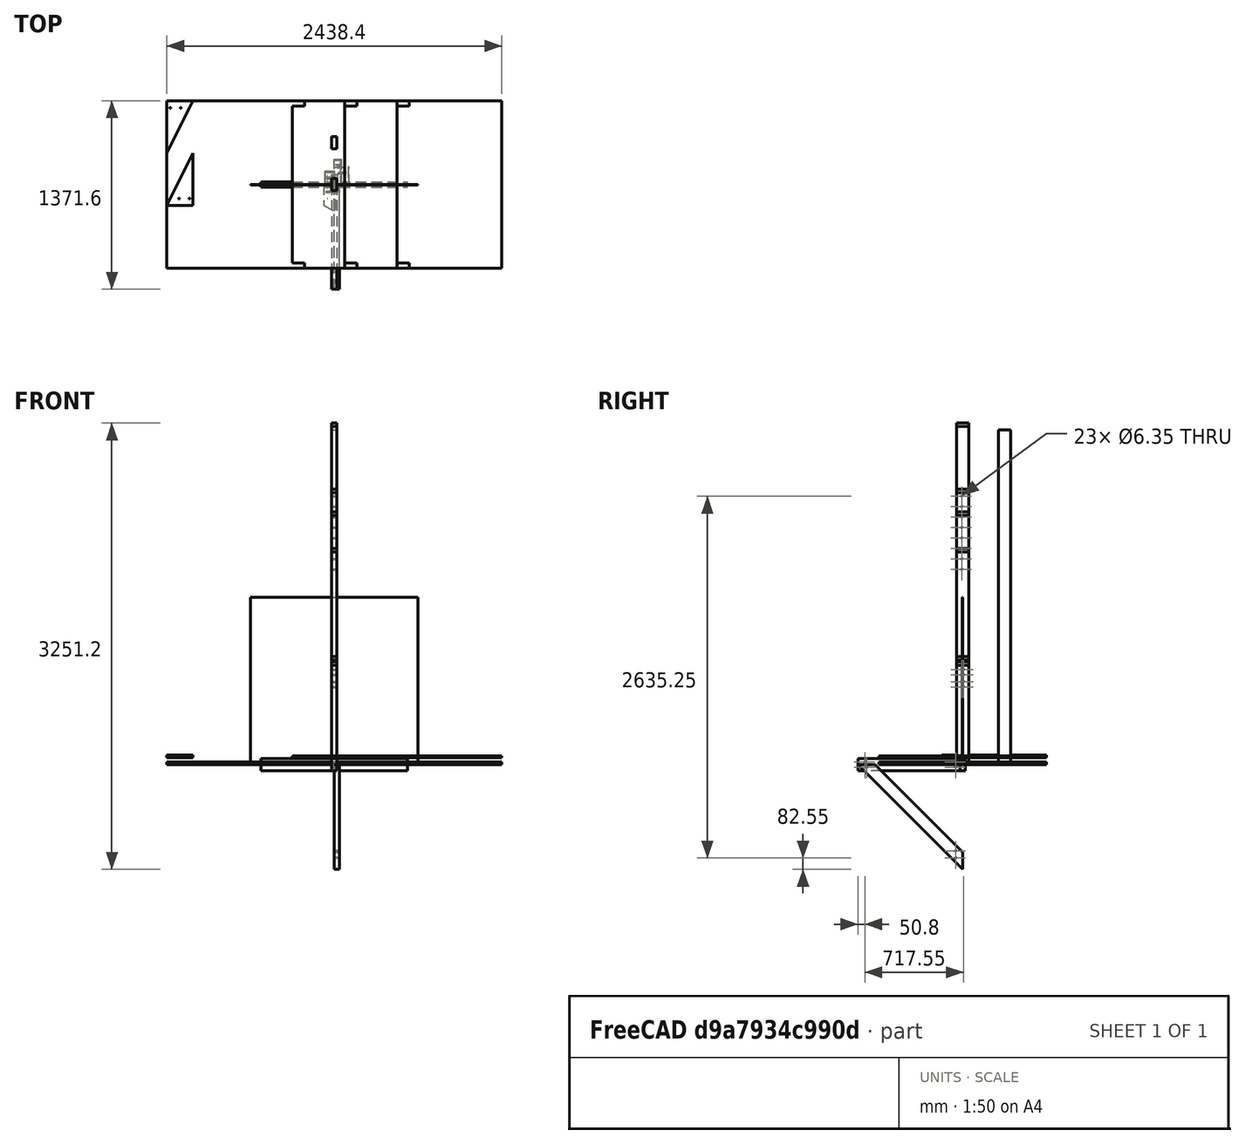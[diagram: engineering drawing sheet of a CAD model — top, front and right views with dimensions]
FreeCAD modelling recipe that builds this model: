
FCSTD DOCUMENT  (FreeCAD 0.21R33771 (Git))
Label: workshop
License: All rights reserved
LicenseURL: http://en.wikipedia.org/wiki/All_rights_reserved
objects: Sketcher::SketchObject×41, PartDesign::Pad×34, PartDesign::Body×29, TechDraw::DrawViewBalloon×25, TechDraw::DrawViewPart×23, App::Part×22, PartDesign::CoordinateSystem×21, PartDesign::Pocket×21, Part::Part2DObjectPython×18, App::Link×17, TechDraw::DrawViewDimension×14, TechDraw::DrawRichAnno×13, TechDraw::DrawSVGTemplate×11, TechDraw::DrawPage×11, App::DocumentObjectGroup×10, Part::FeaturePython×7, PartDesign::Mirrored×3, PartDesign::Hole×1, App::FeaturePython×1, Spreadsheet::Sheet×1
note: 252 computed .brp shape members not serialized (recipe doc carries the construction recipe); baked Part::Feature solids carry a one-line shape summary decoded from their .brp

FEATURE [Sketcher::SketchObject] Sketch  label="S_Electronics_CableMount_Body"
  FullyConstrained = true
  MapMode = 5
  Support = -> [XY_Plane001]
  sketch-geometry (8):
    g0: LineSegment StartX=12.5 StartY=42.5 StartZ=0 EndX=12.5 EndY=12.5 EndZ=0
    g1: LineSegment StartX=-12.5 StartY=12.5 StartZ=0 EndX=-12.5 EndY=42.5 EndZ=0
    g2: ArcOfCircle CenterX=3e-15 CenterY=12.5 CenterZ=0 NormalX=0 NormalY=0 NormalZ=1 AngleXU=0 Radius=12.5 StartAngle=3.14159 EndAngle=6.28319
    g3: LineSegment StartX=22.5 StartY=42.5 StartZ=0 EndX=22.5 EndY=12.5 EndZ=0
    g4: LineSegment StartX=-22.5 StartY=12.5 StartZ=0 EndX=-22.5 EndY=42.5 EndZ=0
    g5: ArcOfCircle CenterX=5.7957e-12 CenterY=12.5 CenterZ=0 NormalX=0 NormalY=0 NormalZ=1 AngleXU=0 Radius=22.5 StartAngle=3.14159 EndAngle=6.28319
    g6: LineSegment StartX=-12.5 StartY=42.5 StartZ=0 EndX=-22.5 EndY=42.5 EndZ=0
    g7: LineSegment StartX=22.5 StartY=42.5 StartZ=0 EndX=12.5 EndY=42.5 EndZ=0
  constraints (20):
    c: Vertical(g0)
    c: Symmetric(g0,g1,g-2)
    c: PointOnObject(g-1,g2)
    c: Tangent(g2,g0) = 1.5708
    c: Tangent(g1,g2) = 1.5708
    c: Vertical(g3)
    c: Coincident(g6,g1)
    c: Coincident(g6,g4)
    c: Coincident(g7,g3)
    c: Coincident(g7,g0)
    c: Tangent(g5,g3) = 1.5708
    c: Tangent(g4,g5) = 1.5708
    c: Horizontal(g6)
    c: Horizontal(g7)
    c: Horizontal(g4,g3)
    c: Horizontal(g4,g1)
    c: Symmetric(g3,g4,g-2)
    c: DistanceX(g7,g7) = 10
    c: DistanceX(g1,g0) = 25
    c: DistanceY(g3,g3) = 30
FEATURE [PartDesign::Pad] Pad  label="PAD_Electronics_CableMount"
  Direction = (0,0,1)
  Length = 10
  Length2 = 10
  Profile = -> Sketch
  ReferenceAxis = -> Sketch [N_Axis]
  Type = 0
FEATURE [Sketcher::SketchObject] Sketch001  label="S_Electronics_CableMount_Hole"
  AttachmentOffset = pos=(0,0,30) rot=(0,0,1;0rad)
  FullyConstrained = true
  MapMode = 5
  Placement = pos=(30,-6.7e-15,6.7e-15) rot=(0.57735,0.57735,0.57735;2.0944rad)
  Support = -> [YZ_Plane001]
  sketch-geometry (1):
    g0: Circle CenterX=35 CenterY=5 CenterZ=0 NormalX=0 NormalY=0 NormalZ=1 AngleXU=0 Radius=2.5
  constraints (3):
    c: Diameter(g0) = 5
    c: DistanceY(g-1,g0) = 5
    c: DistanceX(g-1,g0) = 35
FEATURE [PartDesign::Hole] Hole  label="HOLE_Electronics_CableMount"
  BaseFeature = -> Pad
  CustomThreadClearance = 0
  Depth = 161.858
  DepthType = 1
  Diameter = 5.5
  DrillForDepth = false
  DrillPoint = 0
  DrillPointAngle = 118
  HoleCutCountersinkAngle = 90
  HoleCutCustomValues = false
  HoleCutDepth = 0
  HoleCutDiameter = 6.1
  HoleCutType = 0
  ModelThread = false
  Profile = -> Sketch001
  Tapered = false
  TaperedAngle = 90
  ThreadClass = 0
  ThreadDepth = 161.858
  ThreadDepthType = 0
  ThreadDirection = 0
  ThreadFit = 0
  ThreadSize = 13
  ThreadType = 1
  Threaded = false
  UseCustomThreadClearance = false
FEATURE [PartDesign::Body] Body  label="B_Electronics_CableMount"
  Group = -> [Sketch,Pad,Sketch001,Hole]
  Origin = -> Origin001
  Tip = -> Hole
FEATURE [App::Part] Part  label="P_Electronics_CableMount"
  Group = -> [Body]
  Origin = -> Origin
FEATURE [Sketcher::SketchObject] Sketch002  label="S_Electronics_CableMountSpacer"
  FullyConstrained = true
  MapMode = 5
  Support = -> [XY_Plane003]
  sketch-geometry (7):
    g0: LineSegment StartX=-25 StartY=0 StartZ=0 EndX=25 EndY=0 EndZ=0
    g1: LineSegment StartX=25 StartY=0 StartZ=0 EndX=25 EndY=70 EndZ=0
    g2: LineSegment StartX=25 StartY=70 StartZ=0 EndX=-25 EndY=70 EndZ=0
    g3: LineSegment StartX=-25 StartY=70 StartZ=0 EndX=-25 EndY=0 EndZ=0
    g4: Circle CenterX=0 CenterY=60 CenterZ=0 NormalX=0 NormalY=0 NormalZ=1 AngleXU=0 Radius=2.5
    g5: Circle CenterX=0 CenterY=35 CenterZ=0 NormalX=0 NormalY=0 NormalZ=1 AngleXU=0 Radius=2.5
    g6: Circle CenterX=0 CenterY=10 CenterZ=0 NormalX=0 NormalY=0 NormalZ=1 AngleXU=0 Radius=2.5
  constraints (20):
    c: Coincident(g0,g1)
    c: Coincident(g1,g2)
    c: Coincident(g2,g3)
    c: Coincident(g3,g0)
    c: Horizontal(g2)
    c: Vertical(g1)
    c: Vertical(g3)
    c: PointOnObject(g0,g-1)
    c: Symmetric(g0,g0,g-2)
    c: DistanceX(g2,g2) = 50
    c: DistanceY(g1,g1) = 70
    c: PointOnObject(g4,g-2)
    c: PointOnObject(g5,g-2)
    c: PointOnObject(g6,g-2)
    c: Equal(g6,g5)
    c: Equal(g5,g4)
    c: Diameter(g4) = 5
    c: DistanceY(g-1,g6) = 10
    c: DistanceY(g4,g2) = 10
    c: DistanceY(g-1,g5) = 35
FEATURE [PartDesign::Pad] Pad001  label="PAD_Electronics_CableMountSpacer"
  Direction = (0,0,1)
  Length = 2
  Length2 = 10
  Profile = -> Sketch002
  ReferenceAxis = -> Sketch002 [N_Axis]
  Type = 0
FEATURE [Sketcher::SketchObject] Sketch003  label="S_Electronics_CableMountSpacer_Side"
  FullyConstrained = true
  MapMode = 5
  Support = -> [XY_Plane003]
  expr: Constraints[9] = 41.5 mm / 2
  sketch-geometry (4):
    g0: LineSegment StartX=20.75 StartY=70 StartZ=0 EndX=25 EndY=70 EndZ=0
    g1: LineSegment StartX=25 StartY=70 StartZ=0 EndX=25 EndY=0 EndZ=0
    g2: LineSegment StartX=25 StartY=0 StartZ=0 EndX=20.75 EndY=0 EndZ=0
    g3: LineSegment StartX=20.75 StartY=0 StartZ=0 EndX=20.75 EndY=70 EndZ=0
  constraints (12):
    c: Coincident(g0,g1)
    c: Coincident(g1,g2)
    c: Coincident(g2,g3)
    c: Coincident(g3,g0)
    c: Horizontal(g0)
    c: Horizontal(g2)
    c: Vertical(g1)
    c: Vertical(g3)
    c: PointOnObject(g1,g-1)
    c: DistanceX(g-1,g2) = 20.75
    c: DistanceX(g-1,g1) = 25
    c: DistanceY(g1,g1) = 70
FEATURE [PartDesign::Pad] Pad002  label="PAD_Electronics_CableMountSpacer_Side"
  BaseFeature = -> Pad001
  Direction = (0,0,1)
  Length = 4
  Length2 = 10
  Profile = -> Sketch003
  ReferenceAxis = -> Sketch003 [N_Axis]
  Type = 0
FEATURE [PartDesign::Mirrored] Mirrored  label="PAT_Electronics_CableMountSpacer_Side"
  BaseFeature = -> Pad002
  MirrorPlane = -> Sketch003 [V_Axis]
  Originals = -> [Pad002]
FEATURE [PartDesign::Body] Body001  label="B_Electronics_CableMountSpacer"
  Group = -> [Sketch002,Pad001,Sketch003,Pad002,Mirrored]
  Origin = -> Origin003
  Tip = -> Mirrored
FEATURE [App::Part] Part001  label="P_Electronics_CableMountSpacer"
  Group = -> [Body001]
  Origin = -> Origin002
FEATURE [PartDesign::CoordinateSystem] LCS_Origin
  AttacherType = Attacher::AttachEngine3D
  MapMode = 2
  Support = -> [X_Axis008]
FEATURE [App::DocumentObjectGroup] Constraints
FEATURE [App::FeaturePython] Variables  # WARN: FeaturePython — macro-defined, semantics opaque (R4)
  Type = App::PropertyContainer
FEATURE [App::DocumentObjectGroup] Configurations
FEATURE [Sketcher::SketchObject] Sketch005  label="S_Workbench_Top_Base"
  FullyConstrained = true
  MapMode = 5
  Support = -> [XY_Plane007]
  expr: Constraints[8] = <<S_Workbench_Master>>.Constraints.TableWidth
  sketch-geometry (4):
    g0: LineSegment StartX=-609.6 StartY=0 StartZ=0 EndX=609.6 EndY=0 EndZ=0
    g1: LineSegment StartX=609.6 StartY=0 StartZ=0 EndX=609.6 EndY=-762 EndZ=0
    g2: LineSegment StartX=609.6 StartY=-762 StartZ=0 EndX=-609.6 EndY=-762 EndZ=0
    g3: LineSegment StartX=-609.6 StartY=-762 StartZ=0 EndX=-609.6 EndY=0 EndZ=0
  constraints (11):
    c: Coincident(g0,g1)
    c: Coincident(g1,g2)
    c: Coincident(g2,g3)
    c: Coincident(g3,g0)
    c: Horizontal(g0)
    c: Horizontal(g2)
    c: Vertical(g1)
    c: Vertical(g3)
    c: DistanceX(g0,g0) = 1219.2
    c: DistanceY(g1,g1) = 762
    c: Symmetric(g0,g0,g-1)
FEATURE [PartDesign::Pad] Pad004  label="PAD_Workbench_Top_Base"
  Direction = (0,0,1)
  Length = 12.7
  Length2 = 10
  Profile = -> Sketch005
  ReferenceAxis = -> Sketch005 [N_Axis]
  Type = 0
  expr: Length = <<S_Workbench_Master>>.Constraints.TableThickness
FEATURE [Sketcher::SketchObject] Sketch006  label="S_Workbench_Top_BackHole"
  ExternalGeometry = -> [Pad004]
  FullyConstrained = true
  MapMode = 5
  Placement = pos=(0,0,12.7) rot=(0,0,1;0rad)
  Support = -> [Pad004]
  expr: Constraints[8] = Sketch009.Constraints.TwobyfourWidth
  expr: Constraints[9] = Sketch009.Constraints.TwobyfourHeight
  sketch-geometry (4):
    g0: LineSegment StartX=-571.5 StartY=0 StartZ=0 EndX=-609.6 EndY=0 EndZ=0
    g1: LineSegment StartX=-609.6 StartY=0 StartZ=0 EndX=-609.6 EndY=-88.9 EndZ=0
    g2: LineSegment StartX=-609.6 StartY=-88.9 StartZ=0 EndX=-571.5 EndY=-88.9 EndZ=0
    g3: LineSegment StartX=-571.5 StartY=-88.9 StartZ=0 EndX=-571.5 EndY=0 EndZ=0
  constraints (11):
    c: Coincident(g0,g1)
    c: Coincident(g1,g2)
    c: Coincident(g2,g3)
    c: Coincident(g3,g0)
    c: Horizontal(g0)
    c: Horizontal(g2)
    c: Vertical(g1)
    c: Vertical(g3)
    c: DistanceX(g0,g0) = 38.1
    c: DistanceY(g3,g3) = 88.9
    c: Coincident(g0,g-3)
FEATURE [PartDesign::Pocket] Pocket  label="POCKET_Workbench_Top_BackHole"
  BaseFeature = -> Pad004
  Direction = (0,0,-1)
  Length = 25.4
  Length2 = 5
  Profile = -> Sketch006
  ReferenceAxis = -> Sketch006 [N_Axis]
  Type = 0
FEATURE [PartDesign::Mirrored] Mirrored001  label="PAT_B_Workbench_Top_BackHoles"
  BaseFeature = -> Pocket
  MirrorPlane = -> Sketch006 [V_Axis]
  Originals = -> [Pocket]
FEATURE [PartDesign::Body] Body003  label="B_Workbench_Top"
  Group = -> [Sketch005,Pad004,Sketch006,Pocket,Mirrored001]
  Origin = -> Origin007
  Tip = -> Mirrored001
FEATURE [PartDesign::CoordinateSystem] LCS_Workbench_Top_Origin
  AttacherType = Attacher::AttachEngine3D
FEATURE [PartDesign::CoordinateSystem] LCS_Workbench_Top_Back_Left_Leg
  AttacherType = Attacher::AttachEngine3D
  Placement = pos=(-590.55,-44.45,0) rot=(0,0,1;0rad)
  expr: .Placement.Base.x = -(<<S_Workbench_Master>>.Constraints.TableWidth - Sketch009.Constraints.TwobyfourWidth) / 2
  expr: .Placement.Base.y = -Sketch009.Constraints.TwobyfourHeight / 2
FEATURE [PartDesign::CoordinateSystem] LCS_Workbench_Top_Back_Right_Leg
  AttacherType = Attacher::AttachEngine3D
  Placement = pos=(590.55,-44.45,0) rot=(0,0,1;0rad)
  expr: .Placement.Base.x = (<<S_Workbench_Master>>.Constraints.TableWidth - Sketch009.Constraints.TwobyfourWidth) / 2
  expr: .Placement.Base.y = -Sketch009.Constraints.TwobyfourHeight / 2
FEATURE [PartDesign::CoordinateSystem] LCS_Workbench_Top_Front_Left_Leg
  AttacherType = Attacher::AttachEngine3D
  Placement = pos=(-590.55,-717.55,0) rot=(0,0,1;0rad)
  expr: .Placement.Base.x = -(<<S_Workbench_Master>>.Constraints.TableWidth - Sketch009.Constraints.TwobyfourWidth) / 2
  expr: .Placement.Base.y = -<<S_Workbench_Master>>.Constraints.TableDepth + Sketch009.Constraints.TwobyfourHeight / 2
FEATURE [PartDesign::CoordinateSystem] LCS_Workbench_Top_Front_Right_Leg
  AttacherType = Attacher::AttachEngine3D
  Placement = pos=(590.55,-717.55,0) rot=(0,0,1;0rad)
  expr: .Placement.Base.x = (<<S_Workbench_Master>>.Constraints.TableWidth - Sketch009.Constraints.TwobyfourWidth) / 2
  expr: .Placement.Base.y = -<<S_Workbench_Master>>.Constraints.TableDepth + Sketch009.Constraints.TwobyfourHeight / 2
FEATURE [App::Part] Part003  label="P_Workbench_Top"
  Group = -> [Body003,LCS_Workbench_Top_Origin,LCS_Workbench_Top_Back_Left_Leg,LCS_Workbench_Top_Back_Right_Leg,LCS_Workbench_Top_Front_Left_Leg,LCS_Workbench_Top_Front_Right_Leg]
  Origin = -> Origin006
FEATURE [Sketcher::SketchObject] Sketch007  label="S_Workbench_BackLeg_Base"
  FullyConstrained = true
  MapMode = 5
  Support = -> [XY_Plane010]
  expr: Constraints[10] = Sketch009.Constraints.TwobyfourHeight
  expr: Constraints[9] = Sketch009.Constraints.TwobyfourWidth
  sketch-geometry (4):
    g0: LineSegment StartX=-19.05 StartY=44.45 StartZ=0 EndX=19.05 EndY=44.45 EndZ=0
    g1: LineSegment StartX=19.05 StartY=44.45 StartZ=0 EndX=19.05 EndY=-44.45 EndZ=0
    g2: LineSegment StartX=19.05 StartY=-44.45 StartZ=0 EndX=-19.05 EndY=-44.45 EndZ=0
    g3: LineSegment StartX=-19.05 StartY=-44.45 StartZ=0 EndX=-19.05 EndY=44.45 EndZ=0
  constraints (11):
    c: Coincident(g0,g1)
    c: Coincident(g1,g2)
    c: Coincident(g2,g3)
    c: Coincident(g3,g0)
    c: Horizontal(g0)
    c: Horizontal(g2)
    c: Vertical(g1)
    c: Vertical(g3)
    c: Symmetric(g0,g1,g-1)
    c: DistanceX(g0,g0) = 38.1
    c: DistanceY(g1,g1) = 88.9
FEATURE [PartDesign::Pad] Pad005  label="PAD_Workbench_BackLeg"
  Direction = (0,0,1)
  Length = 1981.2
  Length2 = 10
  Profile = -> Sketch007
  ReferenceAxis = -> Sketch007 [N_Axis]
  Type = 0
  expr: Length = <<S_Workbench_Master>>.Constraints.BackLegHeight
FEATURE [PartDesign::CoordinateSystem] LCS_BackLeg_Origin  label="LCS_Workbench_BackLeg_Origin"
  AttacherType = Attacher::AttachEngine3D
FEATURE [PartDesign::CoordinateSystem] LCS_Workbench_BackLeg_Top
  AttacherType = Attacher::AttachEngine3D
  Placement = pos=(0,0,1981.2) rot=(0,0,1;0rad)
  expr: .Placement.Base.z = <<S_Workbench_Master>>.Constraints.BackLegHeight
FEATURE [PartDesign::CoordinateSystem] LCS_Workbench_BackLeg_TableHeight
  AttacherType = Attacher::AttachEngine3D
  Placement = pos=(0,0,723.9) rot=(0,0,1;0rad)
  expr: .Placement.Base.z = Sketch009.Constraints.FrontLegHeight
FEATURE [App::Link] P_Workbench_BackLeg  label="P_Workbench_BackLeg001"
  AttachedBy = #LCS_BackLeg_Origin
  AttachedTo = P_Workbench_Top#LCS_Workbench_Top_Back_Right_Leg
  AttachmentOffset = pos=(0,0,-723.9) rot=(0,0,1;0rad)
  LinkPlacement = pos=(590.55,-44.45,0) rot=(0,0,1;0rad)
  LinkedObject = -> Part004
  Placement = pos=(590.55,-44.45,0) rot=(0,0,1;0rad)
  SolverId = Asm4EE
  expr: .AttachmentOffset.Base.z = -<<S_Workbench_Master>>.Constraints.FrontLegHeight
  expr: Placement = P_Workbench_Top.Placement * LCS_Workbench_Top_Back_Right_Leg.Placement * AttachmentOffset * LCS_BackLeg_Origin.Placement ^ -1
FEATURE [App::Link] P_Workbench_BackLeg001  label="P_Workbench_BackLeg002"
  AttachedBy = #LCS_BackLeg_Origin
  AttachedTo = P_Workbench_Top#LCS_Workbench_Top_Back_Left_Leg
  AttachmentOffset = pos=(0,0,-723.9) rot=(0,0,1;0rad)
  LinkPlacement = pos=(-590.55,-44.45,0) rot=(0,0,1;0rad)
  LinkedObject = -> Part004
  Placement = pos=(-590.55,-44.45,0) rot=(0,0,1;0rad)
  SolverId = Asm4EE
  expr: .AttachmentOffset.Base.z = -<<S_Workbench_Master>>.Constraints.FrontLegHeight
  expr: Placement = P_Workbench_Top.Placement * LCS_Workbench_Top_Back_Left_Leg.Placement * AttachmentOffset * LCS_BackLeg_Origin.Placement ^ -1
FEATURE [App::Link] P_Workbench_Top  label="P_Workbench_Top001"
  AttachedBy = #LCS_Workbench_Top_Origin
  AttachedTo = Parent Assembly#LCS_Origin
  AttachmentOffset = pos=(0,0,723.9) rot=(0,0,1;0rad)
  LinkPlacement = pos=(0,0,723.9) rot=(0,0,1;0rad)
  LinkedObject = -> Part003
  Placement = pos=(0,0,723.9) rot=(0,0,1;0rad)
  SolverId = Asm4EE
  expr: .AttachmentOffset.Base.z = <<S_Workbench_Master>>.Constraints.FrontLegHeight
  expr: Placement = LCS_Origin.Placement * AttachmentOffset * LCS_Workbench_Top_Origin.Placement ^ -1
FEATURE [Sketcher::SketchObject] Sketch008  label="S_Workbench_FrontLeg_Base"
  FullyConstrained = true
  MapMode = 5
  Support = -> [XY_Plane012]
  expr: Constraints[10] = Sketch009.Constraints.TwobyfourHeight
  expr: Constraints[9] = Sketch009.Constraints.TwobyfourWidth
  sketch-geometry (4):
    g0: LineSegment StartX=-19.05 StartY=44.45 StartZ=0 EndX=19.05 EndY=44.45 EndZ=0
    g1: LineSegment StartX=19.05 StartY=44.45 StartZ=0 EndX=19.05 EndY=-44.45 EndZ=0
    g2: LineSegment StartX=19.05 StartY=-44.45 StartZ=0 EndX=-19.05 EndY=-44.45 EndZ=0
    g3: LineSegment StartX=-19.05 StartY=-44.45 StartZ=0 EndX=-19.05 EndY=44.45 EndZ=0
  constraints (11):
    c: Coincident(g0,g1)
    c: Coincident(g1,g2)
    c: Coincident(g2,g3)
    c: Coincident(g3,g0)
    c: Horizontal(g0)
    c: Horizontal(g2)
    c: Vertical(g1)
    c: Vertical(g3)
    c: Symmetric(g0,g1,g-1)
    c: DistanceX(g0,g0) = 38.1
    c: DistanceY(g1,g1) = 88.9
FEATURE [PartDesign::Pad] Pad006  label="PAD_Workbench_FrontLeg_Base"
  Direction = (0,0,1)
  Length = 723.9
  Length2 = 10
  Profile = -> Sketch008
  ReferenceAxis = -> Sketch008 [N_Axis]
  Type = 0
  expr: Length = Sketch009.Constraints.FrontLegHeight
FEATURE [Sketcher::SketchObject] Sketch009  label="S_Workbench_Master"
  FullyConstrained = true
  Placement = pos=(0,0,0) rot=(1,0,0;1.5708rad)
  sketch-geometry (23):
    g0: LineSegment StartX=0 StartY=0 StartZ=0 EndX=0 EndY=736.6 EndZ=0
    g1: LineSegment StartX=0 StartY=736.6 StartZ=0 EndX=1219.2 EndY=736.6 EndZ=0
    g2: LineSegment StartX=1219.2 StartY=736.6 StartZ=0 EndX=1758.02 EndY=1275.42 EndZ=0
    g3: LineSegment StartX=0 StartY=736.6 StartZ=0 EndX=538.815 EndY=1275.42 EndZ=0
    g4: LineSegment StartX=538.815 StartY=1275.42 StartZ=0 EndX=1758.02 EndY=1275.42 EndZ=0
    g5: LineSegment StartX=538.815 StartY=1275.42 StartZ=0 EndX=538.815 EndY=2520.02 EndZ=0
    g6: LineSegment StartX=538.815 StartY=1275.42 StartZ=0 EndX=538.815 EndY=538.815 EndZ=0
    g7: LineSegment StartX=538.815 StartY=2062.82 StartZ=0 EndX=269.408 EndY=1793.41 EndZ=0
    g8: LineSegment StartX=0 StartY=723.9 StartZ=0 EndX=1219.2 EndY=723.9 EndZ=0
    g9: LineSegment StartX=1219.2 StartY=723.9 StartZ=0 EndX=1219.2 EndY=736.6 EndZ=0
    g10: LineSegment StartX=1219.2 StartY=723.9 StartZ=0 EndX=1758.02 EndY=1262.72 EndZ=0
    g11: LineSegment StartX=1758.02 StartY=1262.72 StartZ=0 EndX=1758.02 EndY=1275.42 EndZ=0
    g12: LineSegment StartX=538.815 StartY=2367.62 StartZ=0 EndX=269.408 EndY=2098.21 EndZ=0
    g13: LineSegment StartX=0 StartY=723.9 StartZ=0 EndX=538.815 EndY=1262.72 EndZ=0
    g14: LineSegment StartX=1758.02 StartY=1275.42 StartZ=0 EndX=1760.26 EndY=1277.66 EndZ=0
    g15: LineSegment StartX=1760.26 StartY=1277.66 StartZ=0 EndX=1760.26 EndY=2496.86 EndZ=0
    g16: LineSegment StartX=1758.02 StartY=1275.42 StartZ=0 EndX=1758.02 EndY=2494.62 EndZ=0
    g17: LineSegment StartX=1758.02 StartY=2494.62 StartZ=0 EndX=1760.26 EndY=2496.86 EndZ=0
    g18: LineSegment StartX=-647.7 StartY=-609.6 StartZ=0 EndX=-609.6 EndY=-609.6 EndZ=0
    g19: LineSegment StartX=-609.6 StartY=-609.6 StartZ=0 EndX=-609.6 EndY=-698.5 EndZ=0
    g20: LineSegment StartX=-609.6 StartY=-698.5 StartZ=0 EndX=-647.7 EndY=-698.5 EndZ=0
    g21: LineSegment StartX=-647.7 StartY=-698.5 StartZ=0 EndX=-647.7 EndY=-609.6 EndZ=0
    g22: Circle CenterX=50.8 CenterY=-50.8 CenterZ=0 NormalX=0 NormalY=0 NormalZ=1 AngleXU=0 Radius=3.175
  constraints (71):
    c: Coincident(g0,g-1)
    c: Vertical(g0)
    c: DistanceY(g0,g0) = 736.6  'TableHeight'
    c: Coincident(g1,g0)
    c: Horizontal(g1)
    c: DistanceX(g1,g1) = 1219.2  'TableWidth'
    c: Coincident(g2,g1)
    c: Angle(g2,g1) = 2.35619
    c: Distance(g2) = 762  'TableDepth'
    c: Coincident(g3,g0)
    c: Coincident(g4,g2)
    c: Horizontal(g4)
    c: Equal(g4,g1)
    c: Coincident(g3,g4)
    c: Coincident(g5,g3)
    c: Vertical(g5)
    c: Coincident(g6,g3)
    c: Vertical(g6)
    c: Equal(g6,g0)
    c: DistanceY(g6,g5) = 1981.2  'BackLegHeight'
    c: PointOnObject(g7,g5)
    c: Parallel(g7,g3)
    c: Distance(g7) = 381  'ShelfDepth'
    c: DistanceY(g6,g7) = 1524  'ShelfHeight'
    c: DistanceY(g3,g7) = 787.4
    c: PointOnObject(g8,g0)
    c: Horizontal(g8)
    c: Coincident(g9,g8)
    c: Coincident(g9,g1)
    c: Vertical(g9)
    c: Coincident(g10,g8)
    c: Coincident(g11,g10)
    c: Coincident(g11,g2)
    c: Vertical(g11)
    c: Parallel(g10,g2)
    c: DistanceY(g11,g11) = 12.7  'TableThickness'
    c: DistanceY(g0,g8) = 723.9  'FrontLegHeight'
    c: PointOnObject(g12,g5)
    c: Parallel(g12,g7)
    c: Equal(g12,g7)
    c: DistanceY(g7,g12) = 304.8  'ShelfSpacing'
    c: Coincident(g13,g8)
    c: PointOnObject(g13,g6)
    c: Parallel(g13,g3)
    c: DistanceY(g6,g6) = 736.6
    c: Coincident(g14,g2)
    c: Coincident(g15,g14)
    c: Vertical(g15)
    c: Coincident(g16,g2)
    c: Vertical(g16)
    c: Coincident(g17,g16)
    c: Coincident(g17,g15)
    c: Parallel(g17,g14)
    c: Parallel(g14,g2)
    c: Distance(g17) = 3.175  'BackThickness'
    c: Coincident(g18,g19)
    c: Coincident(g19,g20)
    c: Coincident(g20,g21)
    c: Coincident(g21,g18)
    c: Horizontal(g18)
    c: Horizontal(g20)
    c: Vertical(g19)
    c: Vertical(g21)
    c: DistanceX(g18,g18) = 38.1  'TwobyfourWidth'
    c: DistanceY(g19,g19) = 88.9  'TwobyfourHeight'
    c: DistanceX(g18,g0) = 609.6
    c: DistanceY(g18,g0) = 609.6
    c: Diameter(g22) = 6.35  'BoltDiameter'
    c: DistanceX(g0,g22) = 50.8
    c: DistanceY(g22,g0) = 50.8
    c: DistanceY(g16,g16) = 1219.2  'BackHeight'
FEATURE [App::Link] P_Workbench_FrontLeg  label="P_Workbench_FrontLeg001"
  AttachedBy = #LCS_Workbench_FrontLeg_Top
  AttachedTo = P_Workbench_Top#LCS_Workbench_Top_Front_Left_Leg
  LinkPlacement = pos=(-590.55,-717.55,0) rot=(0,0,1;0rad)
  LinkedObject = -> Part005
  Placement = pos=(-590.55,-717.55,0) rot=(0,0,1;0rad)
  SolverId = Asm4EE
  expr: Placement = P_Workbench_Top.Placement * LCS_Workbench_Top_Front_Left_Leg.Placement * AttachmentOffset * LCS_Workbench_FrontLeg_Top.Placement ^ -1
FEATURE [PartDesign::CoordinateSystem] LCS_Workbench_FrontLeg_Origin
  AttacherType = Attacher::AttachEngine3D
FEATURE [PartDesign::CoordinateSystem] LCS_Workbench_FrontLeg_Top
  AttacherType = Attacher::AttachEngine3D
  Placement = pos=(0,0,723.9) rot=(0,0,1;0rad)
  expr: .Placement.Base.z = Sketch009.Constraints.FrontLegHeight
FEATURE [App::Link] P_Workbench_1
  AttachedBy = #LCS_Workbench_FrontLeg_Top
  AttachedTo = P_Workbench_Top#LCS_Workbench_Top_Front_Right_Leg
  LinkPlacement = pos=(590.55,-717.55,0) rot=(0,0,1;0rad)
  LinkedObject = -> Part005
  Placement = pos=(590.55,-717.55,0) rot=(0,0,1;0rad)
  SolverId = Asm4EE
  expr: Placement = P_Workbench_Top.Placement * LCS_Workbench_Top_Front_Right_Leg.Placement * AttachmentOffset * LCS_Workbench_FrontLeg_Top.Placement ^ -1
FEATURE [Sketcher::SketchObject] Sketch010  label="S_Workbench_Shelf_Base"
  FullyConstrained = true
  MapMode = 5
  Support = -> [XY_Plane014]
  expr: Constraints[10] = <<S_Workbench_Master>>.Constraints.ShelfDepth
  expr: Constraints[9] = <<S_Workbench_Master>>.Constraints.TableWidth
  sketch-geometry (4):
    g0: LineSegment StartX=-609.6 StartY=0 StartZ=0 EndX=609.6 EndY=0 EndZ=0
    g1: LineSegment StartX=609.6 StartY=0 StartZ=0 EndX=609.6 EndY=-381 EndZ=0
    g2: LineSegment StartX=609.6 StartY=-381 StartZ=0 EndX=-609.6 EndY=-381 EndZ=0
    g3: LineSegment StartX=-609.6 StartY=-381 StartZ=0 EndX=-609.6 EndY=0 EndZ=0
  constraints (11):
    c: Coincident(g0,g1)
    c: Coincident(g1,g2)
    c: Coincident(g2,g3)
    c: Coincident(g3,g0)
    c: Horizontal(g0)
    c: Horizontal(g2)
    c: Vertical(g1)
    c: Vertical(g3)
    c: Symmetric(g0,g0,g-1)
    c: DistanceX(g0,g0) = 1219.2
    c: DistanceY(g1,g1) = 381
FEATURE [PartDesign::Pad] Pad007  label="PAD_Workbench_Shelf_Base"
  Direction = (0,0,1)
  Length = 12.7
  Length2 = 10
  Profile = -> Sketch010
  ReferenceAxis = -> Sketch010 [N_Axis]
  Type = 0
  expr: Length = <<S_Workbench_Master>>.Constraints.TableThickness
FEATURE [Sketcher::SketchObject] Sketch011  label="S_Workbench_Shelf_LegSlot"
  FullyConstrained = true
  MapMode = 5
  Support = -> [XY_Plane014]
  expr: Constraints[10] = Sketch009.Constraints.TwobyfourWidth
  expr: Constraints[11] = <<S_Workbench_Master>>.Constraints.TableWidth / 2
  expr: Constraints[9] = Sketch009.Constraints.TwobyfourHeight
  sketch-geometry (4):
    g0: LineSegment StartX=-609.6 StartY=0 StartZ=0 EndX=-571.5 EndY=0 EndZ=0
    g1: LineSegment StartX=-571.5 StartY=0 StartZ=0 EndX=-571.5 EndY=-88.9 EndZ=0
    g2: LineSegment StartX=-571.5 StartY=-88.9 StartZ=0 EndX=-609.6 EndY=-88.9 EndZ=0
    g3: LineSegment StartX=-609.6 StartY=-88.9 StartZ=0 EndX=-609.6 EndY=0 EndZ=0
  constraints (12):
    c: Coincident(g0,g1)
    c: Coincident(g1,g2)
    c: Coincident(g2,g3)
    c: Coincident(g3,g0)
    c: Horizontal(g0)
    c: Horizontal(g2)
    c: Vertical(g1)
    c: Vertical(g3)
    c: Horizontal(g0,g-1)
    c: DistanceY(g1,g1) = 88.9
    c: DistanceX(g2,g2) = 38.1
    c: DistanceX(g0,g-1) = 609.6
FEATURE [PartDesign::Pocket] Pocket001  label="POCKET_Workbench_Shelf_LegSlot"
  BaseFeature = -> Pad007
  Direction = (0,0,-1)
  Length = 25.4
  Length2 = 5
  Profile = -> Sketch011
  ReferenceAxis = -> Sketch011 [N_Axis]
  Reversed = true
  Type = 0
  expr: Length = <<S_Workbench_Master>>.Constraints.TableThickness * 2
FEATURE [PartDesign::Mirrored] Mirrored002  label="PAT_Workbench_Shelf_LegSlots"
  BaseFeature = -> Pocket001
  MirrorPlane = -> Sketch011 [V_Axis]
  Originals = -> [Pocket001]
FEATURE [PartDesign::Body] Body006  label="B_Workbench_Shelf"
  Group = -> [Sketch010,Pad007,Sketch011,Pocket001,Mirrored002]
  Origin = -> Origin014
  Tip = -> Mirrored002
FEATURE [PartDesign::CoordinateSystem] LCS_Workbench_Shelf_LeftLeg
  AttacherType = Attacher::AttachEngine3D
  Placement = pos=(-590.55,-44.45,0) rot=(0,0,1;0rad)
  expr: .Placement.Base.x = -(<<S_Workbench_Master>>.Constraints.TableWidth - 1.5 in) / 2
FEATURE [PartDesign::CoordinateSystem] LCS_Workbench_Shelf_RightLeg
  AttacherType = Attacher::AttachEngine3D
  Placement = pos=(590.55,-44.45,0) rot=(0,0,1;0rad)
  expr: .Placement.Base.x = (<<S_Workbench_Master>>.Constraints.TableWidth - 1.5 in) / 2
FEATURE [App::Part] Part006  label="P_Workbench_Shelf"
  Group = -> [Body006,LCS_Workbench_Shelf_LeftLeg,LCS_Workbench_Shelf_RightLeg]
  Origin = -> Origin013
FEATURE [App::Link] P_Workbench_Shelf  label="P_Workbench_Shelf001"
  AttachedBy = #LCS_Workbench_Shelf_LeftLeg
  AttachedTo = P_Workbench_BackLeg001#LCS_Workbench_BackLeg_Shelf
  LinkPlacement = pos=(0,0,1524) rot=(0,0,1;0rad)
  LinkedObject = -> Part006
  Placement = pos=(0,0,1524) rot=(0,0,1;0rad)
  SolverId = Asm4EE
  expr: Placement = P_Workbench_BackLeg001.Placement * LCS_Workbench_BackLeg_Shelf.Placement * AttachmentOffset * LCS_Workbench_Shelf_LeftLeg.Placement ^ -1
FEATURE [PartDesign::CoordinateSystem] LCS_Workbench_BackLeg_Shelf
  AttacherType = Attacher::AttachEngine3D
  Placement = pos=(0,0,1524) rot=(0,0,1;0rad)
  expr: .Placement.Base.z = Sketch009.Constraints.ShelfHeight
FEATURE [PartDesign::CoordinateSystem] LCS_Workbench_BackLeg_Shelf2
  AttacherType = Attacher::AttachEngine3D
  Placement = pos=(0,0,1828.8) rot=(0,0,1;0rad)
  expr: .Placement.Base.z = <<S_Workbench_Master>>.Constraints.ShelfHeight + <<S_Workbench_Master>>.Constraints.ShelfSpacing
FEATURE [App::Link] P_Workbench_Shelf001  label="P_Workbench_Shelf002"
  AttachedBy = #LCS_Workbench_Shelf_LeftLeg
  AttachedTo = P_Workbench_BackLeg001#LCS_Workbench_BackLeg_Shelf2
  LinkPlacement = pos=(0,0,1828.8) rot=(0,0,1;0rad)
  LinkedObject = -> Part006
  Placement = pos=(0,0,1828.8) rot=(0,0,1;0rad)
  SolverId = Asm4EE
  expr: Placement = P_Workbench_BackLeg001.Placement * LCS_Workbench_BackLeg_Shelf2.Placement * AttachmentOffset * LCS_Workbench_Shelf_LeftLeg.Placement ^ -1
FEATURE [Sketcher::SketchObject] Sketch012  label="S_Workbench_SideBrace_Body"
  FullyConstrained = true
  MapMode = 5
  Placement = pos=(0,0,0) rot=(1,0,0;1.5708rad)
  Support = -> [XZ_Plane016]
  expr: Constraints[10] = Sketch009.Constraints.TwobyfourHeight
  expr: Constraints[9] = Sketch009.Constraints.TwobyfourWidth
  sketch-geometry (4):
    g0: LineSegment StartX=-19.05 StartY=44.45 StartZ=0 EndX=19.05 EndY=44.45 EndZ=0
    g1: LineSegment StartX=19.05 StartY=44.45 StartZ=0 EndX=19.05 EndY=-44.45 EndZ=0
    g2: LineSegment StartX=19.05 StartY=-44.45 StartZ=0 EndX=-19.05 EndY=-44.45 EndZ=0
    g3: LineSegment StartX=-19.05 StartY=-44.45 StartZ=0 EndX=-19.05 EndY=44.45 EndZ=0
  constraints (11):
    c: Coincident(g0,g1)
    c: Coincident(g1,g2)
    c: Coincident(g2,g3)
    c: Coincident(g3,g0)
    c: Horizontal(g0)
    c: Horizontal(g2)
    c: Vertical(g1)
    c: Vertical(g3)
    c: Symmetric(g0,g1,g-1)
    c: DistanceX(g0,g0) = 38.1
    c: DistanceY(g1,g1) = 88.9
FEATURE [PartDesign::Pad] Pad008  label="PAD_Workbench_SideBrace_Body"
  Direction = (0,-1,-2e-16)
  Length = 762
  Length2 = 10
  Placement = pos=(0,0,0) rot=(1,0,0;1.5708rad)
  Profile = -> Sketch012
  ReferenceAxis = -> Sketch012 [N_Axis]
  Type = 0
  expr: Length = <<S_Workbench_Master>>.Constraints.TableDepth
FEATURE [PartDesign::CoordinateSystem] LCS_Workbench_SideBrace_Origin
  AttacherType = Attacher::AttachEngine3D
FEATURE [App::Link] P_Workbench_SideBrace  label="P_Workbench_SideBrace001"
  AttachedBy = #LCS_Workbench_SideBrace_Origin
  AttachedTo = P_Workbench_BackLeg001#LCS_Workbench_BackLeg_TableHeight
  AttachmentOffset = pos=(38.1,44.45,-44.45) rot=(0,0,1;0rad)
  LinkPlacement = pos=(-552.45,-7.1e-15,679.45) rot=(0,0,1;0rad)
  LinkedObject = -> Part007
  Placement = pos=(-552.45,-7.1e-15,679.45) rot=(0,0,1;0rad)
  SolverId = Asm4EE
  expr: Placement = P_Workbench_BackLeg001.Placement * LCS_Workbench_BackLeg_TableHeight.Placement * AttachmentOffset * LCS_Workbench_SideBrace_Origin.Placement ^ -1
FEATURE [App::Link] P_Workbench_SideBrace001  label="P_Workbench_SideBrace002"
  AttachedBy = #LCS_Workbench_SideBrace_Origin
  AttachedTo = P_Workbench_BackLeg#LCS_Workbench_BackLeg_TableHeight
  AttachmentOffset = pos=(-38.1,44.45,-44.45) rot=(0,0,1;0rad)
  LinkPlacement = pos=(552.45,-7.1e-15,679.45) rot=(0,0,1;0rad)
  LinkedObject = -> Part007
  Placement = pos=(552.45,-7.1e-15,679.45) rot=(0,0,1;0rad)
  SolverId = Asm4EE
  expr: Placement = P_Workbench_BackLeg.Placement * LCS_Workbench_BackLeg_TableHeight.Placement * AttachmentOffset * LCS_Workbench_SideBrace_Origin.Placement ^ -1
FEATURE [Sketcher::SketchObject] Sketch013  label="S_Workbench_Back_Base"
  FullyConstrained = true
  MapMode = 5
  Placement = pos=(0,0,0) rot=(1,0,0;1.5708rad)
  Support = -> [XZ_Plane018]
  expr: Constraints[10] = <<S_Workbench_Master>>.Constraints.BackHeight
  expr: Constraints[8] = <<S_Workbench_Master>>.Constraints.TableWidth
  sketch-geometry (4):
    g0: LineSegment StartX=-609.6 StartY=1219.2 StartZ=0 EndX=609.6 EndY=1219.2 EndZ=0
    g1: LineSegment StartX=609.6 StartY=1219.2 StartZ=0 EndX=609.6 EndY=0 EndZ=0
    g2: LineSegment StartX=609.6 StartY=0 StartZ=0 EndX=-609.6 EndY=0 EndZ=0
    g3: LineSegment StartX=-609.6 StartY=0 StartZ=0 EndX=-609.6 EndY=1219.2 EndZ=0
  constraints (11):
    c: Coincident(g0,g1)
    c: Coincident(g1,g2)
    c: Coincident(g2,g3)
    c: Coincident(g3,g0)
    c: Horizontal(g0)
    c: Horizontal(g2)
    c: Vertical(g1)
    c: Vertical(g3)
    c: DistanceX(g2,g2) = 1219.2
    c: Symmetric(g2,g1,g-1)
    c: DistanceY(g1,g1) = 1219.2
FEATURE [PartDesign::Pad] Pad009  label="PAD_Workbench_Back_Base"
  Direction = (0,-1,-2e-16)
  Length = 3.175
  Length2 = 10
  Placement = pos=(0,0,0) rot=(1,0,0;1.5708rad)
  Profile = -> Sketch013
  ReferenceAxis = -> Sketch013 [N_Axis]
  Type = 0
  expr: Length = <<S_Workbench_Master>>.Constraints.BackThickness
FEATURE [PartDesign::Body] Body008  label="B_Workbench_Back"
  Group = -> [Sketch013,Pad009]
  Origin = -> Origin018
  Tip = -> Pad009
FEATURE [PartDesign::CoordinateSystem] LCS_Workbench_Back_Origin
  AttacherType = Attacher::AttachEngine3D
FEATURE [PartDesign::CoordinateSystem] LCS_Workbench_Back_Top
  AttacherType = Attacher::AttachEngine3D
  Placement = pos=(0,0,1219.2) rot=(0,0,1;0rad)
  expr: .Placement.Base.z = <<S_Workbench_Master>>.Constraints.BackHeight
FEATURE [App::Part] Part008  label="P_Workbench_Back"
  Group = -> [Body008,LCS_Workbench_Back_Origin,LCS_Workbench_Back_Top]
  Origin = -> Origin017
FEATURE [App::Link] P_Workbench_Back  label="P_Workbench_Back001"
  AttachedBy = #LCS_Workbench_Back_Origin
  AttachedTo = Parent Assembly#LCS_Origin
  AttachmentOffset = pos=(0,3.175,762) rot=(0,0,1;0rad)
  LinkPlacement = pos=(0,3.175,762) rot=(0,0,1;0rad)
  LinkedObject = -> Part008
  Placement = pos=(0,3.175,762) rot=(0,0,1;0rad)
  SolverId = Asm4EE
  expr: .AttachmentOffset.Base.z = <<S_Workbench_Master>>.Constraints.BackLegHeight - 48 in
  expr: .Placement.Base.y = 1.875 in
  expr: Placement = LCS_Origin.Placement * AttachmentOffset * LCS_Workbench_Back_Origin.Placement ^ -1
FEATURE [Sketcher::SketchObject] Sketch014  label="S_Workbench_BackBrace_Body"
  FullyConstrained = true
  MapMode = 5
  Placement = pos=(0,0,0) rot=(0.57735,0.57735,0.57735;2.0944rad)
  Support = -> [YZ_Plane020]
  expr: Constraints[10] = Sketch009.Constraints.TwobyfourHeight
  expr: Constraints[9] = Sketch009.Constraints.TwobyfourWidth
  sketch-geometry (4):
    g0: LineSegment StartX=-19.05 StartY=44.45 StartZ=0 EndX=19.05 EndY=44.45 EndZ=0
    g1: LineSegment StartX=19.05 StartY=44.45 StartZ=0 EndX=19.05 EndY=-44.45 EndZ=0
    g2: LineSegment StartX=19.05 StartY=-44.45 StartZ=0 EndX=-19.05 EndY=-44.45 EndZ=0
    g3: LineSegment StartX=-19.05 StartY=-44.45 StartZ=0 EndX=-19.05 EndY=44.45 EndZ=0
  constraints (11):
    c: Coincident(g0,g1)
    c: Coincident(g1,g2)
    c: Coincident(g2,g3)
    c: Coincident(g3,g0)
    c: Horizontal(g0)
    c: Horizontal(g2)
    c: Vertical(g1)
    c: Vertical(g3)
    c: Symmetric(g0,g1,g-1)
    c: DistanceX(g0,g0) = 38.1
    c: DistanceY(g1,g1) = 88.9
FEATURE [PartDesign::Pad] Pad010  label="PAD_Workbench_BackBrace_Body"
  Direction = (1,-2e-16,3e-16)
  Length = 1066.8
  Length2 = 10
  Midplane = true
  Placement = pos=(0,0,0) rot=(1,1,1;2.0944rad)
  Profile = -> Sketch014
  ReferenceAxis = -> Sketch014 [N_Axis]
  Type = 0
  expr: Length = <<S_Workbench_Master>>.Constraints.TableWidth - 4 * Sketch009.Constraints.TwobyfourWidth
FEATURE [PartDesign::Body] Body009  label="B_Workbench_BackBrace"
  Group = -> [Sketch014,Pad010]
  Origin = -> Origin020
  Tip = -> Pad010
FEATURE [App::Link] P_Workbench_BackBrace  label="P_Workbench_BackBrace001"
  AttachedBy = #LCS_Workbench_BackBrace_Origin
  AttachedTo = P_Workbench_Top#LCS_Workbench_Top_Origin
  AttachmentOffset = pos=(0,-19.05,-44.45) rot=(0,0,1;0rad)
  LinkPlacement = pos=(0,-19.05,679.45) rot=(0,0,1;0rad)
  LinkedObject = -> Part009
  Placement = pos=(0,-19.05,679.45) rot=(0,0,1;0rad)
  SolverId = Asm4EE
  expr: Placement = P_Workbench_Top.Placement * LCS_Workbench_Top_Origin.Placement * AttachmentOffset * LCS_Workbench_BackBrace_Origin.Placement ^ -1
FEATURE [PartDesign::CoordinateSystem] LCS_Workbench_BackBrace_Origin
  AttacherType = Attacher::AttachEngine3D
FEATURE [App::Part] Part009  label="P_Workbench_BackBrace"
  Group = -> [Body009,LCS_Workbench_BackBrace_Origin]
  Origin = -> Origin019
FEATURE [Spreadsheet::Sheet] Spreadsheet
  cells = C2='Each; D2='Qty; E2='Subtotal; G2='Parts List; I2='Length; J2='Qty; K2='Total; A3='Table Top; B3='3/4 in Plywood; C3=40; D3=0.5; E3==.C3 * .D3; G3='Front Leg; H3='2x4; I3=28.25; J3=2; K3==I3 * J3; A4='Frames; B4='2x4x8; C4=3.73; D4=3; E4==.C4 * .D4; G4='Back Leg; H4='2x4; I4=78; J4=2; K4==I4 * J4; A5='Back; B5='1/8 in MDF; C5=14.48; D5=1; E5==.C5 * .D5; G5='Back Brace; H5='2x4; I5=66; J5=2; K5==I5 * J5; A12='Total; E12==.E3 + .E4 + .E5; A15='Cutting Guide; B15='2x4; C16=96; D16=2; E16='Front Leg(2); F16=28.25; G16='Back Brace(2); H16=66; C17=96; D17=2; E17='Back Leg(2); F17=78; C18=96; D18=2; E18='Side Brace(2 x 2); F18=60; B20='Total 2x4s; D20==D16 + D17 + D18; B22='3/4 in plywood; D22=1; E22='Table Top; F22='Shelf Braces; G22='Shelves; A25='Purchase Guide; A26='MDF; B26=13.98; A27='Plywood; B27=45.55; A28='2x4; B28=23.88; A29='Nuts; B29==5.79 / 4; A30='Bolts; B30==20.7 / 2; B31==B26 + B27 + B28 + B29 + B30
FEATURE [Sketcher::SketchObject] Sketch015  label="S_Workbench_ShelfBrace_Base"
  FullyConstrained = true
  MapMode = 5
  Placement = pos=(0,0,0) rot=(0.57735,0.57735,0.57735;2.0944rad)
  Support = -> [YZ_Plane022]
  expr: Constraints[6] = <<S_Workbench_Master>>.Constraints.ShelfDepth
  expr: Constraints[7] = <<S_Workbench_Master>>.Constraints.ShelfDepth / 2
  sketch-geometry (3):
    g0: LineSegment StartX=0 StartY=0 StartZ=0 EndX=0 EndY=-190.5 EndZ=0
    g1: LineSegment StartX=0 StartY=0 StartZ=0 EndX=-381 EndY=0 EndZ=0
    g2: LineSegment StartX=-381 StartY=0 StartZ=0 EndX=0 EndY=-190.5 EndZ=0
  constraints (8):
    c: Coincident(g0,g-1)
    c: PointOnObject(g0,g-2)
    c: Coincident(g1,g0)
    c: PointOnObject(g1,g-1)
    c: Coincident(g2,g1)
    c: Coincident(g2,g0)
    c: DistanceX(g1,g1) = 381
    c: DistanceY(g0,g0) = 190.5
FEATURE [PartDesign::Pad] Pad011  label="PAD_Workbench_ShelfBrace_Base"
  Direction = (1,-2e-16,3e-16)
  Length = 19.05
  Length2 = 10
  Placement = pos=(0,0,0) rot=(1,1,1;2.0944rad)
  Profile = -> Sketch015
  ReferenceAxis = -> Sketch015 [N_Axis]
  Type = 0
FEATURE [App::Link] P_Workbench_ShelfBrace  label="P_Workbench_ShelfBrace001"
  AttachedBy = #LCS_Workbench_ShelfBrace_Origin
  AttachedTo = P_Workbench_BackLeg001#LCS_Workbench_BackLeg_Shelf
  AttachmentOffset = pos=(19.05,44.45,0) rot=(0,0,1;0rad)
  LinkPlacement = pos=(-571.5,-7.1e-15,1524) rot=(0,0,1;0rad)
  LinkedObject = -> Part010
  Placement = pos=(-571.5,-7.1e-15,1524) rot=(0,0,1;0rad)
  SolverId = Asm4EE
  expr: Placement = P_Workbench_BackLeg001.Placement * LCS_Workbench_BackLeg_Shelf.Placement * AttachmentOffset * LCS_Workbench_ShelfBrace_Origin.Placement ^ -1
FEATURE [PartDesign::CoordinateSystem] LCS_Workbench_ShelfBrace_Origin
  AttacherType = Attacher::AttachEngine3D
FEATURE [App::Link] P_Workbench_ShelfBrace001  label="P_Workbench_ShelfBrace002"
  AttachedBy = #LCS_Workbench_ShelfBrace_Origin
  AttachedTo = P_Workbench_BackLeg001#LCS_Workbench_BackLeg_Shelf2
  AttachmentOffset = pos=(19.05,44.45,0) rot=(0,0,1;0rad)
  LinkPlacement = pos=(-571.5,0,1828.8) rot=(0,0,1;0rad)
  LinkedObject = -> Part010
  Placement = pos=(-571.5,0,1828.8) rot=(0,0,1;0rad)
  SolverId = Asm4EE
  expr: Placement = P_Workbench_BackLeg001.Placement * LCS_Workbench_BackLeg_Shelf2.Placement * AttachmentOffset * LCS_Workbench_ShelfBrace_Origin.Placement ^ -1
FEATURE [App::Link] P_Workbench_ShelfBrace002  label="P_Workbench_ShelfBrace003"
  AttachedBy = #LCS_Workbench_ShelfBrace_Origin
  AttachedTo = P_Workbench_BackLeg#LCS_Workbench_BackLeg_Shelf
  AttachmentOffset = pos=(-38.1,44.45,0) rot=(0,0,1;0rad)
  LinkPlacement = pos=(552.45,-7.1e-15,1524) rot=(0,0,1;0rad)
  LinkedObject = -> Part010
  Placement = pos=(552.45,-7.1e-15,1524) rot=(0,0,1;0rad)
  SolverId = Asm4EE
  expr: Placement = P_Workbench_BackLeg.Placement * LCS_Workbench_BackLeg_Shelf.Placement * AttachmentOffset * LCS_Workbench_ShelfBrace_Origin.Placement ^ -1
FEATURE [App::Link] P_Workbench_2
  AttachedBy = #LCS_Workbench_ShelfBrace_Origin
  AttachedTo = P_Workbench_BackLeg#LCS_Workbench_BackLeg_Shelf2
  AttachmentOffset = pos=(-38.1,44.45,0) rot=(0,0,1;0rad)
  LinkPlacement = pos=(552.45,-7.1e-15,1828.8) rot=(0,0,1;0rad)
  LinkedObject = -> Part010
  Placement = pos=(552.45,-7.1e-15,1828.8) rot=(0,0,1;0rad)
  SolverId = Asm4EE
  expr: Placement = P_Workbench_BackLeg.Placement * LCS_Workbench_BackLeg_Shelf2.Placement * AttachmentOffset * LCS_Workbench_ShelfBrace_Origin.Placement ^ -1
FEATURE [Sketcher::SketchObject] Sketch016  label="S_Workbench_AngleBrace_Base"
  FullyConstrained = false
  MapMode = 5
  Placement = pos=(0,0,0) rot=(0.57735,0.57735,0.57735;2.0944rad)
  Support = -> [YZ_Plane024]
  expr: Constraints[10] = <<S_Workbench_Master>>.Constraints.TableDepth
  sketch-geometry (5):
    g0: LineSegment StartX=-636.276 StartY=0 StartZ=0 EndX=0 EndY=-636.276 EndZ=0
    g1: LineSegment StartX=-762 StartY=0 StartZ=0 EndX=0 EndY=-762 EndZ=0
    g2: LineSegment StartX=-253.382 StartY=-382.895 StartZ=0 EndX=-316.243 EndY=-445.757 EndZ=0
    g3: LineSegment StartX=-762 StartY=0 StartZ=0 EndX=-636.276 EndY=0 EndZ=0
    g4: LineSegment StartX=0 StartY=-636.276 StartZ=0 EndX=0 EndY=-762 EndZ=0
  constraints (17):
    c: Vertical(g0,g-1)
    c: PointOnObject(g1,g-1)
    c: PointOnObject(g1,g-2)
    c: Parallel(g1,g0)
    c: Angle(g-2,g1) = 0.785398
    c: PointOnObject(g0,g-1)
    c: PointOnObject(g2,g0)
    c: PointOnObject(g2,g1)
    c: Perpendicular(g0,g2)
    c: Distance(g2) = 88.9
    c: DistanceX(g1,g-1) = 762
    c: Distance(g1) = 1077.63  'SideBraceLength'
    c: Coincident(g3,g1)
    c: Coincident(g3,g0)
    c: Coincident(g4,g0)
    c: Coincident(g4,g1)
    c: DistanceY(g1,g-1) = 762
FEATURE [PartDesign::Pad] Pad012  label="PAD_Workbench_AngleBrace_Base"
  Direction = (1,-2e-16,3e-16)
  Length = 38.1
  Length2 = 10
  Placement = pos=(0,0,0) rot=(1,1,1;2.0944rad)
  Profile = -> Sketch016
  ReferenceAxis = -> Sketch016 [N_Axis]
  Type = 0
FEATURE [PartDesign::CoordinateSystem] LCS_Workbench_AngleBrace_Origin
  AttacherType = Attacher::AttachEngine3D
FEATURE [Sketcher::SketchObject] Sketch017  label="S_Workbench_SideBrace_Holes"
  FullyConstrained = true
  MapMode = 5
  Placement = pos=(0,0,0) rot=(0.57735,0.57735,0.57735;2.0944rad)
  Support = -> [YZ_Plane016]
  expr: Constraints[17] = Sketch009.Constraints.TwobyfourHeight - 2 in
  expr: Constraints[18] = <<S_Workbench_Master>>.Constraints.TableDepth - 2 in
  expr: Constraints[7] = Sketch009.Constraints.BoltDiameter
  sketch-geometry (8):
    g0: Circle CenterX=-50.8 CenterY=19.05 CenterZ=0 NormalX=0 NormalY=0 NormalZ=1 AngleXU=0 Radius=3.175
    g1: Circle CenterX=-50.8 CenterY=-19.05 CenterZ=0 NormalX=0 NormalY=0 NormalZ=1 AngleXU=0 Radius=3.175
    g2: Circle CenterX=-711.2 CenterY=19.05 CenterZ=0 NormalX=0 NormalY=0 NormalZ=1 AngleXU=0 Radius=3.175
    g3: Circle CenterX=-711.2 CenterY=-19.05 CenterZ=0 NormalX=0 NormalY=0 NormalZ=1 AngleXU=0 Radius=3.175
    g4: LineSegment StartX=-711.2 StartY=-19.05 StartZ=0 EndX=-711.2 EndY=0 EndZ=0
    g5: LineSegment StartX=-711.2 StartY=0 StartZ=0 EndX=-711.2 EndY=19.05 EndZ=0
    g6: LineSegment StartX=-50.8 StartY=-19.05 StartZ=0 EndX=-50.8 EndY=0 EndZ=0
    g7: LineSegment StartX=-50.8 StartY=0 StartZ=0 EndX=-50.8 EndY=19.05 EndZ=0
  constraints (20):
    c: Coincident(g4,g3)
    c: PointOnObject(g4,g-1)
    c: Coincident(g5,g2)
    c: Tangent(g5,g4) = -1.5708
    c: Equal(g5,g4)
    c: Equal(g2,g3)
    c: Equal(g0,g1)
    c: Diameter(g0) = 6.35
    c: Coincident(g6,g1)
    c: PointOnObject(g6,g-1)
    c: Coincident(g0,g7)
    c: Tangent(g6,g7) = -1.5708
    c: Equal(g7,g6)
    c: Equal(g5,g7)
    c: DistanceX(g6,g-1) = 50.8
    c: Vertical(g5)
    c: Vertical(g7)
    c: DistanceY(g1,g0) = 38.1
    c: DistanceX(g4,g-1) = 711.2
    c: Equal(g3,g0)
FEATURE [PartDesign::Pocket] Pocket002  label="POCKET_Workbench_SideBrace_Holes"
  BaseFeature = -> Pad008
  Direction = (-1,2e-16,-3e-16)
  Length = 50.8
  Length2 = 5
  Midplane = true
  Placement = pos=(0,0,0) rot=(1,0,0;1.5708rad)
  Profile = -> Sketch017
  ReferenceAxis = -> Sketch017 [N_Axis]
  Type = 0
FEATURE [PartDesign::Body] Body007  label="B_Workbench_SideBrace"
  Group = -> [Sketch012,Pad008,Sketch017,Pocket002]
  Origin = -> Origin016
  Tip = -> Pocket002
FEATURE [App::Part] Part007  label="P_Workbench_SideBrace"
  Group = -> [Body007,LCS_Workbench_SideBrace_Origin]
  Origin = -> Origin015
FEATURE [Sketcher::SketchObject] Sketch018  label="S_Workbench_FrontLeg_Holes"
  FullyConstrained = true
  MapMode = 5
  Placement = pos=(0,0,0) rot=(0.57735,0.57735,0.57735;2.0944rad)
  Support = -> [YZ_Plane012]
  expr: Constraints[10] = Sketch009.Constraints.TwobyfourHeight - 2 in
  expr: Constraints[11] = Sketch009.Constraints.TwobyfourHeight
  expr: Constraints[1] = Sketch009.Constraints.BoltDiameter
  expr: Constraints[2] = Sketch009.Constraints.TwobyfourHeight - 2 in
  expr: Constraints[4] = <<S_Workbench_Master>>.Constraints.TableHeight - 1.75 in
  sketch-geometry (4):
    g0: Circle CenterX=6.35 CenterY=692.15 CenterZ=0 NormalX=0 NormalY=0 NormalZ=1 AngleXU=0 Radius=3.175
    g1: Circle CenterX=6.35 CenterY=654.05 CenterZ=0 NormalX=0 NormalY=0 NormalZ=1 AngleXU=0 Radius=3.175
    g2: Circle CenterX=6.35 CenterY=603.25 CenterZ=0 NormalX=0 NormalY=0 NormalZ=1 AngleXU=0 Radius=3.175
    g3: Circle CenterX=6.35 CenterY=565.15 CenterZ=0 NormalX=0 NormalY=0 NormalZ=1 AngleXU=0 Radius=3.175
  constraints (12):
    c: Equal(g0,g1)
    c: Diameter(g1) = 6.35
    c: DistanceY(g1,g0) = 38.1
    c: Vertical(g0,g1)
    c: DistanceY(g-1,g0) = 692.15
    c: DistanceX(g-1,g1) = 6.35
    c: Equal(g2,g1)
    c: Vertical(g3,g2)
    c: Vertical(g2,g1)
    c: Equal(g3,g2)
    c: DistanceY(g3,g2) = 38.1
    c: DistanceY(g2,g0) = 88.9
FEATURE [PartDesign::Pocket] Pocket003  label="POCKET_Workbench_FrontLeg_Holes"
  BaseFeature = -> Pad006
  Direction = (-1,2e-16,-3e-16)
  Length = 76.2
  Length2 = 5
  Midplane = true
  Profile = -> Sketch018
  ReferenceAxis = -> Sketch018 [N_Axis]
  Type = 0
  expr: Length = Sketch009.Constraints.TwobyfourWidth * 2
FEATURE [PartDesign::Body] Body005  label="B_Workbench_FrontLeg"
  Group = -> [Sketch008,Pad006,Sketch018,Pocket003]
  Origin = -> Origin012
  Tip = -> Pocket003
FEATURE [App::Part] Part005  label="P_Workbench_FrontLeg"
  Group = -> [Body005,LCS_Workbench_FrontLeg_Origin,LCS_Workbench_FrontLeg_Top]
  Origin = -> Origin011
FEATURE [Sketcher::SketchObject] Sketch019  label="S_Workbench_BackLeg_Holes"
  FullyConstrained = true
  MapMode = 5
  Placement = pos=(0,0,0) rot=(0.57735,0.57735,0.57735;2.0944rad)
  Support = -> [YZ_Plane010]
  expr: Constraints[15] = <<S_Workbench_Master>>.Constraints.ShelfHeight - 1 in
  expr: Constraints[16] = <<S_Workbench_Master>>.Constraints.ShelfHeight + <<S_Workbench_Master>>.Constraints.ShelfSpacing - 1 in
  expr: Constraints[22] = Sketch009.Constraints.TwobyfourHeight - 2 in
  expr: Constraints[23] = Sketch009.Constraints.TwobyfourHeight
  expr: Constraints[25] = <<S_Workbench_Master>>.Constraints.BackLegHeight
  expr: Constraints[2] = Sketch009.Constraints.BoltDiameter
  expr: Constraints[3] = <<S_Workbench_Master>>.Constraints.TableHeight - 1.75 in
  expr: Constraints[4] = Sketch009.Constraints.TwobyfourHeight - 2 in
  sketch-geometry (13):
    g0: Circle CenterX=-6.35 CenterY=692.15 CenterZ=0 NormalX=0 NormalY=0 NormalZ=1 AngleXU=0 Radius=3.175
    g1: Circle CenterX=-6.35 CenterY=654.05 CenterZ=0 NormalX=0 NormalY=0 NormalZ=1 AngleXU=0 Radius=3.175
    g2: Circle CenterX=-6.35 CenterY=1498.6 CenterZ=0 NormalX=0 NormalY=0 NormalZ=1 AngleXU=0 Radius=3.175
    g3: Circle CenterX=-6.35 CenterY=1422.4 CenterZ=0 NormalX=0 NormalY=0 NormalZ=1 AngleXU=0 Radius=3.175
    g4: Circle CenterX=-6.35 CenterY=1803.4 CenterZ=0 NormalX=0 NormalY=0 NormalZ=1 AngleXU=0 Radius=3.175
    g5: Circle CenterX=-6.35 CenterY=1727.2 CenterZ=0 NormalX=0 NormalY=0 NormalZ=1 AngleXU=0 Radius=3.175
    g6: Circle CenterX=-6.35 CenterY=603.25 CenterZ=0 NormalX=0 NormalY=0 NormalZ=1 AngleXU=0 Radius=3.175
    g7: Circle CenterX=-6.35 CenterY=565.15 CenterZ=0 NormalX=0 NormalY=0 NormalZ=1 AngleXU=0 Radius=3.175
    g8: GeomPoint X=0 Y=1981.2 Z=0
    g9: Circle CenterX=-6.35 CenterY=1879.6 CenterZ=0 NormalX=0 NormalY=0 NormalZ=1 AngleXU=0 Radius=3.175
    g10: Circle CenterX=-6.35 CenterY=1955.8 CenterZ=0 NormalX=0 NormalY=0 NormalZ=1 AngleXU=0 Radius=3.175
    g11: Circle CenterX=-6.35 CenterY=1651 CenterZ=0 NormalX=0 NormalY=0 NormalZ=1 AngleXU=0 Radius=3.175
    g12: Circle CenterX=-6.35 CenterY=1574.8 CenterZ=0 NormalX=0 NormalY=0 NormalZ=1 AngleXU=0 Radius=3.175
  constraints (41):
    c: Vertical(g1,g0)
    c: Equal(g0,g1)
    c: Diameter(g0) = 6.35
    c: DistanceY(g-1,g0) = 692.15
    c: DistanceY(g1,g0) = 38.1
    c: DistanceX(g0,g-1) = 6.35
    c: Vertical(g4,g5)
    c: Vertical(g5,g2)
    c: Vertical(g2,g3)
    c: Equal(g4,g5)
    c: Equal(g5,g2)
    c: Equal(g2,g3)
    c: Equal(g3,g0)
    c: DistanceY(g3,g2) = 76.2
    c: DistanceY(g5,g4) = 76.2
    c: DistanceY(g-1,g2) = 1498.6
    c: DistanceY(g-1,g4) = 1803.4
    c: Vertical(g0,g3)
    c: Equal(g7,g6)
    c: Vertical(g6,g7)
    c: Vertical(g7,g1)
    c: Equal(g7,g1)
    c: DistanceY(g7,g6) = 38.1
    c: DistanceY(g6,g0) = 88.9
    c: PointOnObject(g8,g-2)
    c: DistanceY(g-1,g8) = 1981.2
    c: DistanceY(g4,g8) = 177.8
    c: Vertical(g9,g10)
    c: Vertical(g10,g4)
    c: Equal(g9,g10)
    c: Equal(g10,g4)
    c: DistanceY(g4,g9) = 76.2
    c: DistanceY(g9,g10) = 76.2
    c: DistanceY(g10,g8) = 25.4
    c: Equal(g11,g12)
    c: Vertical(g5,g11)
    c: Vertical(g11,g12)
    c: DistanceY(g11,g5) = 76.2
    c: DistanceY(g12,g11) = 76.2
    c: DistanceY(g2,g12) = 76.2
    c: Equal(g11,g5)
FEATURE [PartDesign::Pocket] Pocket004  label="POCKET_Workbench_BackLeg_Holes"
  BaseFeature = -> Pad005
  Direction = (-1,2e-16,-3e-16)
  Length = 76.2
  Length2 = 5
  Midplane = true
  Profile = -> Sketch019
  ReferenceAxis = -> Sketch019 [N_Axis]
  Type = 0
  expr: Length = Sketch009.Constraints.TwobyfourWidth * 2
FEATURE [PartDesign::Body] Body004  label="B_Workbench_BackLeg"
  Group = -> [Sketch007,Pad005,Sketch019,Pocket004]
  Origin = -> Origin010
  Tip = -> Pocket004
FEATURE [App::Part] Part004  label="P_Workbench_BackLeg"
  Group = -> [Body004,LCS_BackLeg_Origin,LCS_Workbench_BackLeg_Top,LCS_Workbench_BackLeg_TableHeight,LCS_Workbench_BackLeg_Shelf,LCS_Workbench_BackLeg_Shelf2]
  Origin = -> Origin009
FEATURE [Sketcher::SketchObject] Sketch020  label="S_Workbench_ShelfBrace_Holes"
  FullyConstrained = true
  MapMode = 5
  Placement = pos=(0,0,0) rot=(0.57735,0.57735,0.57735;2.0944rad)
  Support = -> [YZ_Plane022]
  expr: Constraints[2] = <<S_Workbench_Master>>.Constraints.BoltDiameter
  expr: Constraints[3] = <<S_Workbench_Master>>.Constraints.TwobyfourHeight / 2 + 0.25 in
  sketch-geometry (2):
    g0: Circle CenterX=-50.8 CenterY=-25.4 CenterZ=0 NormalX=0 NormalY=0 NormalZ=1 AngleXU=0 Radius=3.175
    g1: Circle CenterX=-50.8 CenterY=-101.6 CenterZ=0 NormalX=0 NormalY=0 NormalZ=1 AngleXU=0 Radius=3.175
  constraints (6):
    c: Equal(g0,g1)
    c: Vertical(g0,g1)
    c: Diameter(g0) = 6.35
    c: DistanceX(g0,g-1) = 50.8
    c: DistanceY(g1,g0) = 76.2
    c: DistanceY(g0,g-1) = 25.4
FEATURE [PartDesign::Pocket] Pocket005  label="POCKET_Workbench_ShelfBrace_Holes"
  BaseFeature = -> Pad011
  Direction = (-1,2e-16,-3e-16)
  Length = 76.2
  Length2 = 5
  Placement = pos=(0,0,0) rot=(1,1,1;2.0944rad)
  Profile = -> Sketch020
  ReferenceAxis = -> Sketch020 [N_Axis]
  Reversed = true
  Type = 0
FEATURE [PartDesign::Body] Body010  label="B_Workbench_ShelfBrace"
  Group = -> [Sketch015,Pad011,Sketch020,Pocket005]
  Origin = -> Origin022
  Tip = -> Pocket005
FEATURE [App::Part] Part010  label="P_Workbench_ShelfBrace"
  Group = -> [Body010,LCS_Workbench_ShelfBrace_Origin]
  Origin = -> Origin021
FEATURE [Sketcher::SketchObject] Sketch021  label="S_Workbench_AngleBrace_Holes"
  FullyConstrained = true
  MapMode = 5
  Placement = pos=(0,0,0) rot=(0.57735,0.57735,0.57735;2.0944rad)
  Support = -> [YZ_Plane024]
  expr: Constraints[2] = <<S_Workbench_Master>>.Constraints.TableDepth - 2.5 in
  expr: Constraints[7] = 28 in - 1.25 in
  sketch-geometry (3):
    g0: Circle CenterX=-698.5 CenterY=-19.05 CenterZ=0 NormalX=0 NormalY=0 NormalZ=1 AngleXU=0 Radius=3.175
    g1: Circle CenterX=-50.8 CenterY=-628.65 CenterZ=0 NormalX=0 NormalY=0 NormalZ=1 AngleXU=0 Radius=3.175
    g2: Circle CenterX=-50.8 CenterY=-679.45 CenterZ=0 NormalX=0 NormalY=0 NormalZ=1 AngleXU=0 Radius=3.175
  constraints (9):
    c: Diameter(g0) = 6.35
    c: DistanceY(g0,g-1) = 19.05
    c: DistanceX(g0,g-1) = 698.5
    c: Equal(g2,g1)
    c: Equal(g1,g0)
    c: Vertical(g1,g2)
    c: DistanceY(g2,g1) = 50.8
    c: DistanceY(g2,g-1) = 679.45
    c: DistanceX(g1,g-1) = 50.8
FEATURE [PartDesign::Pocket] Pocket006  label="POCKET_Workbench_AngleBrace_Holes"
  BaseFeature = -> Pad012
  Direction = (-1,2e-16,-3e-16)
  Length = 76.2
  Length2 = 5
  Placement = pos=(0,0,0) rot=(1,1,1;2.0944rad)
  Profile = -> Sketch021
  ReferenceAxis = -> Sketch021 [N_Axis]
  Reversed = true
  Type = 0
FEATURE [PartDesign::Body] Body011  label="B_Workbench_AngleBrace"
  Group = -> [Sketch016,Pad012,Sketch021,Pocket006]
  Origin = -> Origin024
  Tip = -> Pocket006
FEATURE [App::Part] Part011  label="P_Workbench_AngleBrace"
  Group = -> [Body011,LCS_Workbench_AngleBrace_Origin]
  Origin = -> Origin023
FEATURE [App::Link] P_Workbench_SideBrace002  label="P_Workbench_SideBrace003"
  AttachedBy = #LCS_Workbench_SideBrace_Origin
  AttachedTo = P_Workbench_Top#LCS_Workbench_Top_Back_Left_Leg
  AttachmentOffset = pos=(38.1,44.45,-133.35) rot=(0,0,1;0rad)
  LinkPlacement = pos=(-552.45,-7.1e-15,590.55) rot=(0,0,1;0rad)
  LinkedObject = -> Part007
  Placement = pos=(-552.45,-7.1e-15,590.55) rot=(0,0,1;0rad)
  SolverId = Asm4EE
  expr: Placement = P_Workbench_Top.Placement * LCS_Workbench_Top_Back_Left_Leg.Placement * AttachmentOffset * LCS_Workbench_SideBrace_Origin.Placement ^ -1
FEATURE [App::Link] P_Workbench_3
  AttachedBy = #LCS_Workbench_SideBrace_Origin
  AttachedTo = P_Workbench_Top#LCS_Workbench_Top_Back_Right_Leg
  AttachmentOffset = pos=(-38.1,44.45,-133.35) rot=(0,0,1;0rad)
  LinkPlacement = pos=(552.45,-7.1e-15,590.55) rot=(0,0,1;0rad)
  LinkedObject = -> Part007
  Placement = pos=(552.45,-7.1e-15,590.55) rot=(0,0,1;0rad)
  SolverId = Asm4EE
  expr: Placement = P_Workbench_Top.Placement * LCS_Workbench_Top_Back_Right_Leg.Placement * AttachmentOffset * LCS_Workbench_SideBrace_Origin.Placement ^ -1
FEATURE [App::Part] Assembly
  AssemblyType = Part::Link
  Group = -> [LCS_Origin,Constraints,Variables,Configurations,P_Workbench_BackLeg,P_Workbench_BackLeg001,P_Workbench_Top,P_Workbench_FrontLeg,P_Workbench_1,P_Workbench_Shelf,P_Workbench_Shelf001,P_Workbench_SideBrace,P_Workbench_SideBrace001,P_Workbench_Back,P_Workbench_BackBrace,P_Workbench_ShelfBrace,P_Workbench_ShelfBrace001,P_Workbench_ShelfBrace002,P_Workbench_2,P_Workbench_SideBrace002,P_Workbench_3]
  Origin = -> Origin008
  Type = Assembly
FEATURE [Sketcher::SketchObject] Sketch022  label="S_Workbench_FrontLeg_Template_Holes"
  FullyConstrained = true
  MapMode = 5
  Support = -> [XY_Plane026]
  expr: Constraints[10] = <<S_Workbench_Master>>.Constraints.TwobyfourHeight
  expr: Constraints[9] = 1 mm
  sketch-geometry (4):
    g0: Circle CenterX=6.35 CenterY=63.5 CenterZ=0 NormalX=0 NormalY=0 NormalZ=1 AngleXU=0 Radius=0.5
    g1: Circle CenterX=6.35 CenterY=25.4 CenterZ=0 NormalX=0 NormalY=0 NormalZ=1 AngleXU=0 Radius=0.5
    g2: Circle CenterX=6.35 CenterY=152.4 CenterZ=0 NormalX=0 NormalY=0 NormalZ=1 AngleXU=0 Radius=0.5
    g3: Circle CenterX=6.35 CenterY=114.3 CenterZ=0 NormalX=0 NormalY=0 NormalZ=1 AngleXU=0 Radius=0.5
  constraints (12):
    c: Equal(g0,g1)
    c: Equal(g1,g2)
    c: Equal(g2,g3)
    c: Vertical(g0,g1)
    c: Vertical(g1,g2)
    c: Vertical(g2,g3)
    c: DistanceX(g-1,g3) = 6.35
    c: DistanceY(g3,g2) = 38.1
    c: DistanceY(g1,g0) = 38.1
    c: Diameter(g2) = 1
    c: DistanceY(g0,g2) = 88.9
    c: DistanceY(g-1,g1) = 25.4
FEATURE [Sketcher::SketchObject] Sketch023  label="S_Workbench_FrontLeg_Template_Body"
  FullyConstrained = true
  MapMode = 5
  Support = -> [XY_Plane026]
  expr: Constraints[8] = <<S_Workbench_Master>>.Constraints.TwobyfourHeight / 2
  sketch-geometry (4):
    g0: LineSegment StartX=0 StartY=177.8 StartZ=0 EndX=44.45 EndY=177.8 EndZ=0
    g1: LineSegment StartX=44.45 StartY=177.8 StartZ=0 EndX=44.45 EndY=0 EndZ=0
    g2: LineSegment StartX=44.45 StartY=0 StartZ=0 EndX=0 EndY=0 EndZ=0
    g3: LineSegment StartX=0 StartY=0 StartZ=0 EndX=0 EndY=177.8 EndZ=0
  constraints (11):
    c: Coincident(g0,g1)
    c: Coincident(g1,g2)
    c: Coincident(g2,g3)
    c: Coincident(g3,g0)
    c: Horizontal(g0)
    c: Horizontal(g2)
    c: Vertical(g1)
    c: Vertical(g3)
    c: DistanceX(g2,g2) = 44.45
    c: DistanceY(g1,g1) = 177.8
    c: Coincident(g2,g-1)
FEATURE [PartDesign::Pad] Pad013  label="PAD_Workbench_FrontLeg_Template_Body"
  Direction = (0,0,1)
  Length = 2
  Length2 = 10
  Profile = -> Sketch023
  ReferenceAxis = -> Sketch023 [N_Axis]
  Type = 0
  expr: Length = 2 mm
FEATURE [Sketcher::SketchObject] Sketch024  label="S_Workbench_FrontLeg_Template_Alignment"
  FullyConstrained = true
  MapMode = 5
  Support = -> [XY_Plane026]
  expr: Constraints[15] = <<S_Workbench_Master>>.Constraints.TwobyfourHeight / 2
  expr: Constraints[16] = <<S_Workbench_Master>>.Constraints.TwobyfourHeight / 2
  sketch-geometry (6):
    g0: LineSegment StartX=0 StartY=177.8 StartZ=0 EndX=0 EndY=184.15 EndZ=0
    g1: LineSegment StartX=0 StartY=184.15 StartZ=0 EndX=50.8 EndY=184.15 EndZ=0
    g2: LineSegment StartX=50.8 StartY=184.15 StartZ=0 EndX=50.8 EndY=0 EndZ=0
    g3: LineSegment StartX=50.8 StartY=0 StartZ=0 EndX=44.45 EndY=0 EndZ=0
    g4: LineSegment StartX=44.45 StartY=0 StartZ=0 EndX=44.45 EndY=177.8 EndZ=0
    g5: LineSegment StartX=0 StartY=177.8 StartZ=0 EndX=44.45 EndY=177.8 EndZ=0
  constraints (18):
    c: Coincident(g0,g1)
    c: Horizontal(g1)
    c: Vertical(g0)
    c: Coincident(g2,g3)
    c: Coincident(g3,g4)
    c: Vertical(g2)
    c: Vertical(g4)
    c: DistanceX(g3,g3) = 6.35
    c: Coincident(g5,g0)
    c: Coincident(g5,g4)
    c: Horizontal(g5)
    c: Coincident(g1,g2)
    c: DistanceY(g4,g4) = 177.8
    c: Horizontal(g3)
    c: Horizontal(g3,g-1)
    c: DistanceX(g-1,g3) = 44.45
    c: DistanceX(g5,g5) = 44.45
    c: Equal(g0,g3)
FEATURE [PartDesign::Pad] Pad014  label="PAD_Workbench_FrontLeg_Template_Alignment"
  BaseFeature = -> Pad013
  Direction = (0,0,1)
  Length = 8
  Length2 = 10
  Profile = -> Sketch024
  ReferenceAxis = -> Sketch024 [N_Axis]
  Type = 0
  expr: Length = 8 mm
FEATURE [PartDesign::Pocket] Pocket007  label="POCKET_Workbench_FrontLeg_Template_Holes"
  BaseFeature = -> Pad014
  Direction = (0,0,-1)
  Length = 12.7
  Length2 = 5
  Profile = -> Sketch022
  ReferenceAxis = -> Sketch022 [N_Axis]
  Reversed = true
  Type = 0
FEATURE [Sketcher::SketchObject] Sketch025  label="S_Workbench_SideBrace_Template_Left_Base"
  FullyConstrained = true
  MapMode = 5
  Support = -> [XY_Plane028]
  expr: Constraints[10] = <<S_Workbench_Master>>.Constraints.TwobyfourHeight
  sketch-geometry (4):
    g0: LineSegment StartX=0 StartY=0 StartZ=0 EndX=-63.5 EndY=0 EndZ=0
    g1: LineSegment StartX=-63.5 StartY=0 StartZ=0 EndX=-63.5 EndY=88.9 EndZ=0
    g2: LineSegment StartX=-63.5 StartY=88.9 StartZ=0 EndX=0 EndY=88.9 EndZ=0
    g3: LineSegment StartX=0 StartY=88.9 StartZ=0 EndX=0 EndY=0 EndZ=0
  constraints (11):
    c: Coincident(g0,g1)
    c: Coincident(g1,g2)
    c: Coincident(g2,g3)
    c: Coincident(g3,g0)
    c: Horizontal(g0)
    c: Horizontal(g2)
    c: Vertical(g1)
    c: Vertical(g3)
    c: Coincident(g0,g-1)
    c: DistanceX(g2,g2) = 63.5
    c: DistanceY(g3,g3) = 88.9
FEATURE [PartDesign::Pad] Pad015  label="PAD_Workbench_SideBrace_Template_Base_Left"
  Direction = (0,0,1)
  Length = 2
  Length2 = 10
  Profile = -> Sketch025
  ReferenceAxis = -> Sketch025 [N_Axis]
  Type = 0
  expr: Length = 2 mm
FEATURE [Sketcher::SketchObject] Sketch026  label="S_Workbench_SideBrace_Template_Left_Holes"
  FullyConstrained = true
  MapMode = 5
  Support = -> [XY_Plane028]
  expr: Constraints[0] = Sketch009.Constraints.TwobyfourHeight - 2 in
  expr: Constraints[4] = 1 mm
  sketch-geometry (2):
    g0: Circle CenterX=-50.8 CenterY=63.5 CenterZ=0 NormalX=0 NormalY=0 NormalZ=1 AngleXU=0 Radius=0.5
    g1: Circle CenterX=-50.8 CenterY=25.4 CenterZ=0 NormalX=0 NormalY=0 NormalZ=1 AngleXU=0 Radius=0.5
  constraints (6):
    c: DistanceY(g1,g0) = 38.1
    c: Vertical(g0,g1)
    c: DistanceX(g1,g-1) = 50.8
    c: Equal(g0,g1)
    c: Diameter(g0) = 1
    c: DistanceY(g-1,g1) = 25.4
FEATURE [PartDesign::Pocket] Pocket008  label="POCKET_Workbench_SideBrace_Template_Left_Holes"
  BaseFeature = -> Pad015
  Direction = (0,0,-1)
  Length = 5
  Length2 = 5
  Profile = -> Sketch026
  ReferenceAxis = -> Sketch026 [N_Axis]
  Reversed = true
  Type = 1
FEATURE [Sketcher::SketchObject] Sketch027  label="S_Workbench_SideBrace_Template_Left_Alignment"
  FullyConstrained = true
  MapMode = 5
  Support = -> [XY_Plane028]
  sketch-geometry (6):
    g0: LineSegment StartX=6.35 StartY=0 StartZ=0 EndX=6.35 EndY=95.25 EndZ=0
    g1: LineSegment StartX=0 StartY=88.9 StartZ=0 EndX=0 EndY=0 EndZ=0
    g2: LineSegment StartX=0 StartY=0 StartZ=0 EndX=6.35 EndY=0 EndZ=0
    g3: LineSegment StartX=-63.5 StartY=88.9 StartZ=0 EndX=0 EndY=88.9 EndZ=0
    g4: LineSegment StartX=-63.5 StartY=88.9 StartZ=0 EndX=-63.5 EndY=95.25 EndZ=0
    g5: LineSegment StartX=-63.5 StartY=95.25 StartZ=0 EndX=6.35 EndY=95.25 EndZ=0
  constraints (17):
    c: PointOnObject(g1,g-2)
    c: Vertical(g0)
    c: DistanceX(g-1,g0) = 6.35
    c: Horizontal(g0,g1)
    c: Coincident(g2,g1)
    c: Coincident(g2,g0)
    c: Coincident(g1,g-1)
    c: Coincident(g3,g1)
    c: Horizontal(g3)
    c: DistanceY(g1,g1) = 88.9
    c: Coincident(g4,g3)
    c: Coincident(g5,g0)
    c: Horizontal(g5)
    c: Vertical(g4)
    c: Equal(g4,g2)
    c: Coincident(g4,g5)
    c: DistanceX(g3,g3) = 63.5
FEATURE [PartDesign::Pad] Pad016  label="PAD_Workbench_SideBrace_Template_Left_Alignment"
  BaseFeature = -> Pocket008
  Direction = (0,0,1)
  Length = 8
  Length2 = 10
  Profile = -> Sketch027
  ReferenceAxis = -> Sketch027 [N_Axis]
  Type = 0
  expr: Length = 8 mm
FEATURE [Sketcher::SketchObject] Sketch028  label="S_Workbench_BackShelf_Template_Base"
  FullyConstrained = true
  MapMode = 5
  Support = -> [XY_Plane030]
  sketch-geometry (4):
    g0: LineSegment StartX=0 StartY=127 StartZ=0 EndX=101.6 EndY=127 EndZ=0
    g1: LineSegment StartX=101.6 StartY=127 StartZ=0 EndX=101.6 EndY=0 EndZ=0
    g2: LineSegment StartX=101.6 StartY=0 StartZ=0 EndX=0 EndY=0 EndZ=0
    g3: LineSegment StartX=0 StartY=0 StartZ=0 EndX=0 EndY=127 EndZ=0
  constraints (12):
    c: Coincident(g0,g1)
    c: Coincident(g1,g2)
    c: Coincident(g2,g3)
    c: Coincident(g3,g0)
    c: Horizontal(g0)
    c: Horizontal(g2)
    c: Vertical(g1)
    c: Vertical(g3)
    c: PointOnObject(g0,g-2)
    c: PointOnObject(g1,g-1)
    c: DistanceY(g1,g1) = 127
    c: DistanceX(g0,g0) = 101.6
FEATURE [PartDesign::Pad] Pad017  label="PAD_Workbench_BackShelf_Template_Base"
  Direction = (0,0,1)
  Length = 2
  Length2 = 10
  Profile = -> Sketch028
  ReferenceAxis = -> Sketch028 [N_Axis]
  Type = 0
  expr: Length = 2 mm
FEATURE [Sketcher::SketchObject] Sketch029  label="S_Workbench_BackShelf_Template_Holes"
  FullyConstrained = true
  MapMode = 5
  Support = -> [XY_Plane030]
  expr: Constraints[2] = 1 mm
  sketch-geometry (3):
    g0: Circle CenterX=50.8 CenterY=114.3 CenterZ=0 NormalX=0 NormalY=0 NormalZ=1 AngleXU=0 Radius=0.5
    g1: Circle CenterX=50.8 CenterY=38.1 CenterZ=0 NormalX=0 NormalY=0 NormalZ=1 AngleXU=0 Radius=0.5
    g2: GeomPoint X=50.8 Y=127 Z=0
  constraints (8):
    c: Vertical(g0,g1)
    c: Equal(g0,g1)
    c: Diameter(g0) = 1
    c: DistanceY(g1,g0) = 76.2
    c: DistanceX(g-1,g1) = 50.8
    c: Vertical(g2,g0)
    c: DistanceY(g-1,g2) = 127
    c: DistanceY(g0,g2) = 12.7
FEATURE [PartDesign::Pocket] Pocket009  label="POCKET_Workbench_BackShelf_Template_Holes"
  BaseFeature = -> Pad017
  Direction = (0,0,-1)
  Length = 5.0038
  Length2 = 5
  Profile = -> Sketch029
  ReferenceAxis = -> Sketch029 [N_Axis]
  Reversed = true
  Type = 0
FEATURE [Sketcher::SketchObject] Sketch030  label="S_Workbench_BackShelf_Template_Alignment"
  FullyConstrained = true
  MapMode = 5
  Support = -> [XY_Plane030]
  sketch-geometry (4):
    g0: LineSegment StartX=107.95 StartY=127 StartZ=0 EndX=101.6 EndY=127 EndZ=0
    g1: LineSegment StartX=101.6 StartY=127 StartZ=0 EndX=101.6 EndY=0 EndZ=0
    g2: LineSegment StartX=101.6 StartY=0 StartZ=0 EndX=107.95 EndY=0 EndZ=0
    g3: LineSegment StartX=107.95 StartY=0 StartZ=0 EndX=107.95 EndY=127 EndZ=0
  constraints (12):
    c: Coincident(g0,g1)
    c: Coincident(g1,g2)
    c: Coincident(g2,g3)
    c: Coincident(g3,g0)
    c: Horizontal(g0)
    c: Horizontal(g2)
    c: Vertical(g1)
    c: Vertical(g3)
    c: PointOnObject(g1,g-1)
    c: DistanceX(g2,g2) = 6.35
    c: DistanceY(g3,g3) = 127
    c: DistanceX(g-1,g1) = 101.6
FEATURE [PartDesign::Pad] Pad018  label="PAD_Workbench_BackShelf_Template_Alignment"
  BaseFeature = -> Pocket009
  Direction = (0,0,1)
  Length = 8
  Length2 = 10
  Profile = -> Sketch030
  ReferenceAxis = -> Sketch030 [N_Axis]
  Type = 0
  expr: Length = 8 mm
FEATURE [Sketcher::SketchObject] Sketch031  label="S_Workbench_ShelfBrace_Template_Base"
  FullyConstrained = true
  MapMode = 5
  Support = -> [XY_Plane032]
  expr: Constraints[10] = <<S_Workbench_Master>>.Constraints.ShelfDepth
  expr: Constraints[1] = <<S_Workbench_Master>>.Constraints.ShelfDepth / 2
  sketch-geometry (7):
    g0: LineSegment StartX=0 StartY=-190.5 StartZ=0 EndX=0 EndY=0 EndZ=0
    g1: LineSegment StartX=0 StartY=0 StartZ=0 EndX=-76.2 EndY=0 EndZ=0
    g2: GeomPoint X=-381 Y=0 Z=0
    g3: LineSegment StartX=-381 StartY=0 StartZ=0 EndX=-76.2 EndY=0 EndZ=0
    g4: LineSegment StartX=-381 StartY=0 StartZ=0 EndX=-76.2 EndY=-152.4 EndZ=0
    g5: LineSegment StartX=-76.2 StartY=-152.4 StartZ=0 EndX=0 EndY=-190.5 EndZ=0
    g6: LineSegment StartX=-76.2 StartY=0 StartZ=0 EndX=-76.2 EndY=-152.4 EndZ=0
  constraints (16):
    c: PointOnObject(g0,g-2)
    c: DistanceY(g0,g0) = 190.5
    c: Coincident(g1,g0)
    c: PointOnObject(g1,g-1)
    c: PointOnObject(g2,g-1)
    c: Coincident(g3,g2)
    c: Coincident(g3,g1)
    c: Coincident(g4,g3)
    c: Coincident(g5,g0)
    c: Tangent(g5,g4) = -1.5708
    c: DistanceX(g3,g0) = 381
    c: Coincident(g0,g-1)
    c: Coincident(g6,g1)
    c: Coincident(g6,g4)
    c: Vertical(g6)
    c: DistanceX(g1,g0) = 76.2
FEATURE [PartDesign::Pad] Pad019  label="PAD_Workbench_ShelfBrace_Template_Base"
  Direction = (0,0,1)
  Length = 2
  Length2 = 10
  Profile = -> Sketch031
  ReferenceAxis = -> Sketch031 [N_Axis]
  Type = 0
FEATURE [Sketcher::SketchObject] Sketch032  label="S_Workbench_ShelfBrace_Template_Holes"
  FullyConstrained = true
  MapMode = 5
  Support = -> [XY_Plane032]
  expr: Constraints[1] = 1 mm
  sketch-geometry (2):
    g0: Circle CenterX=-50.8 CenterY=-25.4 CenterZ=0 NormalX=0 NormalY=0 NormalZ=1 AngleXU=0 Radius=0.5
    g1: Circle CenterX=-50.8 CenterY=-101.6 CenterZ=0 NormalX=0 NormalY=0 NormalZ=1 AngleXU=0 Radius=0.5
  constraints (6):
    c: Equal(g1,g0)
    c: Diameter(g0) = 1
    c: Vertical(g0,g1)
    c: DistanceY(g1,g0) = 76.2
    c: DistanceX(g0,g-1) = 50.8
    c: DistanceY(g0,g-1) = 25.4
FEATURE [PartDesign::Pocket] Pocket010  label="POCKET_Workbench_ShelfBrace_Template_Holes"
  BaseFeature = -> Pad019
  Direction = (0,0,-1)
  Length = 5
  Length2 = 5
  Profile = -> Sketch032
  ReferenceAxis = -> Sketch032 [N_Axis]
  Reversed = true
  Type = 1
FEATURE [Sketcher::SketchObject] Sketch033  label="S_Workbench_ShelfBrace_Template_Alignment"
  FullyConstrained = true
  MapMode = 5
  Support = -> [XY_Plane032]
  expr: Constraints[13] = <<S_Workbench_Master>>.Constraints.ShelfDepth / 2
  sketch-geometry (6):
    g0: LineSegment StartX=-76.2 StartY=0 StartZ=0 EndX=-76.2 EndY=6.35 EndZ=0
    g1: LineSegment StartX=-76.2 StartY=6.35 StartZ=0 EndX=6.35 EndY=6.35 EndZ=0
    g2: LineSegment StartX=6.35 StartY=6.35 StartZ=0 EndX=6.35 EndY=-190.5 EndZ=0
    g3: LineSegment StartX=6.35 StartY=-190.5 StartZ=0 EndX=0 EndY=-190.5 EndZ=0
    g4: LineSegment StartX=0 StartY=-190.5 StartZ=0 EndX=0 EndY=0 EndZ=0
    g5: LineSegment StartX=0 StartY=0 StartZ=0 EndX=-76.2 EndY=0 EndZ=0
  constraints (17):
    c: PointOnObject(g0,g-1)
    c: Vertical(g0)
    c: Coincident(g0,g1)
    c: Horizontal(g1)
    c: Coincident(g2,g1)
    c: Vertical(g2)
    c: PointOnObject(g3,g-2)
    c: Coincident(g4,g3)
    c: Coincident(g4,g-1)
    c: Coincident(g5,g4)
    c: Coincident(g5,g0)
    c: Coincident(g3,g2)
    c: Horizontal(g3)
    c: DistanceY(g4,g4) = 190.5
    c: DistanceX(g5,g5) = 76.2
    c: Equal(g3,g0)
    c: DistanceY(g0,g0) = 6.35
FEATURE [PartDesign::Pad] Pad020  label="PAD_Workbench_ShelfBrace_Template_Alignment"
  BaseFeature = -> Pocket010
  Direction = (0,0,1)
  Length = 8
  Length2 = 10
  Profile = -> Sketch033
  ReferenceAxis = -> Sketch033 [N_Axis]
  Type = 0
  expr: Length = 8 mm
FEATURE [TechDraw::DrawSVGTemplate] Template  label="TEMPLATE_Step11_FullyAssembled"
  EditableTexts = Code=JWB; CompanyAddress=1234 Main St; CompanyName=Ensor Robotics; DrawingNumber=11-1-FullyAssembled; DrawingTitle1=Assembled View; DrawingTitle2=Fully assembled workbench; DrawnBy=Jon A.; Revision=v1; Scale=1:16; Sheet=Sheet 11 of 11
  Height = 215.9
  Orientation = 1
  Template = /snap/freecad/908/usr/share/Mod/TechDraw/Templates/USLetter_Landscape.svg
  Width = 279.4
FEATURE [Part::Part2DObjectPython] ShapeString  label="TEXT_Workbench_ShelfBrace_Template_Label"  # Draft 2D object (typed FeaturePython)
  FontFile = <path>
  MakeFace = true
  Placement = pos=(-1.9812,-57.7088,-1e-15) rot=(0,1,0;3.14159rad)
  Size = 10.0076
  String = Shelf Brace
  Tracking = 0
FEATURE [PartDesign::Pocket] Pocket011  label="POCKET_Workbench_ShelfBrace_Template_Label"
  BaseFeature = -> Pad020
  Direction = (0,0,1)
  Length = 1
  Length2 = 5
  Profile = -> ShapeString
  ReferenceAxis = -> ShapeString [N_Axis]
  Type = 0
  expr: Length = 1 mm
FEATURE [PartDesign::Body] Body015  label="B_Workbench_ShelfBrace_Template"
  Group = -> [Sketch031,Pad019,Sketch032,Pocket010,Sketch033,Pad020,ShapeString,Pocket011]
  Origin = -> Origin032
  Tip = -> Pocket011
FEATURE [App::Part] Part015  label="P_Workbench_ShelfBrace_Template"
  Group = -> [Body015]
  Origin = -> Origin031
FEATURE [Part::Part2DObjectPython] ShapeString001  label="TEXT_Workbench_BackShelf_Template_Label0"  # Draft 2D object (typed FeaturePython)
  FontFile = <path>
  MakeFace = true
  Placement = pos=(84.201,86.1822,1e-14) rot=(0,1,0;3.14159rad)
  Size = 10.0076
  String = Back Leg
  Tracking = 0
FEATURE [PartDesign::Pocket] Pocket012  label="POCKET_Workbench_BackShelf_Template_Label0"
  BaseFeature = -> Pad018
  Direction = (0,0,1)
  Length = 1
  Length2 = 5
  Profile = -> ShapeString001
  ReferenceAxis = -> ShapeString001 [N_Axis]
  Type = 0
  expr: Length = 1 mm
FEATURE [Part::Part2DObjectPython] ShapeString002  label="TEXT_Workbench_BackShelf_Template_Label1"  # Draft 2D object (typed FeaturePython)
  FontFile = <path>
  MakeFace = true
  Placement = pos=(84.201,75.2856,1e-14) rot=(0,1,0;3.14159rad)
  Size = 10.0076
  String = Shelf Holes
  Tracking = 0
FEATURE [PartDesign::Pocket] Pocket013  label="POCKET_Workbench_BackShelf_Template_Label1"
  BaseFeature = -> Pocket012
  Direction = (0,0,1)
  Length = 1
  Length2 = 5
  Profile = -> ShapeString002
  ReferenceAxis = -> ShapeString002 [N_Axis]
  Type = 0
  expr: Length = 1 mm
FEATURE [PartDesign::Body] Body014  label="B_Workbench_BackShelf_Template"
  Group = -> [Sketch028,Pad017,Sketch029,Pocket009,Sketch030,Pad018,ShapeString001,Pocket012,ShapeString002,Pocket013]
  Origin = -> Origin030
  Tip = -> Pocket013
FEATURE [App::Part] Part014  label="P_Workbench_BackShelf_Template"
  Group = -> [Body014]
  Origin = -> Origin029
FEATURE [Part::Part2DObjectPython] ShapeString005  label="TEXT_Workbench_FrontLeg_Template_Label0"  # Draft 2D object (typed FeaturePython)
  FontFile = <userpath>/3dPrinting/workshop/OpenSans-Bold.ttf
  MakeFace = true
  Placement = pos=(40.0304,140.106,-0.254) rot=(0,1,0;3.14159rad)
  Size = 10.0076
  String = Front
  Tracking = 0
FEATURE [PartDesign::Pocket] Pocket016  label="POCKET_Workbench_FrontLeg_Template_Label0"
  BaseFeature = -> Pocket007
  Direction = (-2.98023e-07,-3.95e-14,1)
  Length = 1
  Length2 = 5
  Profile = -> ShapeString005
  ReferenceAxis = -> ShapeString005 [N_Axis]
  Type = 0
  expr: Length = 1 mm
FEATURE [Part::Part2DObjectPython] ShapeString006  label="TEXT_Workbench_FrontLeg_Template_Label1"  # Draft 2D object (typed FeaturePython)
  FontFile = <userpath>/3dPrinting/workshop/OpenSans-Bold.ttf
  MakeFace = true
  Placement = pos=(39.6494,124.206,0) rot=(0,1,0;3.14159rad)
  Size = 10.0076
  String = Leg
  Tracking = 0
FEATURE [PartDesign::Pocket] Pocket017  label="POCKET_Workbench_FrontLeg_Template_Label1"
  BaseFeature = -> Pocket016
  Direction = (0,0,1)
  Length = 1
  Length2 = 5
  Profile = -> ShapeString006
  ReferenceAxis = -> ShapeString006 [N_Axis]
  Type = 0
  expr: Length = 1 mm
FEATURE [PartDesign::Body] Body012  label="B_Workbench_FrontLeg_Template"
  Group = -> [Sketch022,Sketch023,Pad013,Sketch024,Pad014,Pocket007,ShapeString005,Pocket016,ShapeString006,Pocket017]
  Origin = -> Origin026
  Tip = -> Pocket017
FEATURE [App::Part] Part012  label="P_Workbench_FrontLeg_Template"
  Group = -> [Body012]
  Origin = -> Origin025
FEATURE [Part::Part2DObjectPython] ShapeString007  label="TEXT_Workbench_SideBrace_Template_Left_SideBrace"  # Draft 2D object (typed FeaturePython)
  FontFile = <userpath>/3dPrinting/workshop/OpenSans-Bold.ttf
  MakeFace = true
  Placement = pos=(-3.72384e-06,42.5958,0) rot=(0,1,0;3.14159rad)
  Size = 10.0076
  String = Side Brace
  Tracking = 0
FEATURE [PartDesign::Pocket] Pocket018  label="POCKET_Workbench_SideBrace_Template_Left_SideBrace"
  BaseFeature = -> Pad016
  Direction = (0,0,1)
  Length = 1
  Length2 = 5
  Profile = -> ShapeString007
  ReferenceAxis = -> ShapeString007 [N_Axis]
  Type = 0
  expr: Length = 1 mm
FEATURE [Part::Part2DObjectPython] ShapeString008  label="TEXT_Workbench_SideBrace_Template_Left_Left"  # Draft 2D object (typed FeaturePython)
  FontFile = <userpath>/3dPrinting/workshop/OpenSans-Bold.ttf
  MakeFace = true
  Placement = pos=(-2.68463e-06,30.7086,0) rot=(0,1,0;3.14159rad)
  Size = 10.0076
  String = Left
  Tracking = 0
FEATURE [PartDesign::Pocket] Pocket019  label="POCKET_Workbench_SideBrace_Template_Left_Left"
  BaseFeature = -> Pocket018
  Direction = (0,0,1)
  Length = 1
  Length2 = 5
  Profile = -> ShapeString008
  ReferenceAxis = -> ShapeString008 [N_Axis]
  Type = 0
  expr: Length = 1 mm
FEATURE [PartDesign::Body] Body013  label="B_Workbench_SideBrace_Template_Left"
  Group = -> [Sketch025,Pad015,Sketch026,Pocket008,Sketch027,Pad016,ShapeString007,Pocket018,ShapeString008,Pocket019]
  Origin = -> Origin028
  Tip = -> Pocket019
FEATURE [App::Part] Part013  label="P_Workbench_SideBrace_Template_Left"
  Group = -> [Body013]
  Origin = -> Origin027
FEATURE [Sketcher::SketchObject] Sketch034  label="S_Workbench_SideBrace_Template_Right_Base"
  FullyConstrained = true
  MapMode = 5
  Support = -> [XY_Plane034]
  sketch-geometry (4):
    g0: LineSegment StartX=0 StartY=0 StartZ=0 EndX=-63.5 EndY=0 EndZ=0
    g1: LineSegment StartX=-63.5 StartY=0 StartZ=0 EndX=-63.5 EndY=88.9 EndZ=0
    g2: LineSegment StartX=-63.5 StartY=88.9 StartZ=0 EndX=0 EndY=88.9 EndZ=0
    g3: LineSegment StartX=0 StartY=88.9 StartZ=0 EndX=0 EndY=0 EndZ=0
  constraints (11):
    c: Coincident(g0,g1)
    c: Coincident(g1,g2)
    c: Coincident(g2,g3)
    c: Coincident(g3,g0)
    c: Horizontal(g0)
    c: Horizontal(g2)
    c: Vertical(g1)
    c: Vertical(g3)
    c: Coincident(g0,g-1)
    c: DistanceX(g2,g2) = 63.5
    c: DistanceY(g1,g1) = 88.9
FEATURE [PartDesign::Pad] Pad021  label="PAD_Workbench_SideBrace_Template_Right_Base"
  Direction = (0,0,1)
  Length = 2
  Length2 = 10
  Profile = -> Sketch034
  ReferenceAxis = -> Sketch034 [N_Axis]
  Type = 0
  expr: Length = 2 mm
FEATURE [Sketcher::SketchObject] Sketch035  label="S_Workbench_SideBrace_Template_Right_Alignment"
  FullyConstrained = true
  MapMode = 5
  Support = -> [XY_Plane034]
  sketch-geometry (6):
    g0: LineSegment StartX=-63.5 StartY=0 StartZ=0 EndX=-63.5 EndY=88.9 EndZ=0
    g1: LineSegment StartX=0 StartY=88.9 StartZ=0 EndX=0 EndY=95.25 EndZ=0
    g2: LineSegment StartX=0 StartY=95.25 StartZ=0 EndX=-69.85 EndY=95.25 EndZ=0
    g3: LineSegment StartX=-63.5 StartY=88.9 StartZ=0 EndX=0 EndY=88.9 EndZ=0
    g4: LineSegment StartX=-69.85 StartY=95.25 StartZ=0 EndX=-69.85 EndY=0 EndZ=0
    g5: LineSegment StartX=-69.85 StartY=0 StartZ=0 EndX=-63.5 EndY=0 EndZ=0
  constraints (18):
    c: PointOnObject(g0,g-1)
    c: Vertical(g0)
    c: PointOnObject(g1,g-2)
    c: PointOnObject(g1,g-2)
    c: Coincident(g2,g1)
    c: Horizontal(g2)
    c: Coincident(g3,g0)
    c: Coincident(g3,g1)
    c: Horizontal(g3)
    c: Coincident(g4,g2)
    c: PointOnObject(g4,g-1)
    c: Coincident(g5,g4)
    c: Coincident(g5,g0)
    c: Vertical(g4)
    c: DistanceY(g0,g0) = 88.9
    c: DistanceX(g3,g3) = 63.5
    c: Equal(g1,g5)
    c: DistanceX(g5,g5) = 6.35
FEATURE [PartDesign::Pad] Pad022  label="PAD_Workbench_SideBrace_Template_Right_Alignment"
  BaseFeature = -> Pad021
  Direction = (0,0,1)
  Length = 8
  Length2 = 10
  Profile = -> Sketch035
  ReferenceAxis = -> Sketch035 [N_Axis]
  Type = 0
  expr: Length = 8 mm
FEATURE [Sketcher::SketchObject] Sketch036  label="S_Workbench_SideBrace_Template_Right_Holes"
  FullyConstrained = true
  MapMode = 5
  Support = -> [XY_Plane034]
  expr: Constraints[2] = 3.5 in - 1 in
  expr: Constraints[5] = 1 mm
  sketch-geometry (2):
    g0: Circle CenterX=-12.7 CenterY=63.5 CenterZ=0 NormalX=0 NormalY=0 NormalZ=1 AngleXU=0 Radius=0.5
    g1: Circle CenterX=-12.7 CenterY=25.4 CenterZ=0 NormalX=0 NormalY=0 NormalZ=1 AngleXU=0 Radius=0.5
  constraints (6):
    c: Equal(g0,g1)
    c: DistanceY(g1,g0) = 38.1
    c: DistanceY(g-1,g0) = 63.5
    c: Vertical(g0,g1)
    c: DistanceX(g1,g-1) = 12.7
    c: Diameter(g1) = 1
FEATURE [PartDesign::Pocket] Pocket020  label="POCKET_Workbench_SideBrace_Template_Right_Holes"
  BaseFeature = -> Pad022
  Direction = (0,0,-1)
  Length = 5.0038
  Length2 = 5
  Profile = -> Sketch036
  ReferenceAxis = -> Sketch036 [N_Axis]
  Reversed = true
  Type = 0
FEATURE [Part::Part2DObjectPython] ShapeString009  label="TEXT_Workbench_SideBrace_Template_Right_Label0"  # Draft 2D object (typed FeaturePython)
  FontFile = <userpath>/3dPrinting/workshop/OpenSans-Bold.ttf
  MakeFace = true
  Placement = pos=(-4.953,48.5394,-0.0254) rot=(0,1,0;3.14159rad)
  Size = 10.0076
  String = Side Brace
  Tracking = 0
FEATURE [Part::Part2DObjectPython] ShapeString010  label="_Workbench_SideBrace_Template_Right_Label1"  # Draft 2D object (typed FeaturePython)
  FontFile = <userpath>/3dPrinting/workshop/OpenSans-Bold.ttf
  MakeFace = true
  Placement = pos=(-4.953,36.6522,-0.254) rot=(0,1,0;3.14159rad)
  Size = 10.0076
  String = Right
  Tracking = 0
FEATURE [PartDesign::Pocket] Pocket021  label="POCKET_Workbench_SideBrace_Template_Right_Label0"
  BaseFeature = -> Pocket020
  Direction = (-2.98023e-07,0,1)
  Length = 1
  Length2 = 5
  Profile = -> ShapeString009
  ReferenceAxis = -> ShapeString009 [N_Axis]
  Type = 0
  expr: Length = 1 mm
FEATURE [PartDesign::Pocket] Pocket022  label="POCKET_Workbench_SideBrace_Template_Right_Label1"
  BaseFeature = -> Pocket021
  Direction = (-2.98023e-07,0,1)
  Length = 1
  Length2 = 5
  Profile = -> ShapeString010
  ReferenceAxis = -> ShapeString010 [N_Axis]
  Type = 0
  expr: Length = 1 mm
FEATURE [PartDesign::Body] Body016  label="B_Workbench_SideBrace_Template_Right"
  Group = -> [Sketch034,Pad021,Sketch035,Pad022,Sketch036,Pocket020,ShapeString009,ShapeString010,Pocket021,Pocket022]
  Origin = -> Origin034
  Tip = -> Pocket022
FEATURE [App::Part] Part016  label="P_Workbench_SideBrace_Template_Right"
  Group = -> [Body016]
  Origin = -> Origin033
FEATURE [TechDraw::DrawSVGTemplate] Template001  label="TEMPLATE_Step4_LegHoles"
  EditableTexts = Code=JWB; CompanyAddress=570 Eagle View NW, Salem OR 97304; CompanyName=Ensor Robotics; DrawingNumber=4-1-Leg-Holes; DrawingTitle1=Leg Hole Drilling Guide; DrawingTitle2=Drilling Leg Holes; DrawnBy=Jon A; Revision=v1; Scale=3:20; Sheet=Sheet 4 of 11
  Height = 215.9
  Orientation = 1
  Template = /snap/freecad/908/usr/share/Mod/TechDraw/Templates/USLetter_Landscape.svg
  Width = 279.4
FEATURE [TechDraw::DrawViewPart] View001  label="VIEW_Step4_BackLeg"
  CoarseView = false
  Direction = (-0.57735,0.57735,-0.57735)
  Focus = 100
  HardHidden = false
  IsoCount = 0
  IsoHidden = false
  IsoVisible = false
  LockPosition = false
  Perspective = false
  Rotation = 0
  Scale = 0.15
  ScaleType = 0
  ScrubCount = 0
  SeamHidden = false
  SeamVisible = false
  SmoothHidden = false
  SmoothVisible = true
  Source = -> [Part004]
  X = 148.551
  XDirection = (0,-0.707106,-0.707106)
  Y = 133.991
FEATURE [TechDraw::DrawViewPart] View002  label="VIEW_Step4_FrontLeg"
  CoarseView = false
  Direction = (-0.57735,0.57735,-0.57735)
  Focus = 100
  HardHidden = false
  IsoCount = 0
  IsoHidden = false
  IsoVisible = false
  LockPosition = false
  Perspective = false
  Rotation = 0
  Scale = 0.15
  ScaleType = 0
  ScrubCount = 0
  SeamHidden = false
  SeamVisible = false
  SmoothHidden = false
  SmoothVisible = true
  Source = -> [Part005]
  X = 146.294
  XDirection = (0,-0.707106,-0.707106)
  Y = 100.384
FEATURE [TechDraw::DrawViewPart] View003  label="VIEW_Step4_FrontLeg_Template"
  CoarseView = false
  Direction = (0.57735,0.57735,0.57735)
  Focus = 100
  HardHidden = false
  IsoCount = 0
  IsoHidden = false
  IsoVisible = false
  LockPosition = false
  Perspective = false
  Rotation = 0
  Scale = 0.15
  ScaleType = 0
  ScrubCount = 0
  SeamHidden = false
  SeamVisible = false
  SmoothHidden = false
  SmoothVisible = true
  Source = -> [Part012]
  X = 110.748
  XDirection = (0.707107,-0.707107,0)
  Y = 87.5986
FEATURE [TechDraw::DrawViewBalloon] Balloon004  label="BALOON_Step4_BackLeg"
  BubbleShape = 3
  EndType = 0
  EndTypeScale = 1
  KinkLength = 5
  LockPosition = false
  OriginX = 167.273
  OriginY = -69.2228
  Rotation = 0
  Scale = 0.15
  ScaleType = 0
  ShapeScale = 1
  SourceView = -> View001
  Text = Back Leg (x2)
  TextWrapLen = -1
  X = 305.693
  Y = 168.392
FEATURE [TechDraw::DrawViewBalloon] Balloon005  label="BALOON_Step4_BackLeg001"
  BubbleShape = 3
  EndType = 0
  EndTypeScale = 1
  KinkLength = 5
  LockPosition = false
  OriginX = 75.7082
  OriginY = -18.3537
  Rotation = 0
  Scale = 0.15
  ScaleType = 0
  ShapeScale = 1
  SourceView = -> View002
  Text = Front Leg (x2)
  TextWrapLen = -1
  X = -631.16
  Y = 396.102
FEATURE [TechDraw::DrawViewBalloon] Balloon006  label="BALOON_Step4_FrontLeg_Template"
  BubbleShape = 3
  EndType = 0
  EndTypeScale = 1
  KinkLength = 5
  LockPosition = false
  OriginX = -13.3128
  OriginY = -0.549511
  Rotation = 0
  Scale = 0.15
  ScaleType = 0
  ShapeScale = 1
  SourceView = -> View003
  Text = Front Leg Template
  TextWrapLen = -1
  X = -352.364
  Y = 153.869
FEATURE [TechDraw::DrawRichAnno] RichTextAnnotation  label="TEXT_Step4_LegHoles_Instructions"
  AnnoText = <!DOCTYPE HTML PUBLIC "-//W3C//DTD HTML 4.0//EN" "http://www.w3.org/TR/REC-html40/strict.dtd">\n<html><head><meta name="qrichtext" content="1" /><style type="text/css">\np, li { white-space: pre-wrap; }\n</style></head><body style=" font-family:'osifont'; font-size:9pt; font-weight:400; font-style:normal;">\n<p style=" margin-top:0px; margin-bottom:0px; margin-left:0px; margin-right:0px; -qt-block-indent:0; text-indent:0px;"><span style=" font-family:'Sans Serif'; font-size:10pt;">Use leg hole template to mark and then drill 1/4 inch holes on front legs.  </span></p>\n<p style="-qt-paragraph-type:empty; margin-top:0px; margin-bottom:0px; margin-left:0px; margin-right:0px; -qt-block-indent:0; text-indent:0px; font-family:'Sans Serif'; font-size:10pt;"><br /></p>\n<p style=" margin-top:0px; margin-bottom:0px; margin-left:0px; margin-right:0px; -qt-block-indent:0; text-indent:0px;"><span style=" font-family:'Sans Serif'; font-size:10pt;">Use front legs as templates to drill 1/4 inch holes in back legs so that the bottoms of the legs are aligned.</span></p></body></html>
  LockPosition = false
  MaxWidth = 50
  Rotation = 0
  Scale = 0.15
  ScaleType = 0
  ShowFrame = false
  X = 46.7907
  Y = 62.138
FEATURE [TechDraw::DrawPage] Page001  label="DRAWING_Step4_LegHoles"
  KeepUpdated = true
  NextBalloonIndex = 7
  ProjectionType = 0
  Scale = 0.15
  Template = -> Template001
  Views = -> [View001,View002,View003,Balloon004,Balloon005,Balloon006,RichTextAnnotation]
  expr: Scale = 0.15
FEATURE [TechDraw::DrawSVGTemplate] Template003  label="TEMPLATE_Step5_BackLegShelfHoles"
  EditableTexts = Code=JWB; CompanyAddress=570 Eagle View NW, Salem OR 97304; CompanyName=Ensor Robotics; DrawingNumber=5-1-Back-Leg-Shelf-Holes; DrawingTitle1=Back Leg Drilling Guide; DrawingTitle2=Holes for shelves; DrawnBy=Jon A; Revision=v1; Scale=3:20; Sheet=Sheet 5 of 11
  Height = 215.9
  Orientation = 1
  Template = /snap/freecad/908/usr/share/Mod/TechDraw/Templates/USLetter_Landscape.svg
  Width = 279.4
FEATURE [TechDraw::DrawViewPart] View006  label="VIEW_Step5_BackLegShelfHoles_BackLeg"
  CoarseView = false
  Direction = (0.57735,-0.57735,-0.57735)
  Focus = 100
  HardHidden = false
  IsoCount = 0
  IsoHidden = false
  IsoVisible = false
  LockPosition = false
  Perspective = false
  Rotation = 0
  Scale = 0.15
  ScaleType = 0
  ScrubCount = 0
  SeamHidden = false
  SeamVisible = false
  SmoothHidden = false
  SmoothVisible = true
  Source = -> [Part004]
  X = 144.55
  XDirection = (0,0.707106,-0.707106)
  Y = 132.516
FEATURE [TechDraw::DrawViewPart] View007  label="VIEW_Step5_BackLegShelfHoles_Template"
  CoarseView = false
  Direction = (0.57735,-0.57735,-0.57735)
  Focus = 100
  HardHidden = false
  IsoCount = 0
  IsoHidden = false
  IsoVisible = false
  LockPosition = false
  Perspective = false
  Rotation = 0
  Scale = 0.15
  ScaleType = 0
  ScrubCount = 0
  SeamHidden = false
  SeamVisible = false
  SmoothHidden = false
  SmoothVisible = true
  Source = -> [Part014]
  X = 55.4189
  XDirection = (-0.707106,-0.707106,0)
  Y = 157.475
FEATURE [TechDraw::DrawRichAnno] RichTextAnnotation002  label="TEXT_Step5_Instructions"
  AnnoText = <!DOCTYPE HTML PUBLIC "-//W3C//DTD HTML 4.0//EN" "http://www.w3.org/TR/REC-html40/strict.dtd">\n<html><head><meta name="qrichtext" content="1" /><style type="text/css">\np, li { white-space: pre-wrap; }\n</style></head><body style=" font-family:'osifont'; font-size:9pt; font-weight:400; font-style:normal;">\n<p style=" margin-top:0px; margin-bottom:0px; margin-left:0px; margin-right:0px; -qt-block-indent:0; text-indent:0px;"><span style=" font-family:'Sans Serif'; font-size:10pt;">Use the Back Leg Hole Template to mark and drill evenly spaced 1/4 inch holes on each of the two back legs.  Holes should be offset 2 inches from the side and aligned with the lower holes.</span></p>\n<p style="-qt-paragraph-type:empty; margin-top:0px; margin-bottom:0px; margin-left:0px; margin-right:0px; -qt-block-indent:0; text-indent:0px; font-family:'Sans Serif'; font-size:10pt;"><br /></p>\n<p style=" margin-top:0px; margin-bottom:0px; margin-left:0px; margin-right:0px; -qt-block-indent:0; text-indent:0px;"><span style=" font-family:'Sans Serif'; font-size:10pt;">The template should start at the top of the leg and mark out holes every 3 inches with the first hole 1/2 inch from the top.</span></p>\n<p style="-qt-paragraph-type:empty; margin-top:0px; margin-bottom:0px; margin-left:0px; margin-right:0px; -qt-block-indent:0; text-indent:0px; font-family:'Sans Serif'; font-size:10pt;"><br /></p>\n<p style=" margin-top:0px; margin-bottom:0px; margin-left:0px; margin-right:0px; -qt-block-indent:0; text-indent:0px;"><span style=" font-family:'Sans Serif'; font-size:10pt;">Take care that both legs match so that the shelves will hang level.</span></p></body></html>
  LockPosition = false
  MaxWidth = 80
  Rotation = 0
  Scale = 0.15
  ScaleType = 0
  ShowFrame = false
  X = 67.5794
  Y = 67.7373
FEATURE [TechDraw::DrawViewBalloon] Balloon009  label="BALOON_Step5_BackLegShelfHoles_BackLeg"
  BubbleShape = 3
  EndType = 0
  EndTypeScale = 1
  KinkLength = 5
  LockPosition = false
  OriginX = -306.268
  OriginY = 186.36
  Rotation = 0
  Scale = 0.15
  ScaleType = 0
  ShapeScale = 1
  SourceView = -> View006
  Text = Back Leg (x2)
  TextWrapLen = -1
  X = -158.643
  Y = 313.569
FEATURE [TechDraw::DrawViewBalloon] Balloon010  label="VIEW_Step5_BackLegShelfHoles_Template001"
  BubbleShape = 3
  EndType = 0
  EndTypeScale = 1
  KinkLength = 5
  LockPosition = false
  OriginX = -14.6302
  OriginY = 4.44213
  Rotation = 0
  Scale = 0.15
  ScaleType = 0
  ShapeScale = 1
  SourceView = -> View007
  Text = Back Leg Shelf Holes
  TextWrapLen = -1
  X = 92.1622
  Y = -227.672
FEATURE [TechDraw::DrawPage] Page003  label="DRAWING_Step5_BackLegShelfHoles"
  KeepUpdated = true
  NextBalloonIndex = 9
  ProjectionType = 0
  Scale = 0.15
  Template = -> Template003
  Views = -> [View006,View007,RichTextAnnotation002,Balloon009,Balloon010]
FEATURE [TechDraw::DrawSVGTemplate] Template004  label="TEMPLATE_Step7_ShelfBraces"
  EditableTexts = Code=JWB; CompanyAddress=570 Eagle View Dr NW; CompanyName=Ensor Robotics; DrawingNumber=Drawing Number; DrawingTitle1=Shelf Brace Drilling Guide; DrawingTitle2=Use template to mark holes; DrawingTitle3=Make 4; DrawnBy=Jon A.; Revision=v1; Scale=1:2; Sheet=Sheet 7 of 11
  Height = 215.9
  Orientation = 1
  Template = /snap/freecad/908/usr/share/Mod/TechDraw/Templates/USLetter_Landscape.svg
  Width = 279.4
FEATURE [TechDraw::DrawViewPart] View008  label="VIEW_Step7_ShelfBraces_Template"
  CoarseView = false
  Direction = (0.57735,-0.57735,-0.577351)
  Focus = 100
  HardHidden = false
  IsoCount = 0
  IsoHidden = false
  IsoVisible = false
  LockPosition = false
  Perspective = false
  Rotation = 0
  Scale = 0.5
  ScaleType = 0
  ScrubCount = 0
  SeamHidden = false
  SeamVisible = false
  SmoothHidden = false
  SmoothVisible = true
  Source = -> [Part015]
  X = 76.5541
  XDirection = (-0.707106,-0.707106,0)
  Y = 81.2719
FEATURE [TechDraw::DrawViewPart] View009  label="VIEW_Step7_ShelfBraces_ShelfBrace"
  CoarseView = false
  Direction = (-0.57735,0.57735,-0.57735)
  Focus = 100
  HardHidden = false
  IsoCount = 0
  IsoHidden = false
  IsoVisible = false
  LockPosition = false
  Perspective = false
  Rotation = 0
  Scale = 0.5
  ScaleType = 0
  ScrubCount = 0
  SeamHidden = false
  SeamVisible = false
  SmoothHidden = false
  SmoothVisible = true
  Source = -> [Part010]
  X = 153.167
  XDirection = (0,-0.707106,-0.707106)
  Y = 133.982
FEATURE [TechDraw::DrawViewBalloon] Balloon011  label="BALOON_Step7_ShelfBraces_Template"
  BubbleShape = 3
  EndType = 0
  EndTypeScale = 1
  KinkLength = 5
  LockPosition = false
  OriginX = -48.5337
  OriginY = 31.1846
  Rotation = 0
  Scale = 0.5
  ScaleType = 0
  ShapeScale = 1
  SourceView = -> View008
  Text = Shelf Brace Template
  TextWrapLen = -1
  X = -21.1206
  Y = -79.3731
FEATURE [TechDraw::DrawViewBalloon] Balloon012  label="BALOON_Step7_ShelfBraces_ShelfBrace"
  BubbleShape = 3
  EndType = 0
  EndTypeScale = 1
  KinkLength = 5
  LockPosition = false
  OriginX = -1.22154
  OriginY = 8.03119
  Rotation = 0
  Scale = 0.5
  ScaleType = 0
  ShapeScale = 1
  SourceView = -> View009
  Text = Shelf Brace (x4)
  TextWrapLen = -1
  X = 138.707
  Y = -68.2266
FEATURE [TechDraw::DrawRichAnno] RichTextAnnotation003  label="TEXT_Step7_ShelfBraces_Instructions"
  AnnoText = <!DOCTYPE HTML PUBLIC "-//W3C//DTD HTML 4.0//EN" "http://www.w3.org/TR/REC-html40/strict.dtd">\n<html><head><meta name="qrichtext" content="1" /><style type="text/css">\np, li { white-space: pre-wrap; }\n</style></head><body style=" font-family:'osifont'; font-size:9pt; font-weight:400; font-style:normal;">\n<p style=" margin-top:0px; margin-bottom:0px; margin-left:0px; margin-right:0px; -qt-block-indent:0; text-indent:0px;"><span style=" font-family:'Sans Serif'; font-size:10pt;">Using the Shelf Brace Template, mark a triangle from the 3/4 in plywood and cut 4 shelf braces to hold the shelves.</span></p>\n<p style="-qt-paragraph-type:empty; margin-top:0px; margin-bottom:0px; margin-left:0px; margin-right:0px; -qt-block-indent:0; text-indent:0px; font-family:'Sans Serif'; font-size:10pt;"><br /></p>\n<p style=" margin-top:0px; margin-bottom:0px; margin-left:0px; margin-right:0px; -qt-block-indent:0; text-indent:0px;"><span style=" font-family:'Sans Serif'; font-size:10pt;">Mark the holes 3 inches apart using the template as a reference for the holes.  Drill holes to 1/4 inch.</span></p></body></html>
  LockPosition = false
  MaxWidth = 80
  Rotation = 0
  Scale = 0.5
  ScaleType = 0
  ShowFrame = false
  X = 66.7145
  Y = 167.682
FEATURE [TechDraw::DrawPage] Page004  label="DRAWING_Step7_ShelfBraces"
  KeepUpdated = true
  NextBalloonIndex = 3
  ProjectionType = 0
  Scale = 0.5
  Template = -> Template004
  Views = -> [View008,View009,Balloon011,Balloon012,RichTextAnnotation003]
FEATURE [TechDraw::DrawSVGTemplate] Template005  label="TEMPLATE_Step6_SideBraces"
  EditableTexts = Code=JWB; CompanyAddress=570 Eagle View Dr NW; CompanyName=Ensor Robotics; DrawingNumber=6-1-SideBrace-Drilling; DrawingTitle1=Side Brace Drilling Guide; DrawingTitle2=Holes on left/right of side braces; DrawingTitle3=Make 4; DrawnBy=Jon A.; Revision=v1; Scale=3:10; Sheet=Sheet 6 of 11
  Height = 215.9
  Orientation = 1
  Template = /snap/freecad/908/usr/share/Mod/TechDraw/Templates/USLetter_Landscape.svg
  Width = 279.4
FEATURE [TechDraw::DrawViewPart] View011  label="VIEW_Step6_SideBraces_TemplateLeft"
  CoarseView = false
  Direction = (0.57735,-0.57735,-0.57735)
  Focus = 100
  HardHidden = false
  IsoCount = 0
  IsoHidden = false
  IsoVisible = false
  LockPosition = false
  Perspective = false
  Rotation = 0
  Scale = 0.3
  ScaleType = 0
  ScrubCount = 0
  SeamHidden = false
  SeamVisible = false
  SmoothHidden = false
  SmoothVisible = true
  Source = -> [Part013]
  X = 42.6431
  XDirection = (-0.707106,-0.707106,0)
  Y = 61.2528
FEATURE [TechDraw::DrawViewPart] View012  label="VIEW_Step6_SideBraces_TemplateRight"
  CoarseView = false
  Direction = (0.57735,-0.57735,-0.57735)
  Focus = 100
  HardHidden = false
  IsoCount = 0
  IsoHidden = false
  IsoVisible = false
  LockPosition = false
  Perspective = false
  Rotation = 0
  Scale = 0.3
  ScaleType = 0
  ScrubCount = 0
  SeamHidden = false
  SeamVisible = false
  SmoothHidden = false
  SmoothVisible = true
  Source = -> [Part016]
  X = 233.088
  XDirection = (-0.707106,-0.707106,0)
  Y = 172.417
FEATURE [TechDraw::DrawViewPart] View013  label="DRAWING_Step6_SideBraces_SideBrace"
  CoarseView = false
  Direction = (0.57735,0.57735,0.57735)
  Focus = 100
  HardHidden = false
  IsoCount = 0
  IsoHidden = false
  IsoVisible = false
  LockPosition = false
  Perspective = false
  Rotation = 0
  Scale = 0.3
  ScaleType = 0
  ScrubCount = 0
  SeamHidden = false
  SeamVisible = false
  SmoothHidden = false
  SmoothVisible = true
  Source = -> [Part007]
  X = 139.579
  XDirection = (-5.7735e-07,-0.707107,0.707107)
  Y = 115.543
FEATURE [TechDraw::DrawViewBalloon] Balloon013  label="BALOON_Step6_SideBraces_TemplateLeft"
  BubbleShape = 3
  EndType = 0
  EndTypeScale = 1
  KinkLength = 5
  LockPosition = false
  OriginX = -37.734
  OriginY = 0.992257
  Rotation = 0
  Scale = 0.3
  ScaleType = 0
  ShapeScale = 1
  SourceView = -> View011
  Text = Left Side Brace Template
  TextWrapLen = -1
  X = 113.91
  Y = 228.498
FEATURE [TechDraw::DrawViewBalloon] Balloon014  label="BALOON_Step6_SideBraces_TemplateRight"
  BubbleShape = 3
  EndType = 0
  EndTypeScale = 1
  KinkLength = 5
  LockPosition = false
  OriginX = 25.1726
  OriginY = -8.08155
  Rotation = 0
  Scale = 0.3
  ScaleType = 0
  ShapeScale = 1
  SourceView = -> View012
  Text = Right Side Brace Template
  TextWrapLen = -1
  X = -206.439
  Y = 54.4033
FEATURE [TechDraw::DrawViewBalloon] Balloon015  label="BALOON_Step6_SideBraces_TemplateRight001"
  BubbleShape = 3
  EndType = 0
  EndTypeScale = 1
  KinkLength = 5
  LockPosition = false
  OriginX = 14.4783
  OriginY = 11.0286
  Rotation = 0
  Scale = 0.3
  ScaleType = 0
  ShapeScale = 1
  SourceView = -> View013
  Text = Side Brace (x4)
  TextWrapLen = -1
  X = 144.05
  Y = -75.9587
FEATURE [TechDraw::DrawRichAnno] RichTextAnnotation004  label="TEXT_Step6_SideBraces_Instructions"
  AnnoText = <!DOCTYPE HTML PUBLIC "-//W3C//DTD HTML 4.0//EN" "http://www.w3.org/TR/REC-html40/strict.dtd">\n<html><head><meta name="qrichtext" content="1" /><style type="text/css">\np, li { white-space: pre-wrap; }\n</style></head><body style=" font-family:'osifont'; font-size:9pt; font-weight:400; font-style:normal;">\n<p style=" margin-top:0px; margin-bottom:0px; margin-left:0px; margin-right:0px; -qt-block-indent:0; text-indent:0px;"><span style=" font-family:'Sans Serif'; font-size:10pt;">Cut 4 lengths of 2x4 to 30 inches, making sure they are all the same length.</span></p>\n<p style="-qt-paragraph-type:empty; margin-top:0px; margin-bottom:0px; margin-left:0px; margin-right:0px; -qt-block-indent:0; text-indent:0px; font-family:'Sans Serif'; font-size:10pt;"><br /></p>\n<p style=" margin-top:0px; margin-bottom:0px; margin-left:0px; margin-right:0px; -qt-block-indent:0; text-indent:0px;"><span style=" font-family:'Sans Serif'; font-size:10pt;">Mark and drill 1/4 inch holes using the left and right templates.</span></p></body></html>
  LockPosition = false
  MaxWidth = 80
  Rotation = 0
  Scale = 0.3
  ScaleType = 0
  ShowFrame = false
  X = 71.5123
  Y = 171.103
FEATURE [TechDraw::DrawPage] Page005  label="DRAWING_Step6_SideBraces"
  KeepUpdated = true
  NextBalloonIndex = 4
  ProjectionType = 0
  Scale = 0.3
  Template = -> Template005
  Views = -> [View011,View012,View013,Balloon013,Balloon014,Balloon015,RichTextAnnotation004]
FEATURE [TechDraw::DrawSVGTemplate] Template007  label="TEMPLATE_Step8_SideAssembly"
  EditableTexts = Code=JWB; CompanyAddress=570 Eagle View Dr NW; CompanyName=Ensor Robotics; DrawingNumber=8-1-SideAssembly; DrawingTitle1=Side Assembly; DrawingTitle2=Assemble left and right leg supports; DrawnBy=Jon A.; Revision=v1; Scale=2:25; Sheet=Sheet 8 of 11
  Height = 215.9
  Orientation = 1
  Template = /snap/freecad/908/usr/share/Mod/TechDraw/Templates/USLetter_Landscape.svg
  Width = 279.4
FEATURE [TechDraw::DrawViewPart] View015  label="VIEW_Step8_SideAssembly_Assembly"
  CoarseView = false
  Direction = (1,0,0)
  Focus = 100
  HardHidden = false
  IsoCount = 0
  IsoHidden = false
  IsoVisible = false
  LockPosition = false
  Perspective = false
  Rotation = 0
  Scale = 0.08
  ScaleType = 0
  ScrubCount = 0
  SeamHidden = false
  SeamVisible = false
  SmoothHidden = false
  SmoothVisible = true
  Source = -> [Assembly]
  X = 78.3692
  XDirection = (0,1,0)
  Y = 112.577
FEATURE [TechDraw::DrawRichAnno] RichTextAnnotation006  label="TEXT_Step8_SideAssembly_Instructions"
  AnnoText = <!DOCTYPE HTML PUBLIC "-//W3C//DTD HTML 4.0//EN" "http://www.w3.org/TR/REC-html40/strict.dtd">\n<html><head><meta name="qrichtext" content="1" /><style type="text/css">\np, li { white-space: pre-wrap; }\n</style></head><body style=" font-family:'osifont'; font-size:9pt; font-weight:400; font-style:normal;">\n<p style=" margin-top:0px; margin-bottom:0px; margin-left:0px; margin-right:0px; -qt-block-indent:0; text-indent:0px;"><span style=" font-family:'Sans Serif'; font-size:10pt;">Assemble left and right halves as shown with front and back legs on floor, with side braces bolted on top using 1/4 inch diameter, 3 1/2 inch long bolts.</span></p>\n<p style="-qt-paragraph-type:empty; margin-top:0px; margin-bottom:0px; margin-left:0px; margin-right:0px; -qt-block-indent:0; text-indent:0px; font-family:'Sans Serif'; font-size:10pt;"><br /></p>\n<p style=" margin-top:0px; margin-bottom:0px; margin-left:0px; margin-right:0px; -qt-block-indent:0; text-indent:0px;"><span style=" font-family:'Sans Serif'; font-size:10pt;">The left and right halves should be mirror images of one another.</span></p></body></html>
  LockPosition = false
  MaxWidth = 120
  Rotation = 0
  Scale = 0.08
  ScaleType = 0
  ShowFrame = false
  X = 194.993
  Y = 166.432
FEATURE [TechDraw::DrawSVGTemplate] Template009  label="TEMPLATE_Step9_TableTopAssembly"
  EditableTexts = Code=JWB; CompanyAddress=570 Eagle View Dr NW; CompanyName=Ensor Robotics; DrawingNumber=9-1-TableTopAssembly; DrawingTitle1=Table Top Assembly; DrawingTitle2=Install Table Top; DrawnBy=Jon A.; Revision=v1; Scale=1:20; Sheet=Sheet 9 of 11
  Height = 215.9
  Orientation = 1
  Template = /snap/freecad/908/usr/share/Mod/TechDraw/Templates/USLetter_Landscape.svg
  Width = 279.4
FEATURE [TechDraw::DrawViewPart] View017  label="VIEW_Step9_TableTopAssembly"
  CoarseView = false
  Direction = (0.57735,-0.57735,0.57735)
  Focus = 100
  HardHidden = false
  IsoCount = 0
  IsoHidden = false
  IsoVisible = false
  LockPosition = false
  Perspective = false
  Rotation = 0
  Scale = 0.05
  ScaleType = 0
  ScrubCount = 0
  SeamHidden = false
  SeamVisible = false
  SmoothHidden = false
  SmoothVisible = true
  Source = -> [Assembly]
  X = 79.8965
  XDirection = (0.707107,0.707107,0)
  Y = 118.976
FEATURE [TechDraw::DrawRichAnno] RichTextAnnotation008  label="TEXT_Step9_TableTopAssembly_Instructions"
  AnnoText = <!DOCTYPE HTML PUBLIC "-//W3C//DTD HTML 4.0//EN" "http://www.w3.org/TR/REC-html40/strict.dtd">\n<html><head><meta name="qrichtext" content="1" /><style type="text/css">\np, li { white-space: pre-wrap; }\n</style></head><body style=" font-family:'osifont'; font-size:9pt; font-weight:400; font-style:normal;">\n<p style=" margin-top:0px; margin-bottom:0px; margin-left:0px; margin-right:0px; -qt-block-indent:0; text-indent:0px;"><span style=" font-family:'Sans Serif'; font-size:10pt;">Place table top on left and right legs.  Square them and fasten table top to legs using drywall screws.  Drilling small pilot holes may help.</span></p>\n<p style="-qt-paragraph-type:empty; margin-top:0px; margin-bottom:0px; margin-left:0px; margin-right:0px; -qt-block-indent:0; text-indent:0px; font-family:'Sans Serif'; font-size:10pt;"><br /></p>\n<p style=" margin-top:0px; margin-bottom:0px; margin-left:0px; margin-right:0px; -qt-block-indent:0; text-indent:0px;"><span style=" font-family:'Sans Serif'; font-size:10pt;">Shelves should not yet be installed, but may be used to help square the assembly.</span></p></body></html>
  LockPosition = false
  MaxWidth = 120
  Rotation = 0
  Scale = 0.05
  ScaleType = 0
  ShowFrame = false
  X = 198.83
  Y = 168.137
FEATURE [TechDraw::DrawPage] Page009  label="DRAWING_Step9_TableTopAssembly"
  KeepUpdated = true
  NextBalloonIndex = 1
  ProjectionType = 0
  Scale = 0.05
  Template = -> Template009
  Views = -> [View017,RichTextAnnotation008]
FEATURE [TechDraw::DrawSVGTemplate] Template010  label="TEMPLATE_Step10_BackAssembly"
  EditableTexts = Code=JWB; CompanyAddress=570 Eagle View Dr NW; CompanyName=Ensor Robotics; DrawingNumber=10-1-BackAssembly; DrawingTitle1=Back Assembly; DrawingTitle2=Mount back to sides and square assembly; DrawnBy=Jon A.; Revision=v1; Scale=1:20; Sheet=Sheet 10 of 11
  Height = 215.9
  Orientation = 1
  Template = /snap/freecad/908/usr/share/Mod/TechDraw/Templates/USLetter_Landscape.svg
  Width = 279.4
FEATURE [TechDraw::DrawRichAnno] RichTextAnnotation009  label="TEXT_Step10_BackAssembly_Instructions"
  AnnoText = <!DOCTYPE HTML PUBLIC "-//W3C//DTD HTML 4.0//EN" "http://www.w3.org/TR/REC-html40/strict.dtd">\n<html><head><meta name="qrichtext" content="1" /><style type="text/css">\np, li { white-space: pre-wrap; }\n</style></head><body style=" font-family:'osifont'; font-size:9pt; font-weight:400; font-style:normal;">\n<p style=" margin-top:0px; margin-bottom:0px; margin-left:0px; margin-right:0px; -qt-block-indent:0; text-indent:0px;"><span style=" font-family:'Sans Serif'; font-size:10pt;">Use two sheets of MDF measuring 24x48.  The lower sheet may be pegboard if you want mount holes for tools.</span></p>\n<p style="-qt-paragraph-type:empty; margin-top:0px; margin-bottom:0px; margin-left:0px; margin-right:0px; -qt-block-indent:0; text-indent:0px; font-family:'Sans Serif'; font-size:10pt;"><br /></p>\n<p style=" margin-top:0px; margin-bottom:0px; margin-left:0px; margin-right:0px; -qt-block-indent:0; text-indent:0px;"><span style=" font-family:'Sans Serif'; font-size:10pt;">Place MDF sheets on to the back of left and right back legs, ensuring that they are square.</span></p>\n<p style="-qt-paragraph-type:empty; margin-top:0px; margin-bottom:0px; margin-left:0px; margin-right:0px; -qt-block-indent:0; text-indent:0px; font-family:'Sans Serif'; font-size:10pt;"><br /></p>\n<p style=" margin-top:0px; margin-bottom:0px; margin-left:0px; margin-right:0px; -qt-block-indent:0; text-indent:0px;"><span style=" font-family:'Sans Serif'; font-size:10pt;">Fasten using small nails.</span></p>\n<p style="-qt-paragraph-type:empty; margin-top:0px; margin-bottom:0px; margin-left:0px; margin-right:0px; -qt-block-indent:0; text-indent:0px; font-family:'Sans Serif'; font-size:10pt;"><br /></p>\n<p style=" margin-top:0px; margin-bottom:0px; margin-left:0px; margin-right:0px; -qt-block-indent:0; text-indent:0px;"><span style=" font-family:'Sans Serif'; font-size:10pt;">Fasten Back and Front braces 2x4 braces to table top using screws.</span></p></body></html>
  LockPosition = false
  MaxWidth = 120
  Rotation = 0
  Scale = 0.05
  ScaleType = 0
  ShowFrame = false
  X = 83.8604
  Y = 170.27
FEATURE [TechDraw::DrawViewPart] View018  label="VIEW_Step10_BackAssembly"
  CoarseView = false
  Direction = (0.57735,0.57735,0.57735)
  Focus = 100
  HardHidden = false
  IsoCount = 0
  IsoHidden = false
  IsoVisible = false
  LockPosition = false
  Perspective = false
  Rotation = 0
  Scale = 0.05
  ScaleType = 0
  ScrubCount = 0
  SeamHidden = false
  SeamVisible = false
  SmoothHidden = false
  SmoothVisible = true
  Source = -> [Assembly]
  X = 149.006
  XDirection = (0.707107,0,-0.707107)
  Y = 114.109
FEATURE [TechDraw::DrawViewBalloon] Balloon021  label="BALOON_Step10_BackAssembly_MDF"
  BubbleShape = 3
  EndType = 0
  EndTypeScale = 1
  KinkLength = 5
  LockPosition = false
  OriginX = -762.793
  OriginY = -113.514
  Rotation = 0
  Scale = 0.05
  ScaleType = 0
  ShapeScale = 1
  SourceView = -> View018
  Text = MDF Back
  TextWrapLen = -1
  X = -1775.41
  Y = -463.964
FEATURE [TechDraw::DrawViewBalloon] Balloon022  label="BALOON_Step10_BackAssembly_BackBrace"
  BubbleShape = 3
  EndType = 0
  EndTypeScale = 1
  KinkLength = 5
  LockPosition = false
  OriginX = 94.8649
  OriginY = 271.171
  Rotation = 0
  Scale = 0.05
  ScaleType = 0
  ShapeScale = 1
  SourceView = -> View018
  Text = Back Brace
  TextWrapLen = -1
  X = 1647.74
  Y = 1073.57
FEATURE [TechDraw::DrawPage] Page010  label="DRAWING_Step10_BackAssembly"
  KeepUpdated = true
  NextBalloonIndex = 4
  ProjectionType = 0
  Scale = 0.05
  Template = -> Template010
  Views = -> [RichTextAnnotation009,View018,Balloon021,Balloon022]
FEATURE [Sketcher::SketchObject] Sketch037
  FullyConstrained = true
  MapMode = 5
  Support = -> [XY_Plane037]
  expr: Constraints[8] = <<S_Workbench_Master>>.Constraints.TwobyfourWidth
  expr: Constraints[9] = <<S_Workbench_Master>>.Constraints.TwobyfourHeight
  sketch-geometry (4):
    g0: LineSegment StartX=-19.05 StartY=44.45 StartZ=0 EndX=19.05 EndY=44.45 EndZ=0
    g1: LineSegment StartX=19.05 StartY=44.45 StartZ=0 EndX=19.05 EndY=-44.45 EndZ=0
    g2: LineSegment StartX=19.05 StartY=-44.45 StartZ=0 EndX=-19.05 EndY=-44.45 EndZ=0
    g3: LineSegment StartX=-19.05 StartY=-44.45 StartZ=0 EndX=-19.05 EndY=44.45 EndZ=0
  constraints (11):
    c: Coincident(g0,g1)
    c: Coincident(g1,g2)
    c: Coincident(g2,g3)
    c: Coincident(g3,g0)
    c: Horizontal(g0)
    c: Horizontal(g2)
    c: Vertical(g1)
    c: Vertical(g3)
    c: DistanceX(g0,g0) = 38.1
    c: DistanceY(g1,g1) = 88.9
    c: Symmetric(g0,g1,g-1)
FEATURE [PartDesign::Pad] Pad023
  Direction = (0,0,1)
  Length = 457.2
  Length2 = 10
  Profile = -> Sketch037
  ReferenceAxis = -> Sketch037 [N_Axis]
  Type = 0
  expr: Length = 96 in - <<S_Workbench_Master>>.Constraints.BackLegHeight
FEATURE [PartDesign::Body] Body018  label="B_Workbench_CutList_2x4_Waste"
  Group = -> [Sketch037,Pad023]
  Origin = -> Origin037
  Placement = pos=(0,0,2006.6) rot=(0,0,1;0rad)
  Tip = -> Pad023
FEATURE [Sketcher::SketchObject] Sketch038
  FullyConstrained = true
  MapMode = 5
  Support = -> [XY_Plane036]
  expr: Constraints[10] = <<S_Workbench_Master>>.Constraints.TwobyfourHeight
  expr: Constraints[9] = <<S_Workbench_Master>>.Constraints.TwobyfourWidth
  sketch-geometry (4):
    g0: LineSegment StartX=-19.05 StartY=44.45 StartZ=0 EndX=19.05 EndY=44.45 EndZ=0
    g1: LineSegment StartX=19.05 StartY=44.45 StartZ=0 EndX=19.05 EndY=-44.45 EndZ=0
    g2: LineSegment StartX=19.05 StartY=-44.45 StartZ=0 EndX=-19.05 EndY=-44.45 EndZ=0
    g3: LineSegment StartX=-19.05 StartY=-44.45 StartZ=0 EndX=-19.05 EndY=44.45 EndZ=0
  constraints (11):
    c: Coincident(g0,g1)
    c: Coincident(g1,g2)
    c: Coincident(g2,g3)
    c: Coincident(g3,g0)
    c: Horizontal(g0)
    c: Horizontal(g2)
    c: Vertical(g1)
    c: Vertical(g3)
    c: Symmetric(g0,g1,g-1)
    c: DistanceX(g0,g0) = 38.1
    c: DistanceY(g1,g1) = 88.9
FEATURE [PartDesign::Pad] Pad024
  Direction = (0,0,1)
  Length = 1981.2
  Length2 = 10
  Profile = -> Sketch038
  ReferenceAxis = -> Sketch038 [N_Axis]
  Type = 0
  expr: Length = <<S_Workbench_Master>>.Constraints.BackLegHeight
FEATURE [PartDesign::Body] Body017  label="B_Workbench_CutList_2x4_BackLeg"
  Group = -> [Sketch038,Pad024]
  Origin = -> Origin036
  Tip = -> Pad024
FEATURE [Sketcher::SketchObject] Sketch040  label="S_Workbench_2x4_Profile"
  FullyConstrained = true
  Placement = pos=(0,0,0) rot=(1,0,0;1.5708rad)
  expr: Constraints[8] = <<S_Workbench_Master>>.Constraints.TwobyfourWidth
  expr: Constraints[9] = <<S_Workbench_Master>>.Constraints.TwobyfourHeight
  sketch-geometry (4):
    g0: LineSegment StartX=-19.05 StartY=44.45 StartZ=0 EndX=19.05 EndY=44.45 EndZ=0
    g1: LineSegment StartX=19.05 StartY=44.45 StartZ=0 EndX=19.05 EndY=-44.45 EndZ=0
    g2: LineSegment StartX=19.05 StartY=-44.45 StartZ=0 EndX=-19.05 EndY=-44.45 EndZ=0
    g3: LineSegment StartX=-19.05 StartY=-44.45 StartZ=0 EndX=-19.05 EndY=44.45 EndZ=0
  constraints (11):
    c: Coincident(g0,g1)
    c: Coincident(g1,g2)
    c: Coincident(g2,g3)
    c: Coincident(g3,g0)
    c: Horizontal(g0)
    c: Horizontal(g2)
    c: Vertical(g1)
    c: Vertical(g3)
    c: DistanceX(g0,g0) = 38.1
    c: DistanceY(g1,g1) = 88.9
    c: Symmetric(g0,g1,g-1)
FEATURE [Part::Part2DObjectPython] Clone2D  label="S_2x4_Profile (2D)"  # Draft 2D object (typed FeaturePython)
  Fuse = false
  Objects = -> [Sketch040]
  Placement = pos=(0,304.8,0) rot=(1,0,0;0rad)
  Scale = (1,1,1)
FEATURE [PartDesign::Pad] Pad025
  Direction = (0,0,1)
  Length = 2438.4
  Length2 = 10
  Placement = pos=(0,304.8,0) rot=(1,0,0;0rad)
  Profile = -> Clone2D
  ReferenceAxis = -> Clone2D [N_Axis]
  Type = 0
FEATURE [PartDesign::Body] Body022  label="B_Workbench_CutList_2x4_Whole"
  Group = -> [Clone2D,Pad025]
  Origin = -> Origin042
  Tip = -> Pad025
FEATURE [App::Part] Part017  label="P_Workbench_CutList_2x4_BackLeg"
  Group = -> [Body017,Body018,Body022]
  Origin = -> Origin035
FEATURE [Part::Part2DObjectPython] Clone2D001  label="S_2x4_Profile (2D)001"  # Draft 2D object (typed FeaturePython)
  Fuse = false
  Objects = -> [Sketch040]
  Scale = (1,1,1)
FEATURE [Part::Part2DObjectPython] Clone2D002  label="S_2x4_Profile (2D)001 (2D)"  # Draft 2D object (typed FeaturePython)
  Fuse = false
  Objects = -> [Clone2D001]
  Scale = (1,1,1)
FEATURE [Part::Part2DObjectPython] Clone2D003  label="S_2x4_Profile (2D)001 (2D) (2D)"  # Draft 2D object (typed FeaturePython)
  Fuse = false
  Objects = -> [Clone2D002]
  Scale = (1,1,1)
FEATURE [Part::Part2DObjectPython] Clone2D004  label="S_2x4_Profile (2D)001 (2D) (2D) (2D)"  # Draft 2D object (typed FeaturePython)
  Fuse = false
  Objects = -> [Clone2D003]
  Scale = (1,1,1)
FEATURE [PartDesign::Pad] Pad026
  Direction = (0,0,1)
  Length = 723.9
  Length2 = 10
  Profile = -> Clone2D001
  ReferenceAxis = -> Clone2D001 [N_Axis]
  Type = 0
  expr: Length = <<S_Workbench_Master>>.Constraints.FrontLegHeight
FEATURE [PartDesign::Body] Body019  label="P_2x4_CutList_FrontLeg_FrontLeg"
  Group = -> [Clone2D001,Pad026]
  Origin = -> Origin039
  Tip = -> Pad026
FEATURE [PartDesign::Pad] Pad027
  Direction = (0,0,1)
  Length = 1066.8
  Length2 = 10
  Profile = -> Clone2D002
  ReferenceAxis = -> Clone2D002 [N_Axis]
  Type = 0
  expr: Length = <<S_Workbench_Master>>.Constraints.TableWidth - 4 * Sketch009.Constraints.TwobyfourWidth
FEATURE [PartDesign::Body] Body020  label="P_2x4_CutList_FrontLeg_BackBrace"
  Group = -> [Clone2D002,Pad027]
  Origin = -> Origin040
  Placement = pos=(0,0,749.3) rot=(0,0,1;0rad)
  Tip = -> Pad027
  expr: .Placement.Base.z = <<S_Workbench_Master>>.Constraints.FrontLegHeight + 1 in
FEATURE [PartDesign::Pad] Pad028
  Direction = (0,0,1)
  Length = 647.7
  Length2 = 10
  Profile = -> Clone2D003
  ReferenceAxis = -> Clone2D003 [N_Axis]
  Type = 0
  expr: Length = 96 in - <<S_Workbench_Master>>.Constraints.FrontLegHeight - (<<S_Workbench_Master>>.Constraints.TableWidth - 4 * Sketch009.Constraints.TwobyfourWidth)
FEATURE [PartDesign::Body] Body021  label="P_2x4_CutList_FrontLeg_Waste"
  Group = -> [Clone2D003,Pad028]
  Origin = -> Origin041
  Placement = pos=(0,0,1841.5) rot=(0,0,1;0rad)
  Tip = -> Pad028
  expr: .Placement.Base.z = <<S_Workbench_Master>>.Constraints.FrontLegHeight + <<S_Workbench_Master>>.Constraints.TableWidth - 4 * Sketch009.Constraints.TwobyfourWidth + 2 in
FEATURE [PartDesign::Pad] Pad029
  Direction = (0,0,1)
  Length = 2438.4
  Length2 = 10
  Profile = -> Clone2D004
  ReferenceAxis = -> Clone2D004 [N_Axis]
  Type = 0
FEATURE [PartDesign::Body] Body023  label="B_2x4_CutList_FrontLeg_Whole"
  Group = -> [Clone2D004,Pad029]
  Origin = -> Origin043
  Placement = pos=(0,304.8,0) rot=(0,0,1;0rad)
  Tip = -> Pad029
FEATURE [App::Part] Part018  label="P_Workbench_CutList_2x4_FrontLeg"
  Group = -> [Body019,Body020,Body021,Body023]
  Origin = -> Origin038
FEATURE [Part::Part2DObjectPython] Clone2D005  label="S_2x4_Profile (2D)002"  # Draft 2D object (typed FeaturePython)
  Fuse = false
  Objects = -> [Sketch040]
  Scale = (1,1,1)
FEATURE [Part::Part2DObjectPython] Clone2D006  label="S_2x4_Profile (2D)003"  # Draft 2D object (typed FeaturePython)
  Fuse = false
  Objects = -> [Sketch040]
  Scale = (1,1,1)
FEATURE [Part::Part2DObjectPython] Clone2D007  label="S_2x4_Profile (2D)004"  # Draft 2D object (typed FeaturePython)
  Fuse = false
  Objects = -> [Sketch040]
  Scale = (1,1,1)
FEATURE [Part::Part2DObjectPython] Clone2D008  label="S_2x4_Profile (2D)005"  # Draft 2D object (typed FeaturePython)
  Fuse = false
  Objects = -> [Sketch040]
  Scale = (1,1,1)
FEATURE [PartDesign::Pad] Pad030
  Direction = (0,0,1)
  Length = 2438.4
  Length2 = 10
  Profile = -> Clone2D008
  ReferenceAxis = -> Clone2D008 [N_Axis]
  Type = 0
FEATURE [PartDesign::Body] Body027  label="B_Workbench_CutList_2x4_SideBrace_Whole"
  Group = -> [Clone2D008,Pad030]
  Origin = -> Origin048
  Placement = pos=(0,304.8,0) rot=(0,0,1;0rad)
  Tip = -> Pad030
FEATURE [PartDesign::Pad] Pad031
  Direction = (0,0,1)
  Length = 762
  Length2 = 10
  Profile = -> Clone2D005
  ReferenceAxis = -> Clone2D005 [N_Axis]
  Type = 0
  expr: Length = <<S_Workbench_Master>>.Constraints.TableDepth
FEATURE [PartDesign::Body] Body024  label="B_Workbench_CutList_2x4_SideBrace_0"
  Group = -> [Clone2D005,Pad031]
  Origin = -> Origin045
  Tip = -> Pad031
FEATURE [PartDesign::Pad] Pad032
  Direction = (0,0,1)
  Length = 762
  Length2 = 10
  Profile = -> Clone2D006
  ReferenceAxis = -> Clone2D006 [N_Axis]
  Type = 0
  expr: Length = <<S_Workbench_Master>>.Constraints.TableDepth
FEATURE [PartDesign::Body] Body025  label="B_Workbench_CutList_2x4_SideBrace_1"
  Group = -> [Clone2D006,Pad032]
  Origin = -> Origin046
  Placement = pos=(0,0,787.4) rot=(0,0,1;0rad)
  Tip = -> Pad032
  expr: .Placement.Base.z = <<S_Workbench_Master>>.Constraints.TableDepth + 1 in
FEATURE [PartDesign::Pad] Pad033
  Direction = (0,0,1)
  Length = 914.4
  Length2 = 10
  Profile = -> Clone2D007
  ReferenceAxis = -> Clone2D007 [N_Axis]
  Type = 0
  expr: Length = 96 in - <<S_Workbench_Master>>.Constraints.TableDepth * 2
FEATURE [PartDesign::Body] Body026  label="B_Workbench_CutList_2x4_SideBrace_Waste"
  Group = -> [Clone2D007,Pad033]
  Origin = -> Origin047
  Placement = pos=(0,0,1574.8) rot=(0,0,1;0rad)
  Tip = -> Pad033
  expr: .Placement.Base.z = <<S_Workbench_Master>>.Constraints.TableDepth * 2 + 2 in
FEATURE [App::Part] Part019  label="P_Workbench_CutList_2x4_SideBrace"
  Group = -> [Body024,Body025,Body026,Body027]
  Origin = -> Origin044
FEATURE [Sketcher::SketchObject] Sketch041  label="S_Workbench_Plywood_Sheet_1.2"
  FullyConstrained = true
  expr: Constraints[8] = <<S_Workbench_Master>>.Constraints.TwobyfourWidth
  expr: Constraints[9] = <<S_Workbench_Master>>.Constraints.TwobyfourHeight
  sketch-geometry (4):
    g0: LineSegment StartX=-19.05 StartY=44.45 StartZ=0 EndX=19.05 EndY=44.45 EndZ=0
    g1: LineSegment StartX=19.05 StartY=44.45 StartZ=0 EndX=19.05 EndY=-44.45 EndZ=0
    g2: LineSegment StartX=19.05 StartY=-44.45 StartZ=0 EndX=-19.05 EndY=-44.45 EndZ=0
    g3: LineSegment StartX=-19.05 StartY=-44.45 StartZ=0 EndX=-19.05 EndY=44.45 EndZ=0
  constraints (11):
    c: Coincident(g0,g1)
    c: Coincident(g1,g2)
    c: Coincident(g2,g3)
    c: Coincident(g3,g0)
    c: Horizontal(g0)
    c: Horizontal(g2)
    c: Vertical(g1)
    c: Vertical(g3)
    c: DistanceX(g0,g0) = 38.1
    c: DistanceY(g1,g1) = 88.9
    c: Symmetric(g0,g1,g-1)
FEATURE [App::DocumentObjectGroup] Group  label="Workbench_MasterSketches"
  Group = -> [Sketch009,Sketch040,Sketch041]
FEATURE [App::DocumentObjectGroup] Parts
  Group = -> [Part003,Part004,Part005,Group,Part006,Part007,Part008,Part009,Part010,Part011]
FEATURE [App::DocumentObjectGroup] Group001  label="Drawings-Old"
FEATURE [PartDesign::Body] Body031  label="B_Workbench_CutList_MDF_Whole"
  Origin = -> Origin053
FEATURE [App::Part] Part021  label="P_Workbench_CutList_MDF"
  Group = -> [Body031]
  Origin = -> Origin054
FEATURE [Sketcher::SketchObject] Sketch042
  FullyConstrained = true
  MapMode = 5
  Support = -> [XY_Plane055]
  sketch-geometry (5):
    g0: LineSegment StartX=-1219.2 StartY=-609.6 StartZ=0 EndX=-1219.2 EndY=609.6 EndZ=0
    g1: LineSegment StartX=-1219.2 StartY=609.6 StartZ=0 EndX=1219.2 EndY=609.6 EndZ=0
    g2: LineSegment StartX=1219.2 StartY=609.6 StartZ=0 EndX=1219.2 EndY=-609.6 EndZ=0
    g3: LineSegment StartX=1219.2 StartY=-609.6 StartZ=0 EndX=-1219.2 EndY=-609.6 EndZ=0
    g4: GeomPoint X=0 Y=0 Z=0
  constraints (12):
    c: Coincident(g0,g1)
    c: Coincident(g1,g2)
    c: Coincident(g2,g3)
    c: Coincident(g3,g0)
    c: Horizontal(g1)
    c: Horizontal(g3)
    c: Vertical(g0)
    c: Vertical(g2)
    c: Symmetric(g1,g0,g4)
    c: Coincident(g4,g-1)
    c: DistanceX(g1,g1) = 2438.4
    c: DistanceY(g2,g2) = 1219.2
FEATURE [PartDesign::Pad] Pad034
  Direction = (0,0,1)
  Length = 19.05
  Length2 = 10
  Profile = -> Sketch042
  ReferenceAxis = -> Sketch042 [N_Axis]
  Type = 0
FEATURE [PartDesign::Body] Body032  label="B_Workbench_CutList_Plywood_Whole"
  Group = -> [Sketch042,Pad034]
  Origin = -> Origin055
  Tip = -> Pad034
FEATURE [Part::FeaturePython] Clone  label="B_Workbench_Shelf001"  # Draft clone (typed FeaturePython)
  AttacherType = Attacher::AttachEngine3D
  Fuse = false
  Objects = -> [Body006]
  Placement = pos=(76.2,0,50.8) rot=(0,0,1;1.5708rad)
  Scale = (1,1,1)
FEATURE [Part::FeaturePython] Clone001  label="B_Workbench_Top001"  # Draft clone (typed FeaturePython)
  AttacherType = Attacher::AttachEngine3D
  Fuse = false
  Objects = -> [Body003]
  Placement = pos=(457.2,0,50.8) rot=(0,0,1;1.5708rad)
  Scale = (1,1,1)
FEATURE [Part::FeaturePython] Clone002  label="B_Workbench_ShelfBrace001"  # Draft clone (typed FeaturePython)
  AttacherType = Attacher::AttachEngine3D
  Fuse = false
  Objects = -> [Body010]
  Placement = pos=(-1219.2,609.6,50.8) rot=(0,-1,0;1.5708rad)
  Scale = (1,1,1)
FEATURE [Part::FeaturePython] Clone003  label="B_Workbench_ShelfBrace002"  # Draft clone (typed FeaturePython)
  AttacherType = Attacher::AttachEngine3D
  Fuse = false
  Objects = -> [Body010]
  Placement = pos=(-1219.2,228.6,50.8) rot=(0,-1,0;1.5708rad)
  Scale = (1,1,1)
  expr: .Placement.Base.y = 24 in - <<S_Workbench_Master>>.Constraints.ShelfDepth
FEATURE [Part::FeaturePython] Clone004  label="B_Workbench_ShelfBrace003"  # Draft clone (typed FeaturePython)
  AttacherType = Attacher::AttachEngine3D
  Fuse = false
  Objects = -> [Body010]
  Placement = pos=(-1028.7,228.6,50.8) rot=(0.707107,0,0.707107;3.14159rad)
  Scale = (1,1,1)
  expr: .Placement.Base.x = -48 in + <<S_Workbench_Master>>.Constraints.ShelfDepth / 2
  expr: .Placement.Base.y = 24 in - <<S_Workbench_Master>>.Constraints.ShelfDepth
FEATURE [Part::FeaturePython] Clone005  label="B_Workbench_ShelfBrace004"  # Draft clone (typed FeaturePython)
  AttacherType = Attacher::AttachEngine3D
  Fuse = false
  Objects = -> [Body010]
  Placement = pos=(-1028.7,-152.4,50.8) rot=(0.707107,0,0.707107;3.14159rad)
  Scale = (1,1,1)
  expr: .Placement.Base.x = -48 in + <<S_Workbench_Master>>.Constraints.ShelfDepth / 2
  expr: .Placement.Base.y = 24 in - <<S_Workbench_Master>>.Constraints.ShelfDepth * 2
FEATURE [App::DocumentObjectGroup] Group003  label="Templates"
  Group = -> [Part012,Part014,Part015,Part013,Part016]
FEATURE [Part::FeaturePython] Clone006  label="B_Workbench_Shelf002"  # Draft clone (typed FeaturePython)
  AttacherType = Attacher::AttachEngine3D
  Fuse = false
  Objects = -> [Body006]
  Placement = pos=(-304.8,0,50.8) rot=(0,0,1;1.5708rad)
  Scale = (1,1,1)
FEATURE [App::Part] Part020  label="P_Workbench_CutList_Plywood"
  Group = -> [Body032,Clone,Clone001,Clone002,Clone003,Clone004,Clone005,Clone006]
  Origin = -> Origin049
FEATURE [App::DocumentObjectGroup] Group002  label="CutList"
  Group = -> [Part017,Part018,Part019,Part020,Part021]
FEATURE [TechDraw::DrawSVGTemplate] Template011  label="TEMPLATE_Step2_CutList_2x4"
  EditableTexts = Code=JWB; CompanyAddress=570 Eagle View Dr NW; CompanyName=Ensor Robotics; DrawingNumber=2-1-CutList-2x4; DrawingTitle1=Cut List 2x4; DrawingTitle2=Cutting guide for 2x4 stock; DrawingTitle3=various parts cut as shown; DrawnBy=Jon A.; Revision=v1; Scale=1:20; Sheet=Sheet 2 of 11
  Height = 215.9
  Orientation = 1
  Template = /snap/freecad/908/usr/share/Mod/TechDraw/Templates/USLetter_Landscape.svg
  Width = 279.4
FEATURE [TechDraw::DrawViewPart] View019  label="VIEW_Step2_CutList_2x4_BackLeg"
  CoarseView = false
  Direction = (-1,0,0)
  Focus = 100
  HardHidden = false
  IsoCount = 0
  IsoHidden = false
  IsoVisible = false
  LockPosition = false
  Perspective = false
  Rotation = 0
  Scale = 0.05
  ScaleType = 0
  ScrubCount = 0
  SeamHidden = false
  SeamVisible = false
  SmoothHidden = false
  SmoothVisible = true
  Source = -> [Part017]
  X = 129.83
  XDirection = (0,-1,0)
  Y = 129.577
FEATURE [TechDraw::DrawViewPart] View020  label="VIEW_Step2_CutList_2x4_FrontLeg_BackBrace"
  CoarseView = false
  Direction = (-1,0,0)
  Focus = 100
  HardHidden = false
  IsoCount = 0
  IsoHidden = false
  IsoVisible = false
  LockPosition = false
  Perspective = false
  Rotation = 0
  Scale = 0.05
  ScaleType = 0
  ScrubCount = 0
  SeamHidden = false
  SeamVisible = false
  SmoothHidden = false
  SmoothVisible = true
  Source = -> [Part018]
  X = 54.0094
  XDirection = (0,-1,0)
  Y = 131.787
FEATURE [TechDraw::DrawViewPart] View021  label="VIEW_Step2_CutList_2x4_SideBrace"
  CoarseView = false
  Direction = (-1,0,0)
  Focus = 100
  HardHidden = false
  IsoCount = 0
  IsoHidden = false
  IsoVisible = false
  LockPosition = false
  Perspective = false
  Rotation = 0
  Scale = 0.05
  ScaleType = 0
  ScrubCount = 0
  SeamHidden = false
  SeamVisible = false
  SmoothHidden = false
  SmoothVisible = true
  Source = -> [Part019]
  X = 215.898
  XDirection = (0,-1,0)
  Y = 129.318
FEATURE [TechDraw::DrawViewDimension] Dimension002  label="DIM_Step1_CutList_FrontLeg"
  AngleOverride = false
  Arbitrary = false
  ArbitraryTolerances = false
  EqualTolerance = true
  ExtensionAngle = 0
  FormatSpec = %.2w
  FormatSpecOverTolerance = %+.2w
  FormatSpecUnderTolerance = %+.2w
  Inverted = false
  LineAngle = 0
  LockPosition = false
  MeasureType = 1
  OverTolerance = 0
  References2D = -> [View020]
  Rotation = 0
  Scale = 0.05
  ScaleType = 0
  TheoreticalExact = false
  Type = 2
  UnderTolerance = 0
  X = -1.62424
  Y = -42.1683
FEATURE [TechDraw::DrawViewDimension] Dimension003  label="DIM_Step1_CutList_BackBrace"
  AngleOverride = false
  Arbitrary = false
  ArbitraryTolerances = false
  EqualTolerance = true
  ExtensionAngle = 0
  FormatSpec = %.2w
  FormatSpecOverTolerance = %+.2w
  FormatSpecUnderTolerance = %+.2w
  Inverted = false
  LineAngle = 0
  LockPosition = false
  MeasureType = 1
  OverTolerance = 0
  References2D = -> [View020]
  Rotation = 0
  Scale = 0.05
  ScaleType = 0
  TheoreticalExact = false
  Type = 2
  UnderTolerance = 0
  X = -2.03902
  Y = 4.44821
FEATURE [TechDraw::DrawViewDimension] Dimension004  label="DIM_RawMaterial"
  AngleOverride = false
  Arbitrary = false
  ArbitraryTolerances = false
  EqualTolerance = true
  ExtensionAngle = 0
  FormatSpec = %.2w
  FormatSpecOverTolerance = %+.2w
  FormatSpecUnderTolerance = %+.2w
  Inverted = false
  LineAngle = 0
  LockPosition = false
  MeasureType = 1
  OverTolerance = 0
  References2D = -> [View020]
  Rotation = 0
  Scale = 0.05
  ScaleType = 0
  TheoreticalExact = false
  Type = 2
  UnderTolerance = 0
  X = -21.0759
  Y = 0.36589
FEATURE [TechDraw::DrawRichAnno] RichTextAnnotation010  label="TEXT_Step2_CutList_2x4_FrontLeg_BackBrace"
  AnnoText = <!DOCTYPE HTML PUBLIC "-//W3C//DTD HTML 4.0//EN" "http://www.w3.org/TR/REC-html40/strict.dtd">\n<html><head><meta name="qrichtext" content="1" /><style type="text/css">\np, li { white-space: pre-wrap; }\n</style></head><body style=" font-family:'osifont'; font-size:9pt; font-weight:400; font-style:normal;">\n<p style=" margin-top:0px; margin-bottom:0px; margin-left:0px; margin-right:0px; -qt-block-indent:0; text-indent:0px;"><span style=" font-family:'Sans Serif'; font-size:10pt;">Cut two each of Front leg (2) (28.5 inch) and Back Brace (1) (42 inch) from a length of 8 foot 2x4 stock.</span></p></body></html>
  LockPosition = false
  MaxWidth = 50
  Rotation = 0
  Scale = 0.05
  ScaleType = 0
  ShowFrame = false
  X = 49.8028
  Y = 47.0494
FEATURE [TechDraw::DrawViewBalloon] Balloon023
  BubbleShape = 0
  EndType = 0
  EndTypeScale = 1
  KinkLength = 5
  LockPosition = false
  OriginX = 182.565
  OriginY = -105.71
  Rotation = 0
  Scale = 0.05
  ScaleType = 0
  ShapeScale = 1
  SourceView = -> View020
  Text = 1
  TextWrapLen = -1
  X = 582.565
  Y = 294.29
FEATURE [TechDraw::DrawRichAnno] RichTextAnnotation011  label="TEXT_Step2_CutList_2x4_BackLeg"
  AnnoText = <!DOCTYPE HTML PUBLIC "-//W3C//DTD HTML 4.0//EN" "http://www.w3.org/TR/REC-html40/strict.dtd">\n<html><head><meta name="qrichtext" content="1" /><style type="text/css">\np, li { white-space: pre-wrap; }\n</style></head><body style=" font-family:'osifont'; font-size:9pt; font-weight:400; font-style:normal;">\n<p style=" margin-top:0px; margin-bottom:0px; margin-left:0px; margin-right:0px; -qt-block-indent:0; text-indent:0px;"><span style=" font-family:'Sans Serif'; font-size:10pt;">Cut two back leg (3) (78 inch) from a length of 8 foot 2x4 stock.</span></p></body></html>
  LockPosition = false
  MaxWidth = 50
  Rotation = 0
  Scale = 0.05
  ScaleType = 0
  ShowFrame = false
  X = 96.3239
  Y = 121.67
FEATURE [TechDraw::DrawViewDimension] Dimension005  label="DIM_Step1_CutList_BackLeg"
  AngleOverride = false
  Arbitrary = false
  ArbitraryTolerances = false
  EqualTolerance = true
  ExtensionAngle = 0
  FormatSpec = %.2w
  FormatSpecOverTolerance = %+.2w
  FormatSpecUnderTolerance = %+.2w
  Inverted = false
  LineAngle = 0
  LockPosition = false
  MeasureType = 1
  OverTolerance = 0
  References2D = -> [View019]
  Rotation = 0
  Scale = 0.05
  ScaleType = 0
  TheoreticalExact = false
  Type = 2
  UnderTolerance = 0
  X = 17.606
  Y = -11.5903
FEATURE [TechDraw::DrawViewDimension] Dimension006  label="DIM_Step1_CutList_SideBrace0"
  AngleOverride = false
  Arbitrary = false
  ArbitraryTolerances = false
  EqualTolerance = true
  ExtensionAngle = 0
  FormatSpec = %.2w
  FormatSpecOverTolerance = %+.2w
  FormatSpecUnderTolerance = %+.2w
  Inverted = false
  LineAngle = 0
  LockPosition = false
  MeasureType = 1
  OverTolerance = 0
  References2D = -> [View021]
  Rotation = 0
  Scale = 0.05
  ScaleType = 0
  TheoreticalExact = false
  Type = 2
  UnderTolerance = 0
  X = 21.6565
  Y = -2.66017
FEATURE [TechDraw::DrawViewDimension] Dimension007  label="DIM_Step1_CutList_SideBrace1"
  AngleOverride = false
  Arbitrary = false
  ArbitraryTolerances = false
  EqualTolerance = true
  ExtensionAngle = 0
  FormatSpec = %.2w
  FormatSpecOverTolerance = %+.2w
  FormatSpecUnderTolerance = %+.2w
  Inverted = false
  LineAngle = 0
  LockPosition = false
  MeasureType = 1
  OverTolerance = 0
  References2D = -> [View021]
  Rotation = 0
  Scale = 0.05
  ScaleType = 0
  TheoreticalExact = false
  Type = 2
  UnderTolerance = 0
  X = 21.9941
  Y = -40.0049
FEATURE [TechDraw::DrawViewBalloon] Balloon025
  BubbleShape = 0
  EndType = 0
  EndTypeScale = 1
  KinkLength = 5
  LockPosition = false
  OriginX = 147.548
  OriginY = -134.362
  Rotation = 0
  Scale = 0.05
  ScaleType = 0
  ShapeScale = 1
  SourceView = -> View019
  Text = 3
  TextWrapLen = -1
  X = 625.012
  Y = 463.079
FEATURE [TechDraw::DrawRichAnno] RichTextAnnotation012  label="TEXT_Step2_CutList_2x4_SideBrace"
  AnnoText = <!DOCTYPE HTML PUBLIC "-//W3C//DTD HTML 4.0//EN" "http://www.w3.org/TR/REC-html40/strict.dtd">\n<html><head><meta name="qrichtext" content="1" /><style type="text/css">\np, li { white-space: pre-wrap; }\n</style></head><body style=" font-family:'osifont'; font-size:9pt; font-weight:400; font-style:normal;">\n<p style=" margin-top:0px; margin-bottom:0px; margin-left:0px; margin-right:0px; -qt-block-indent:0; text-indent:0px;"><span style=" font-family:'Sans Serif'; font-size:10pt;">Cut four side brace (4,5) (30 inch) from two lengths of 8 foot 2x4 stock.</span></p></body></html>
  LockPosition = false
  MaxWidth = 50
  Rotation = 0
  Scale = 0.05
  ScaleType = 0
  ShowFrame = false
  X = 178.892
  Y = 123.862
FEATURE [TechDraw::DrawSVGTemplate] Template012  label="TEMPLATE_Step1_Templates"
  EditableTexts = Code=JWB; CompanyAddress=570 Eagle View Dr NW; CompanyName=Ensor Robotics; DrawingNumber=1-1-Templates; DrawingTitle1=Templates; DrawingTitle2=3d-printed templates; DrawingTitle3=for marking and aligning holes; DrawnBy=Jon A.; Revision=v1; Scale=1:2; Sheet=Sheet 1 of 11; Weight=N/A
  Height = 215.9
  Orientation = 1
  Template = /snap/freecad/908/usr/share/Mod/TechDraw/Templates/USLetter_Landscape.svg
  Width = 279.4
FEATURE [TechDraw::DrawViewPart] View022  label="VIEW_Step1_Templates_FrontLeg"
  CoarseView = false
  Direction = (0,0,-1)
  Focus = 100
  HardHidden = false
  IsoCount = 0
  IsoHidden = false
  IsoVisible = false
  LockPosition = false
  Perspective = false
  Rotation = 0
  Scale = 0.5
  ScaleType = 0
  ScrubCount = 0
  SeamHidden = false
  SeamVisible = false
  SmoothHidden = false
  SmoothVisible = true
  Source = -> [Part012]
  X = 49.0851
  XDirection = (-1,0,0)
  Y = 143.351
FEATURE [TechDraw::DrawViewPart] View023  label="VIEW_Step1_Templates_BackLegShelfHoles"
  CoarseView = false
  Direction = (0,0,-1)
  Focus = 100
  HardHidden = false
  IsoCount = 0
  IsoHidden = false
  IsoVisible = false
  LockPosition = false
  Perspective = false
  Rotation = 0
  Scale = 0.5
  ScaleType = 0
  ScrubCount = 0
  SeamHidden = false
  SeamVisible = false
  SmoothHidden = false
  SmoothVisible = true
  Source = -> [Part014]
  X = 109.404
  XDirection = (-1,0,0)
  Y = 154.894
FEATURE [TechDraw::DrawViewPart] View024  label="VIEW_Step1_Templates_ShelfBrace"
  CoarseView = false
  Direction = (0,0,-1)
  Focus = 100
  HardHidden = false
  IsoCount = 0
  IsoHidden = false
  IsoVisible = false
  LockPosition = false
  Perspective = false
  Rotation = 0
  Scale = 0.5
  ScaleType = 0
  ScrubCount = 0
  SeamHidden = false
  SeamVisible = false
  SmoothHidden = false
  SmoothVisible = true
  Source = -> [Part015]
  X = 228.553
  XDirection = (-1,0,0)
  Y = 126.596
FEATURE [TechDraw::DrawViewPart] View025  label="VIEW_Step1_Templates_SideBraceLeft"
  CoarseView = false
  Direction = (0,0,-1)
  Focus = 100
  HardHidden = false
  IsoCount = 0
  IsoHidden = false
  IsoVisible = false
  LockPosition = false
  Perspective = false
  Rotation = 0
  Scale = 0.5
  ScaleType = 0
  ScrubCount = 0
  SeamHidden = false
  SeamVisible = false
  SmoothHidden = false
  SmoothVisible = true
  Source = -> [Part013]
  X = 163.021
  XDirection = (-1,0,0)
  Y = 99.4149
FEATURE [TechDraw::DrawViewPart] View026  label="VIEW_Step1_Templates_SideBraceRight"
  CoarseView = false
  Direction = (0,0,-1)
  Focus = 100
  HardHidden = false
  IsoCount = 0
  IsoHidden = false
  IsoVisible = false
  LockPosition = false
  Perspective = false
  Rotation = 0
  Scale = 0.5
  ScaleType = 0
  ScrubCount = 0
  SeamHidden = false
  SeamVisible = false
  SmoothHidden = false
  SmoothVisible = true
  Source = -> [Part016]
  X = 164.883
  XDirection = (-1,0,0)
  Y = 162.34
FEATURE [TechDraw::DrawRichAnno] RichTextAnnotation013  label="TEXT_Step1_Templates_Instructions"
  AnnoText = <!DOCTYPE HTML PUBLIC "-//W3C//DTD HTML 4.0//EN" "http://www.w3.org/TR/REC-html40/strict.dtd">\n<html><head><meta name="qrichtext" content="1" /><style type="text/css">\np, li { white-space: pre-wrap; }\n</style></head><body style=" font-family:'osifont'; font-size:9pt; font-weight:400; font-style:normal;">\n<p style=" margin-top:0px; margin-bottom:0px; margin-left:0px; margin-right:0px; -qt-block-indent:0; text-indent:0px;"><span style=" font-family:'Sans Serif'; font-size:10pt;">3d-print templates for marking holes in each of the key locations.</span></p>\n<p style="-qt-paragraph-type:empty; margin-top:0px; margin-bottom:0px; margin-left:0px; margin-right:0px; -qt-block-indent:0; text-indent:0px; font-family:'Sans Serif'; font-size:10pt;"><br /></p>\n<p style=" margin-top:0px; margin-bottom:0px; margin-left:0px; margin-right:0px; -qt-block-indent:0; text-indent:0px;"><span style=" font-family:'Sans Serif'; font-size:10pt;">All holes should be drilled to 5/16 inch so that 1/4 inch bolts slide through easily.</span></p></body></html>
  LockPosition = false
  MaxWidth = 50
  Rotation = 0
  Scale = 0.5
  ScaleType = 0
  ShowFrame = false
  X = 64.8596
  Y = 56.567
FEATURE [TechDraw::DrawPage] Page012  label="DRAWING_Step1_Templates"
  KeepUpdated = true
  NextBalloonIndex = 1
  ProjectionType = 0
  Scale = 0.5
  Template = -> Template012
  Views = -> [View022,View023,View024,View025,View026,RichTextAnnotation013]
FEATURE [TechDraw::DrawViewBalloon] Balloon028
  BubbleShape = 0
  EndType = 0
  EndTypeScale = 1
  KinkLength = 5
  LockPosition = false
  OriginX = 158.256
  OriginY = -781.39
  Rotation = 0
  Scale = 0.05
  ScaleType = 0
  ShapeScale = 1
  SourceView = -> View020
  Text = 2
  TextWrapLen = -1
  X = 551.634
  Y = -864.847
FEATURE [TechDraw::DrawViewBalloon] Balloon029
  BubbleShape = 0
  EndType = 0
  EndTypeScale = 1
  KinkLength = 5
  LockPosition = false
  OriginX = 158.976
  OriginY = 148.822
  Rotation = 0
  Scale = 0.05
  ScaleType = 0
  ShapeScale = 1
  SourceView = -> View021
  Text = 4
  TextWrapLen = -1
  X = 611.958
  Y = 826.975
FEATURE [TechDraw::DrawViewBalloon] Balloon030
  BubbleShape = 0
  EndType = 0
  EndTypeScale = 1
  KinkLength = 5
  LockPosition = false
  OriginX = 152.353
  OriginY = -692.261
  Rotation = 0
  Scale = 0.05
  ScaleType = 0
  ShapeScale = 1
  SourceView = -> View021
  Text = 5
  TextWrapLen = -1
  X = 724.544
  Y = -649.887
FEATURE [TechDraw::DrawPage] Page011  label="DRAWING_Step2_CutList_2x4"
  KeepUpdated = true
  NextBalloonIndex = 10
  ProjectionType = 0
  Scale = 0.05
  Template = -> Template011
  Views = -> [View019,View020,View021,Dimension002,Dimension003,Dimension004,RichTextAnnotation010,Balloon023,RichTextAnnotation011,Dimension005,Dimension006,Dimension007,Balloon025,RichTextAnnotation012,Balloon028,Balloon029,Balloon030]
FEATURE [TechDraw::DrawSVGTemplate] Template013  label="TEMPLATE_Step3_CutList_Plywood"
  EditableTexts = Code=JWB; CompanyAddress=570 Eagle View Dr NW; CompanyName=Ensor Robotics; DrawingNumber=3-1-CutList-Plywood; DrawingTitle1=Cut List Plywood; DrawingTitle2=Table Top, Shelves, Shelf Braces; DrawnBy=Jon A.; Revision=v1; Scale=1:20; Sheet=Sheet 3 of 11
  Height = 215.9
  Orientation = 1
  Template = /snap/freecad/908/usr/share/Mod/TechDraw/Templates/USLetter_Landscape.svg
  Width = 279.4
FEATURE [TechDraw::DrawViewPart] View027  label="VIEW_Step3_CutList_Plywood_Various"
  CoarseView = false
  Direction = (0,0,1)
  Focus = 100
  HardHidden = false
  IsoCount = 0
  IsoHidden = false
  IsoVisible = false
  LockPosition = false
  Perspective = false
  Rotation = 0
  Scale = 0.05
  ScaleType = 0
  ScrubCount = 0
  SeamHidden = false
  SeamVisible = false
  SmoothHidden = false
  SmoothVisible = true
  Source = -> [Part020]
  X = 175.589
  XDirection = (1,0,0)
  Y = 134.605
FEATURE [TechDraw::DrawViewDimension] Dimension008  label="DIM_Step3_CutList_Plywood_TopDepth"
  AngleOverride = false
  Arbitrary = false
  ArbitraryTolerances = false
  EqualTolerance = true
  ExtensionAngle = 0
  FormatSpec = %.2w
  FormatSpecOverTolerance = %+.2w
  FormatSpecUnderTolerance = %+.2w
  Inverted = false
  LineAngle = 0
  LockPosition = false
  MeasureType = 1
  OverTolerance = 0
  References2D = -> [View027]
  Rotation = 0
  Scale = 0.05
  ScaleType = 0
  TheoreticalExact = false
  Type = 1
  UnderTolerance = 0
  X = 41.6453
  Y = 46.5901
FEATURE [TechDraw::DrawViewDimension] Dimension009  label="DIM_Step3_CutList_Plywood_TopWidth"
  AngleOverride = false
  Arbitrary = false
  ArbitraryTolerances = false
  EqualTolerance = true
  ExtensionAngle = 0
  FormatSpec = %.2w
  FormatSpecOverTolerance = %+.2w
  FormatSpecUnderTolerance = %+.2w
  Inverted = false
  LineAngle = 0
  LockPosition = false
  MeasureType = 1
  OverTolerance = 0
  References2D = -> [View027]
  Rotation = 0
  Scale = 0.05
  ScaleType = 0
  TheoreticalExact = false
  Type = 2
  UnderTolerance = 0
  X = 74.8737
  Y = 1.58763
FEATURE [TechDraw::DrawViewDimension] Dimension010  label="DIM_Step3_CutList_Plywood_ShelfDepth0"
  AngleOverride = false
  Arbitrary = false
  ArbitraryTolerances = false
  EqualTolerance = true
  ExtensionAngle = 0
  FormatSpec = %.2w
  FormatSpecOverTolerance = %+.2w
  FormatSpecUnderTolerance = %+.2w
  Inverted = false
  LineAngle = 0
  LockPosition = false
  MeasureType = 1
  OverTolerance = 0
  References2D = -> [View027]
  Rotation = 0
  Scale = 0.05
  ScaleType = 0
  TheoreticalExact = false
  Type = 1
  UnderTolerance = 0
  X = 16.5525
  Y = -45.5522
FEATURE [TechDraw::DrawViewDimension] Dimension011  label="DIM_Step3_CutList_Plywood_ShelfDepth1"
  AngleOverride = false
  Arbitrary = false
  ArbitraryTolerances = false
  EqualTolerance = true
  ExtensionAngle = 0
  FormatSpec = %.2w
  FormatSpecOverTolerance = %+.2w
  FormatSpecUnderTolerance = %+.2w
  Inverted = false
  LineAngle = 0
  LockPosition = false
  MeasureType = 1
  OverTolerance = 0
  References2D = -> [View027]
  Rotation = 0
  Scale = 0.05
  ScaleType = 0
  TheoreticalExact = false
  Type = 1
  UnderTolerance = 0
  X = -8.68496
  Y = -45.3422
FEATURE [TechDraw::DrawViewDimension] Dimension012  label="DIM_Step3_CutList_Plywood_LegNotch_Height"
  AngleOverride = false
  Arbitrary = false
  ArbitraryTolerances = false
  EqualTolerance = true
  ExtensionAngle = 0
  FormatSpec = %.2w
  FormatSpecOverTolerance = %+.2w
  FormatSpecUnderTolerance = %+.2w
  Inverted = false
  LineAngle = 0
  LockPosition = false
  MeasureType = 1
  OverTolerance = 0
  References2D = -> [View027]
  Rotation = 0
  Scale = 0.05
  ScaleType = 0
  TheoreticalExact = false
  Type = 1
  UnderTolerance = 0
  X = -27.6267
  Y = 47.8326
FEATURE [TechDraw::DrawViewDimension] Dimension013  label="DIM_Step3_CutList_Plywood_LegNotch_Width"
  AngleOverride = false
  Arbitrary = false
  ArbitraryTolerances = false
  EqualTolerance = true
  ExtensionAngle = 0
  FormatSpec = %.2w
  FormatSpecOverTolerance = %+.2w
  FormatSpecUnderTolerance = %+.2w
  Inverted = false
  LineAngle = 0
  LockPosition = false
  MeasureType = 1
  OverTolerance = 0
  References2D = -> [View027]
  Rotation = 0
  Scale = 0.05
  ScaleType = 0
  TheoreticalExact = false
  Type = 2
  UnderTolerance = 0
  X = -9.79241
  Y = 20.7126
FEATURE [TechDraw::DrawViewDimension] Dimension014  label="DIM_Step3_CutList_Plywood_ShelfBrace_Depth"
  AngleOverride = false
  Arbitrary = false
  ArbitraryTolerances = false
  EqualTolerance = true
  ExtensionAngle = 0
  FormatSpec = %.2w
  FormatSpecOverTolerance = %+.2w
  FormatSpecUnderTolerance = %+.2w
  Inverted = false
  LineAngle = 0
  LockPosition = false
  MeasureType = 1
  OverTolerance = 0
  References2D = -> [View027]
  Rotation = 0
  Scale = 0.05
  ScaleType = 0
  TheoreticalExact = false
  Type = 2
  UnderTolerance = 0
  X = -73.6519
  Y = 24.7501
FEATURE [TechDraw::DrawViewDimension] Dimension015  label="DIM_Step3_CutList_Plywood_ShelfBrace_Height"
  AngleOverride = false
  Arbitrary = false
  ArbitraryTolerances = false
  EqualTolerance = true
  ExtensionAngle = 0
  FormatSpec = %.2w
  FormatSpecOverTolerance = %+.2w
  FormatSpecUnderTolerance = %+.2w
  Inverted = false
  LineAngle = 0
  LockPosition = false
  MeasureType = 1
  OverTolerance = 0
  References2D = -> [View027]
  Rotation = 0
  Scale = 0.05
  ScaleType = 0
  TheoreticalExact = false
  Type = 1
  UnderTolerance = 0
  X = -57.1041
  Y = 46.449
FEATURE [TechDraw::DrawRichAnno] RichTextAnnotation014  label="TEXT_Step3_CutList_Instructions"
  AnnoText = <blob: 2159 chars omitted>
  LockPosition = false
  MaxWidth = 80
  Rotation = 0
  Scale = 0.05
  ScaleType = 0
  ShowFrame = false
  X = 65.8563
  Y = 105
FEATURE [TechDraw::DrawViewBalloon] Balloon031  label="BALOON_Step3_CutList_Plywood_TableTop"
  BubbleShape = 0
  EndType = 0
  EndTypeScale = 1
  KinkLength = 5
  LockPosition = false
  OriginX = 836.329
  OriginY = 256.269
  Rotation = 0
  Scale = 0.05
  ScaleType = 0
  ShapeScale = 1
  SourceView = -> View027
  Text = 1
  TextWrapLen = -1
  X = 1258.66
  Y = 1117.88
FEATURE [TechDraw::DrawViewBalloon] Balloon032  label="BALOON_Step3_CutList_Plywood_Shelf0"
  BubbleShape = 0
  EndType = 0
  EndTypeScale = 1
  KinkLength = 5
  LockPosition = false
  OriginX = 292.816
  OriginY = -458.487
  Rotation = 0
  Scale = 0.05
  ScaleType = 0
  ShapeScale = 1
  SourceView = -> View027
  Text = 4
  TextWrapLen = -1
  X = 1020.41
  Y = -1085.95
FEATURE [TechDraw::DrawViewBalloon] Balloon033  label="BALOON_Step3_CutList_Plywood_Shelf1"
  BubbleShape = 0
  EndType = 0
  EndTypeScale = 1
  KinkLength = 5
  LockPosition = false
  OriginX = -57.1163
  OriginY = -465.932
  Rotation = 0
  Scale = 0.05
  ScaleType = 0
  ShapeScale = 1
  SourceView = -> View027
  Text = 5
  TextWrapLen = -1
  X = -692.023
  Y = -1123.18
FEATURE [TechDraw::DrawViewBalloon] Balloon034  label="BALOON_Step3_CutList_Plywood_ShelfBrace"
  BubbleShape = 0
  EndType = 0
  EndTypeScale = 1
  KinkLength = 5
  LockPosition = false
  OriginX = -1144.14
  OriginY = 479.631
  Rotation = 0
  Scale = 0.05
  ScaleType = 0
  ShapeScale = 1
  SourceView = -> View027
  Text = 3
  TextWrapLen = -1
  X = -2106.64
  Y = 872.185
FEATURE [TechDraw::DrawViewBalloon] Balloon035  label="BALOON_Step3_CutList_Plywood_LegNotch"
  BubbleShape = 0
  EndType = 0
  EndTypeScale = 1
  KinkLength = 5
  LockPosition = false
  OriginX = 129.018
  OriginY = 591.311
  Rotation = 0
  Scale = 0.05
  ScaleType = 0
  ShapeScale = 1
  SourceView = -> View027
  Text = 2
  TextWrapLen = -1
  X = 171.64
  Y = 1043.43
FEATURE [TechDraw::DrawPage] Page013  label="DRAWING_Step3_CutList_Plywood"
  KeepUpdated = true
  NextBalloonIndex = 8
  ProjectionType = 0
  Scale = 0.05
  Template = -> Template013
  Views = -> [View027,Dimension008,Dimension009,Dimension010,Dimension011,Dimension012,Dimension013,Dimension014,Dimension015,RichTextAnnotation014,Balloon031,Balloon032,Balloon033,Balloon034,Balloon035]
FEATURE [TechDraw::DrawViewBalloon] Balloon036  label="BALOON_Step8_SideAssembly_SideBrace"
  BubbleShape = 3
  EndType = 0
  EndTypeScale = 1
  KinkLength = 5
  LockPosition = false
  OriginX = 142.005
  OriginY = -396.585
  Rotation = 0
  Scale = 0.08
  ScaleType = 0
  ShapeScale = 1
  SourceView = -> View015
  Text = Side Brace
  TextWrapLen = -1
  X = 1022.92
  Y = -70.642
FEATURE [TechDraw::DrawViewBalloon] Balloon037  label="BALOON_Step8_SideAssembly_Front Leg"
  BubbleShape = 3
  EndType = 0
  EndTypeScale = 1
  KinkLength = 5
  LockPosition = false
  OriginX = -354.545
  OriginY = -513.42
  Rotation = 0
  Scale = 0.08
  ScaleType = 0
  ShapeScale = 1
  SourceView = -> View015
  Text = Front Leg
  TextWrapLen = -1
  X = -279.799
  Y = -41.4331
FEATURE [TechDraw::DrawViewBalloon] Balloon038  label="BALOON_Step8_SideAssembly_BackLeg"
  BubbleShape = 3
  EndType = 0
  EndTypeScale = 1
  KinkLength = 5
  LockPosition = false
  OriginX = 328.942
  OriginY = 129.175
  Rotation = 0
  Scale = 0.08
  ScaleType = 0
  ShapeScale = 1
  SourceView = -> View015
  Text = Back Leg
  TextWrapLen = -1
  X = 1052.13
  Y = 192.238
FEATURE [TechDraw::DrawPage] Page007  label="DRAWING_Step8_SideAssembly"
  KeepUpdated = true
  NextBalloonIndex = 7
  ProjectionType = 0
  Scale = 0.08
  Template = -> Template007
  Views = -> [View015,RichTextAnnotation006,Balloon036,Balloon037,Balloon038]
FEATURE [TechDraw::DrawViewPart] View  label="VIEW_Step11_FullyAssembled"
  CoarseView = false
  Direction = (0.707373,-0.672957,0.216221)
  Focus = 100
  HardHidden = false
  IsoCount = 0
  IsoHidden = false
  IsoVisible = false
  LockPosition = false
  Perspective = false
  Rotation = 0
  Scale = 0.0625
  ScaleType = 0
  ScrubCount = 0
  SeamHidden = false
  SeamVisible = false
  SmoothHidden = false
  SmoothVisible = true
  Source = -> [Assembly]
  X = 84.9647
  XDirection = (0.691581,0.722144,-0.0149561)
  Y = 128.615
FEATURE [TechDraw::DrawRichAnno] RichTextAnnotation015  label="TEXT_Step11_FullyAssembled_Instructions"
  AnnoText = <!DOCTYPE HTML PUBLIC "-//W3C//DTD HTML 4.0//EN" "http://www.w3.org/TR/REC-html40/strict.dtd">\n<html><head><meta name="qrichtext" content="1" /><style type="text/css">\np, li { white-space: pre-wrap; }\n</style></head><body style=" font-family:'Sans Serif'; font-size:9pt; font-weight:400; font-style:normal;">\n<p style=" margin-top:0px; margin-bottom:0px; margin-left:0px; margin-right:0px; -qt-block-indent:0; text-indent:0px;"><span style=" font-size:10pt;">Congratulations.  The workbench is now fully assembled.  Perform final adjustments, square the assembly, and place it for use in your shop.</span></p>\n<p style="-qt-paragraph-type:empty; margin-top:0px; margin-bottom:0px; margin-left:0px; margin-right:0px; -qt-block-indent:0; text-indent:0px; font-size:10pt;"><br /></p>\n<p style=" margin-top:0px; margin-bottom:0px; margin-left:0px; margin-right:0px; -qt-block-indent:0; text-indent:0px;"><span style=" font-size:10pt;">Happy building!</span></p>\n<p style="-qt-paragraph-type:empty; margin-top:0px; margin-bottom:0px; margin-left:0px; margin-right:0px; -qt-block-indent:0; text-indent:0px; font-size:10pt;"><br /></p></body></html>
  LockPosition = false
  MaxWidth = 80
  Rotation = 0
  Scale = 0.0625
  ScaleType = 0
  ShowFrame = false
  X = 192.986
  Y = 148.068
FEATURE [TechDraw::DrawPage] Page  label="DRAWING_Step11_FullyAssembled"
  KeepUpdated = true
  NextBalloonIndex = 11
  ProjectionType = 0
  Scale = 0.0625
  Template = -> Template
  Views = -> [View,RichTextAnnotation015]
  expr: Scale = 1 / 16
FEATURE [App::DocumentObjectGroup] Group004  label="Plans"
  Group = -> [Page012,Page011,Page013,Page001,Page003,Page005,Page004,Page007,Page009,Page010,Page]
FEATURE [App::DocumentObjectGroup] Group005  label="Workbench"
  Group = -> [Parts,Group004,Assembly,Spreadsheet,Group002,Group003]
FEATURE [App::DocumentObjectGroup] Group006  label="CableMounts"
  Group = -> [Part,Part001]
note: 3 file-system paths scrubbed to <path> (originals preserved in the JSON sidecar)
